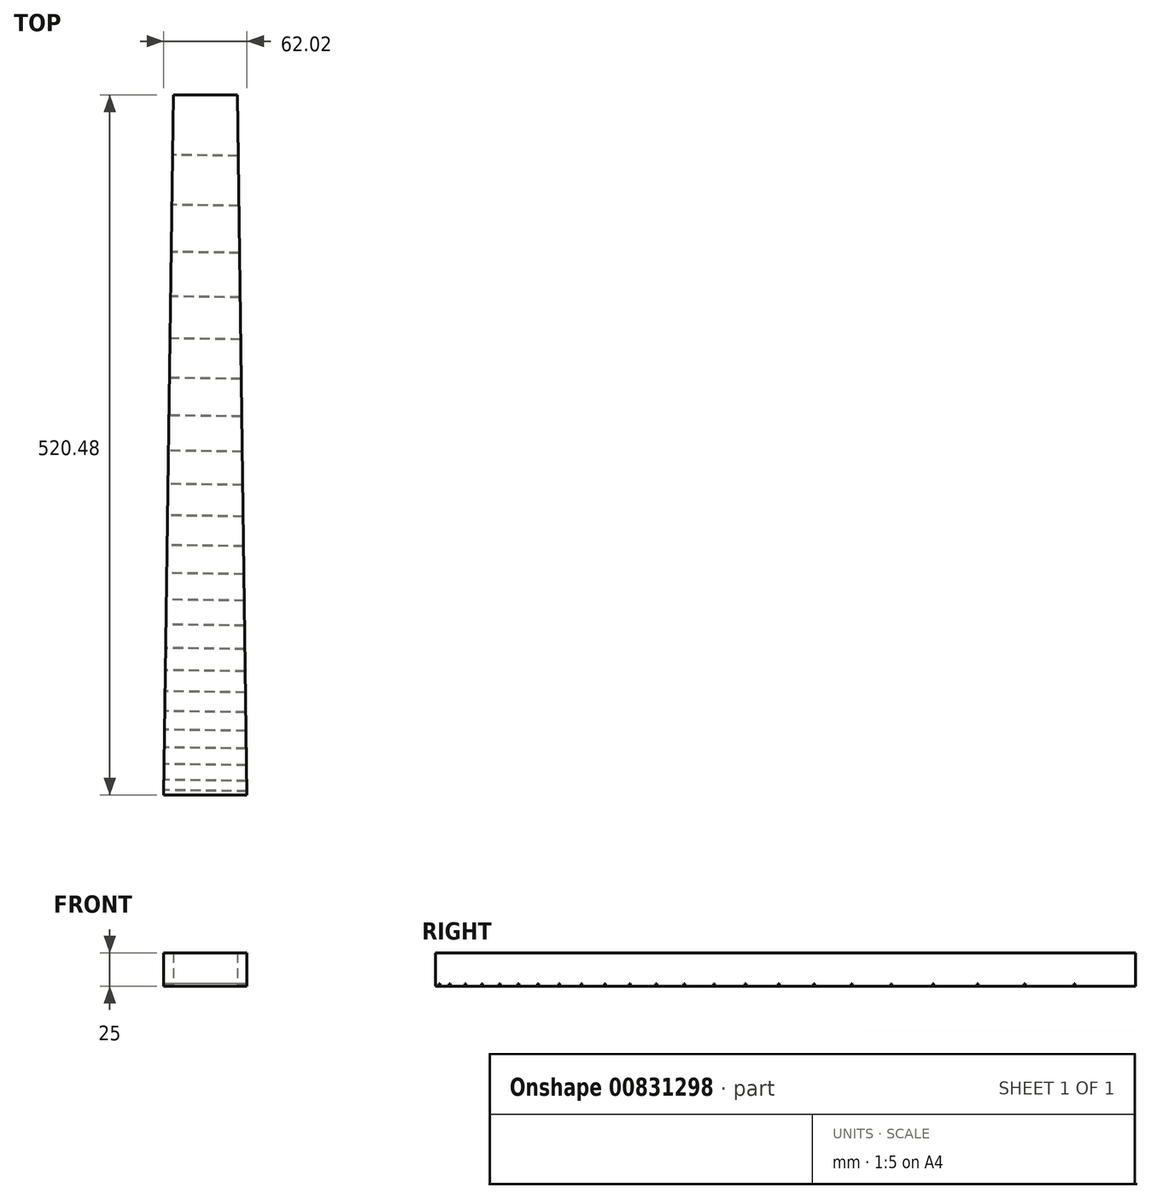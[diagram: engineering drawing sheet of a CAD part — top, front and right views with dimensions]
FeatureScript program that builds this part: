
annotation { "Feature Type Name" : "Feature", "Feature Type Description" : "" }
export const myFeature = defineFeature(function(context is Context, id is Id, definition is map)
    precondition{}
    {
        {
            var Q0;
            Q0=qCreatedBy(makeId("Top.planeOp"),FACE);
            var sketch = newSketch(context, id + "F0", { "sketchPlane" : qUnion([Q0])});
            skLineSegment(sketch, "E0", {"start": v(-23.73, 380.97) * mm, "end": v(-18.76, 380.97) * mm});
            skLineSegment(sketch, "E1", {"start": v(-23.73, 375.78) * mm, "end": v(-18.76, 375.78) * mm});
            skLineSegment(sketch, "E2", {"start": v(-23.73, 380.97) * mm, "end": v(-23.73, 375.78) * mm});
            skLineSegment(sketch, "E3", {"start": v(23.73, 380.97) * mm, "end": v(23.73, 375.78) * mm});
            skLineSegment(sketch, "E4", {"start": v(-18.76, 380.97) * mm, "end": v(-18.76, 375.78) * mm});
            skLineSegment(sketch, "E5", {"start": v(18.76, 380.97) * mm, "end": v(18.76, 375.78) * mm});
            skLineSegment(sketch, "E6", {"start": v(-11.26, 380.97) * mm, "end": v(-11.26, 375.78) * mm});
            skLineSegment(sketch, "E7", {"start": v(-3.75, 380.97) * mm, "end": v(-3.75, 375.78) * mm});
            skLineSegment(sketch, "E8", {"start": v(3.75, 380.97) * mm, "end": v(3.75, 375.78) * mm});
            skLineSegment(sketch, "E9", {"start": v(11.26, 380.97) * mm, "end": v(11.26, 375.78) * mm});
            skLineSegment(sketch, "E10", {"start": v(-30.84, -128.33) * mm, "end": v(30.86, -128.33) * mm});
            skLineSegment(sketch, "E11", {"start": v(-30.67, -116.63) * mm, "end": v(30.7, -116.63) * mm});
            skLineSegment(sketch, "E12", {"start": v(-30.5, -104.25) * mm, "end": v(30.52, -104.25) * mm});
            skLineSegment(sketch, "E13", {"start": v(-30.31, -91.12) * mm, "end": v(30.33, -91.12) * mm});
            skLineSegment(sketch, "E14", {"start": v(-30.12, -77.22) * mm, "end": v(30.14, -77.22) * mm});
            skLineSegment(sketch, "E15", {"start": v(-29.9, -62.48) * mm, "end": v(29.93, -62.48) * mm});
            skLineSegment(sketch, "E16", {"start": v(-29.69, -46.87) * mm, "end": v(29.7, -46.87) * mm});
            skLineSegment(sketch, "E17", {"start": v(-29.46, -30.34) * mm, "end": v(29.47, -30.34) * mm});
            skLineSegment(sketch, "E18", {"start": v(-29.2, -12.82) * mm, "end": v(29.23, -12.82) * mm});
            skLineSegment(sketch, "E19", {"start": v(-28.95, 5.74) * mm, "end": v(28.96, 5.74) * mm});
            skLineSegment(sketch, "E20", {"start": v(-28.67, 25.4) * mm, "end": v(28.68, 25.4) * mm});
            skLineSegment(sketch, "E21", {"start": v(-28.37, 46.24) * mm, "end": v(28.39, 46.24) * mm});
            skLineSegment(sketch, "E22", {"start": v(-28.06, 68.31) * mm, "end": v(28.08, 68.31) * mm});
            skLineSegment(sketch, "E23", {"start": v(-27.73, 91.7) * mm, "end": v(27.75, 91.7) * mm});
            skLineSegment(sketch, "E24", {"start": v(-27.38, 116.48) * mm, "end": v(27.4, 116.48) * mm});
            skLineSegment(sketch, "E25", {"start": v(-27.01, 142.73) * mm, "end": v(27.02, 142.73) * mm});
            skLineSegment(sketch, "E26", {"start": v(-26.62, 170.54) * mm, "end": v(26.63, 170.54) * mm});
            skLineSegment(sketch, "E27", {"start": v(-26.2, 200) * mm, "end": v(26.21, 200) * mm});
            skLineSegment(sketch, "E28", {"start": v(-25.77, 231.22) * mm, "end": v(25.77, 231.22) * mm});
            skLineSegment(sketch, "E29", {"start": v(-25.3, 264.29) * mm, "end": v(25.3, 264.29) * mm});
            skLineSegment(sketch, "E30", {"start": v(-24.8, 299.33) * mm, "end": v(24.8, 299.33) * mm});
            skLineSegment(sketch, "E31", {"start": v(-24.28, 336.45) * mm, "end": v(24.28, 336.45) * mm});
            skLineSegment(sketch, "E32", {"start": v(-18.76, 375.78) * mm, "end": v(-28.7, -328.27) * mm});
            skLineSegment(sketch, "E33", {"start": v(-11.26, 375.78) * mm, "end": v(-17.22, -327.17) * mm});
            skLineSegment(sketch, "E34", {"start": v(-3.75, 375.78) * mm, "end": v(-5.74, -326.07) * mm});
            skLineSegment(sketch, "E35", {"start": v(5.74, -328.27) * mm, "end": v(3.75, 375.78) * mm});
            skLineSegment(sketch, "E36", {"start": v(11.26, 375.78) * mm, "end": v(17.22, -327.17) * mm});
            skLineSegment(sketch, "E37", {"start": v(28.7, -326.07) * mm, "end": v(18.76, 375.78) * mm});
            skLineSegment(sketch, "E38", {"start": v(-23.73, 375.78) * mm, "end": v(-24.28, 336.45) * mm});
            skLineSegment(sketch, "E39", {"start": v(31.02, -139.51) * mm, "end": v(30.86, -128.33) * mm});
            skLineSegment(sketch, "E40", {"start": v(-9.05, -329.38) * mm, "end": v(-8.77, -329.38) * mm});
            skLineSegment(sketch, "E41", {"start": v(-2.43, -329.38) * mm, "end": v(-2.32, -329.37) * mm});
            skLineSegment(sketch, "E42", {"start": v(-2.32, -329.37) * mm, "end": v(-2.2, -329.36) * mm});
            skLineSegment(sketch, "E43", {"start": v(-2.2, -329.36) * mm, "end": v(-2.1, -329.35) * mm});
            skLineSegment(sketch, "E44", {"start": v(-2.1, -329.35) * mm, "end": v(-2, -329.32) * mm});
            skLineSegment(sketch, "E45", {"start": v(-2, -329.32) * mm, "end": v(-1.88, -329.29) * mm});
            skLineSegment(sketch, "E46", {"start": v(-1.88, -329.29) * mm, "end": v(-1.78, -329.25) * mm});
            skLineSegment(sketch, "E47", {"start": v(-1.78, -329.25) * mm, "end": v(-1.68, -329.2) * mm});
            skLineSegment(sketch, "E48", {"start": v(-1.68, -329.2) * mm, "end": v(-1.58, -329.15) * mm});
            skLineSegment(sketch, "E49", {"start": v(-1.58, -329.15) * mm, "end": v(-1.5, -329.09) * mm});
            skLineSegment(sketch, "E50", {"start": v(-1.5, -329.09) * mm, "end": v(-1.4, -329.02) * mm});
            skLineSegment(sketch, "E51", {"start": v(-1.4, -329.02) * mm, "end": v(-1.32, -328.95) * mm});
            skLineSegment(sketch, "E52", {"start": v(-1.32, -328.95) * mm, "end": v(-1.24, -328.87) * mm});
            skLineSegment(sketch, "E53", {"start": v(-1.24, -328.87) * mm, "end": v(-1.16, -328.8) * mm});
            skLineSegment(sketch, "E54", {"start": v(-1.16, -328.8) * mm, "end": v(-1.1, -328.7) * mm});
            skLineSegment(sketch, "E55", {"start": v(-1.1, -328.7) * mm, "end": v(-1.03, -328.61) * mm});
            skLineSegment(sketch, "E56", {"start": v(-1.03, -328.61) * mm, "end": v(-0.98, -328.52) * mm});
            skLineSegment(sketch, "E57", {"start": v(-0.98, -328.52) * mm, "end": v(-0.93, -328.42) * mm});
            skLineSegment(sketch, "E58", {"start": v(-0.93, -328.42) * mm, "end": v(-0.88, -328.32) * mm});
            skLineSegment(sketch, "E59", {"start": v(-0.88, -328.32) * mm, "end": v(-0.85, -328.21) * mm});
            skLineSegment(sketch, "E60", {"start": v(-0.85, -328.21) * mm, "end": v(-0.82, -328.1) * mm});
            skLineSegment(sketch, "E61", {"start": v(-0.82, -328.1) * mm, "end": v(-0.8, -328) * mm});
            skLineSegment(sketch, "E62", {"start": v(-0.8, -328) * mm, "end": v(-0.78, -327.89) * mm});
            skLineSegment(sketch, "E63", {"start": v(-0.78, -327.89) * mm, "end": v(-0.77, -327.78) * mm});
            skLineSegment(sketch, "E64", {"start": v(-0.77, -327.78) * mm, "end": v(-0.77, -327.67) * mm});
            skLineSegment(sketch, "E65", {"start": v(-0.77, -327.67) * mm, "end": v(-0.78, -327.56) * mm});
            skLineSegment(sketch, "E66", {"start": v(-0.78, -327.56) * mm, "end": v(-0.8, -327.45) * mm});
            skLineSegment(sketch, "E67", {"start": v(-0.8, -327.45) * mm, "end": v(-0.82, -327.34) * mm});
            skLineSegment(sketch, "E68", {"start": v(-0.82, -327.34) * mm, "end": v(-0.85, -327.23) * mm});
            skLineSegment(sketch, "E69", {"start": v(-0.85, -327.23) * mm, "end": v(-0.88, -327.13) * mm});
            skLineSegment(sketch, "E70", {"start": v(-0.88, -327.13) * mm, "end": v(-0.93, -327.03) * mm});
            skLineSegment(sketch, "E71", {"start": v(-0.93, -327.03) * mm, "end": v(-0.98, -326.93) * mm});
            skLineSegment(sketch, "E72", {"start": v(-0.98, -326.93) * mm, "end": v(-1.03, -326.83) * mm});
            skLineSegment(sketch, "E73", {"start": v(-1.03, -326.83) * mm, "end": v(-1.1, -326.74) * mm});
            skLineSegment(sketch, "E74", {"start": v(-1.1, -326.74) * mm, "end": v(-1.16, -326.65) * mm});
            skLineSegment(sketch, "E75", {"start": v(-1.16, -326.65) * mm, "end": v(-1.24, -326.57) * mm});
            skLineSegment(sketch, "E76", {"start": v(-1.24, -326.57) * mm, "end": v(-1.32, -326.5) * mm});
            skLineSegment(sketch, "E77", {"start": v(-1.32, -326.5) * mm, "end": v(-1.4, -326.42) * mm});
            skLineSegment(sketch, "E78", {"start": v(-1.4, -326.42) * mm, "end": v(-1.5, -326.36) * mm});
            skLineSegment(sketch, "E79", {"start": v(-1.5, -326.36) * mm, "end": v(-1.58, -326.3) * mm});
            skLineSegment(sketch, "E80", {"start": v(-1.58, -326.3) * mm, "end": v(-1.68, -326.25) * mm});
            skLineSegment(sketch, "E81", {"start": v(-1.68, -326.25) * mm, "end": v(-1.78, -326.2) * mm});
            skLineSegment(sketch, "E82", {"start": v(-1.78, -326.2) * mm, "end": v(-1.88, -326.16) * mm});
            skLineSegment(sketch, "E83", {"start": v(-1.88, -326.16) * mm, "end": v(-2, -326.13) * mm});
            skLineSegment(sketch, "E84", {"start": v(-2, -326.13) * mm, "end": v(-2.1, -326.1) * mm});
            skLineSegment(sketch, "E85", {"start": v(-2.1, -326.1) * mm, "end": v(-2.2, -326.08) * mm});
            skLineSegment(sketch, "E86", {"start": v(-2.2, -326.08) * mm, "end": v(-2.32, -326.07) * mm});
            skLineSegment(sketch, "E87", {"start": v(-2.32, -326.07) * mm, "end": v(-2.43, -326.07) * mm});
            skLineSegment(sketch, "E88", {"start": v(-2.43, -326.07) * mm, "end": v(-2.7, -326.07) * mm});
            skLineSegment(sketch, "E89", {"start": v(-9.05, -326.07) * mm, "end": v(-9.16, -326.07) * mm});
            skLineSegment(sketch, "E90", {"start": v(-9.16, -326.07) * mm, "end": v(-9.27, -326.08) * mm});
            skLineSegment(sketch, "E91", {"start": v(-9.27, -326.08) * mm, "end": v(-9.38, -326.1) * mm});
            skLineSegment(sketch, "E92", {"start": v(-9.38, -326.1) * mm, "end": v(-9.49, -326.13) * mm});
            skLineSegment(sketch, "E93", {"start": v(-9.49, -326.13) * mm, "end": v(-9.6, -326.16) * mm});
            skLineSegment(sketch, "E94", {"start": v(-9.6, -326.16) * mm, "end": v(-9.7, -326.2) * mm});
            skLineSegment(sketch, "E95", {"start": v(-9.7, -326.2) * mm, "end": v(-9.8, -326.25) * mm});
            skLineSegment(sketch, "E96", {"start": v(-9.8, -326.25) * mm, "end": v(-9.9, -326.3) * mm});
            skLineSegment(sketch, "E97", {"start": v(-9.9, -326.3) * mm, "end": v(-9.99, -326.36) * mm});
            skLineSegment(sketch, "E98", {"start": v(-9.99, -326.36) * mm, "end": v(-10.07, -326.42) * mm});
            skLineSegment(sketch, "E99", {"start": v(-10.07, -326.42) * mm, "end": v(-10.16, -326.5) * mm});
            skLineSegment(sketch, "E100", {"start": v(-10.16, -326.5) * mm, "end": v(-10.24, -326.57) * mm});
            skLineSegment(sketch, "E101", {"start": v(-10.24, -326.57) * mm, "end": v(-10.31, -326.65) * mm});
            skLineSegment(sketch, "E102", {"start": v(-10.31, -326.65) * mm, "end": v(-10.38, -326.74) * mm});
            skLineSegment(sketch, "E103", {"start": v(-10.38, -326.74) * mm, "end": v(-10.44, -326.83) * mm});
            skLineSegment(sketch, "E104", {"start": v(-10.44, -326.83) * mm, "end": v(-10.5, -326.93) * mm});
            skLineSegment(sketch, "E105", {"start": v(-10.5, -326.93) * mm, "end": v(-10.55, -327.03) * mm});
            skLineSegment(sketch, "E106", {"start": v(-10.55, -327.03) * mm, "end": v(-10.6, -327.13) * mm});
            skLineSegment(sketch, "E107", {"start": v(-10.6, -327.13) * mm, "end": v(-10.63, -327.23) * mm});
            skLineSegment(sketch, "E108", {"start": v(-10.63, -327.23) * mm, "end": v(-10.66, -327.34) * mm});
            skLineSegment(sketch, "E109", {"start": v(-10.66, -327.34) * mm, "end": v(-10.68, -327.45) * mm});
            skLineSegment(sketch, "E110", {"start": v(-10.68, -327.45) * mm, "end": v(-10.7, -327.56) * mm});
            skLineSegment(sketch, "E111", {"start": v(-10.7, -327.56) * mm, "end": v(-10.7, -327.67) * mm});
            skLineSegment(sketch, "E112", {"start": v(-10.7, -327.67) * mm, "end": v(-10.7, -327.78) * mm});
            skLineSegment(sketch, "E113", {"start": v(-10.7, -327.78) * mm, "end": v(-10.7, -327.89) * mm});
            skLineSegment(sketch, "E114", {"start": v(-10.7, -327.89) * mm, "end": v(-10.68, -328) * mm});
            skLineSegment(sketch, "E115", {"start": v(-10.68, -328) * mm, "end": v(-10.66, -328.1) * mm});
            skLineSegment(sketch, "E116", {"start": v(-10.66, -328.1) * mm, "end": v(-10.63, -328.21) * mm});
            skLineSegment(sketch, "E117", {"start": v(-10.63, -328.21) * mm, "end": v(-10.6, -328.32) * mm});
            skLineSegment(sketch, "E118", {"start": v(-10.6, -328.32) * mm, "end": v(-10.55, -328.42) * mm});
            skLineSegment(sketch, "E119", {"start": v(-10.55, -328.42) * mm, "end": v(-10.5, -328.52) * mm});
            skLineSegment(sketch, "E120", {"start": v(-10.5, -328.52) * mm, "end": v(-10.44, -328.61) * mm});
            skLineSegment(sketch, "E121", {"start": v(-10.44, -328.61) * mm, "end": v(-10.38, -328.7) * mm});
            skLineSegment(sketch, "E122", {"start": v(-10.38, -328.7) * mm, "end": v(-10.31, -328.8) * mm});
            skLineSegment(sketch, "E123", {"start": v(-10.31, -328.8) * mm, "end": v(-10.24, -328.87) * mm});
            skLineSegment(sketch, "E124", {"start": v(-10.24, -328.87) * mm, "end": v(-10.16, -328.95) * mm});
            skLineSegment(sketch, "E125", {"start": v(-10.16, -328.95) * mm, "end": v(-10.07, -329.02) * mm});
            skLineSegment(sketch, "E126", {"start": v(-10.07, -329.02) * mm, "end": v(-9.99, -329.09) * mm});
            skLineSegment(sketch, "E127", {"start": v(-9.99, -329.09) * mm, "end": v(-9.9, -329.15) * mm});
            skLineSegment(sketch, "E128", {"start": v(-9.9, -329.15) * mm, "end": v(-9.8, -329.2) * mm});
            skLineSegment(sketch, "E129", {"start": v(-9.8, -329.2) * mm, "end": v(-9.7, -329.25) * mm});
            skLineSegment(sketch, "E130", {"start": v(-9.7, -329.25) * mm, "end": v(-9.6, -329.29) * mm});
            skLineSegment(sketch, "E131", {"start": v(-9.6, -329.29) * mm, "end": v(-9.49, -329.32) * mm});
            skLineSegment(sketch, "E132", {"start": v(-9.49, -329.32) * mm, "end": v(-9.38, -329.35) * mm});
            skLineSegment(sketch, "E133", {"start": v(-9.38, -329.35) * mm, "end": v(-9.27, -329.36) * mm});
            skLineSegment(sketch, "E134", {"start": v(-9.27, -329.36) * mm, "end": v(-9.16, -329.37) * mm});
            skLineSegment(sketch, "E135", {"start": v(-9.16, -329.37) * mm, "end": v(-9.05, -329.38) * mm});
            skLineSegment(sketch, "E136", {"start": v(-8.77, -329.38) * mm, "end": v(-8.77, -333.8) * mm});
            skLineSegment(sketch, "E137", {"start": v(-8.77, -333.8) * mm, "end": v(-2.7, -333.8) * mm});
            skLineSegment(sketch, "E138", {"start": v(-2.7, -333.8) * mm, "end": v(-2.7, -329.38) * mm});
            skLineSegment(sketch, "E139", {"start": v(-2.7, -326.07) * mm, "end": v(-2.7, -322.76) * mm});
            skLineSegment(sketch, "E140", {"start": v(-2.7, -322.76) * mm, "end": v(-8.77, -322.76) * mm});
            skLineSegment(sketch, "E141", {"start": v(-8.77, -322.76) * mm, "end": v(-8.77, -326.07) * mm});
            skLineSegment(sketch, "E142", {"start": v(39.18, -336) * mm, "end": v(34.9, -336) * mm});
            skLineSegment(sketch, "E143", {"start": v(-39.18, -336) * mm, "end": v(-39.68, -335.98) * mm});
            skLineSegment(sketch, "E144", {"start": v(-39.68, -335.98) * mm, "end": v(-40.18, -335.93) * mm});
            skLineSegment(sketch, "E145", {"start": v(-40.18, -335.93) * mm, "end": v(-40.68, -335.85) * mm});
            skLineSegment(sketch, "E146", {"start": v(-40.68, -335.85) * mm, "end": v(-41.17, -335.74) * mm});
            skLineSegment(sketch, "E147", {"start": v(-41.17, -335.74) * mm, "end": v(-41.66, -335.59) * mm});
            skLineSegment(sketch, "E148", {"start": v(-41.66, -335.59) * mm, "end": v(-42.13, -335.41) * mm});
            skLineSegment(sketch, "E149", {"start": v(-42.13, -335.41) * mm, "end": v(-42.6, -335.2) * mm});
            skLineSegment(sketch, "E150", {"start": v(-42.6, -335.2) * mm, "end": v(-43.04, -334.96) * mm});
            skLineSegment(sketch, "E151", {"start": v(-43.04, -334.96) * mm, "end": v(-43.47, -334.7) * mm});
            skLineSegment(sketch, "E152", {"start": v(-43.47, -334.7) * mm, "end": v(-43.88, -334.4) * mm});
            skLineSegment(sketch, "E153", {"start": v(-43.88, -334.4) * mm, "end": v(-44.27, -334.08) * mm});
            skLineSegment(sketch, "E154", {"start": v(-44.27, -334.08) * mm, "end": v(-44.64, -333.74) * mm});
            skLineSegment(sketch, "E155", {"start": v(-44.64, -333.74) * mm, "end": v(-44.98, -333.37) * mm});
            skLineSegment(sketch, "E156", {"start": v(-44.98, -333.37) * mm, "end": v(-45.3, -332.98) * mm});
            skLineSegment(sketch, "E157", {"start": v(-45.3, -332.98) * mm, "end": v(-45.6, -332.57) * mm});
            skLineSegment(sketch, "E158", {"start": v(-45.6, -332.57) * mm, "end": v(-45.87, -332.14) * mm});
            skLineSegment(sketch, "E159", {"start": v(-45.87, -332.14) * mm, "end": v(-46.1, -331.7) * mm});
            skLineSegment(sketch, "E160", {"start": v(-46.1, -331.7) * mm, "end": v(-46.31, -331.23) * mm});
            skLineSegment(sketch, "E161", {"start": v(-46.31, -331.23) * mm, "end": v(-46.5, -330.76) * mm});
            skLineSegment(sketch, "E162", {"start": v(-46.5, -330.76) * mm, "end": v(-46.64, -330.27) * mm});
            skLineSegment(sketch, "E163", {"start": v(-46.64, -330.27) * mm, "end": v(-46.75, -329.78) * mm});
            skLineSegment(sketch, "E164", {"start": v(-46.75, -329.78) * mm, "end": v(-46.83, -329.28) * mm});
            skLineSegment(sketch, "E165", {"start": v(-46.83, -329.28) * mm, "end": v(-46.88, -328.78) * mm});
            skLineSegment(sketch, "E166", {"start": v(-46.88, -328.78) * mm, "end": v(-46.9, -328.27) * mm});
            skLineSegment(sketch, "E167", {"start": v(-46.9, -328.27) * mm, "end": v(-46.88, -327.77) * mm});
            skLineSegment(sketch, "E168", {"start": v(-46.88, -327.77) * mm, "end": v(-46.83, -327.27) * mm});
            skLineSegment(sketch, "E169", {"start": v(-46.83, -327.27) * mm, "end": v(-46.75, -326.77) * mm});
            skLineSegment(sketch, "E170", {"start": v(-46.75, -326.77) * mm, "end": v(-46.64, -326.28) * mm});
            skLineSegment(sketch, "E171", {"start": v(-46.64, -326.28) * mm, "end": v(-46.5, -325.8) * mm});
            skLineSegment(sketch, "E172", {"start": v(-46.5, -325.8) * mm, "end": v(-46.31, -325.32) * mm});
            skLineSegment(sketch, "E173", {"start": v(-46.31, -325.32) * mm, "end": v(-46.1, -324.86) * mm});
            skLineSegment(sketch, "E174", {"start": v(-46.1, -324.86) * mm, "end": v(-45.87, -324.41) * mm});
            skLineSegment(sketch, "E175", {"start": v(-45.87, -324.41) * mm, "end": v(-45.6, -323.98) * mm});
            skLineSegment(sketch, "E176", {"start": v(-45.6, -323.98) * mm, "end": v(-45.3, -323.57) * mm});
            skLineSegment(sketch, "E177", {"start": v(-45.3, -323.57) * mm, "end": v(-44.98, -323.18) * mm});
            skLineSegment(sketch, "E178", {"start": v(-44.98, -323.18) * mm, "end": v(-44.64, -322.81) * mm});
            skLineSegment(sketch, "E179", {"start": v(-44.64, -322.81) * mm, "end": v(-44.27, -322.47) * mm});
            skLineSegment(sketch, "E180", {"start": v(-44.27, -322.47) * mm, "end": v(-43.88, -322.15) * mm});
            skLineSegment(sketch, "E181", {"start": v(-43.88, -322.15) * mm, "end": v(-43.47, -321.85) * mm});
            skLineSegment(sketch, "E182", {"start": v(-43.47, -321.85) * mm, "end": v(-43.04, -321.58) * mm});
            skLineSegment(sketch, "E183", {"start": v(-43.04, -321.58) * mm, "end": v(-42.6, -321.35) * mm});
            skLineSegment(sketch, "E184", {"start": v(-42.6, -321.35) * mm, "end": v(-42.13, -321.14) * mm});
            skLineSegment(sketch, "E185", {"start": v(-42.13, -321.14) * mm, "end": v(-41.66, -320.96) * mm});
            skLineSegment(sketch, "E186", {"start": v(-41.66, -320.96) * mm, "end": v(-41.17, -320.81) * mm});
            skLineSegment(sketch, "E187", {"start": v(-41.17, -320.81) * mm, "end": v(-40.68, -320.7) * mm});
            skLineSegment(sketch, "E188", {"start": v(-40.68, -320.7) * mm, "end": v(-40.18, -320.62) * mm});
            skLineSegment(sketch, "E189", {"start": v(-40.18, -320.62) * mm, "end": v(-39.68, -320.57) * mm});
            skLineSegment(sketch, "E190", {"start": v(-39.68, -320.57) * mm, "end": v(-39.18, -320.55) * mm});
            skLineSegment(sketch, "E191", {"start": v(-39.18, -320.55) * mm, "end": v(-34.9, -320.55) * mm});
            skLineSegment(sketch, "E192", {"start": v(39.18, -320.55) * mm, "end": v(39.68, -320.57) * mm});
            skLineSegment(sketch, "E193", {"start": v(39.68, -320.57) * mm, "end": v(40.18, -320.62) * mm});
            skLineSegment(sketch, "E194", {"start": v(40.18, -320.62) * mm, "end": v(40.68, -320.7) * mm});
            skLineSegment(sketch, "E195", {"start": v(40.68, -320.7) * mm, "end": v(41.17, -320.81) * mm});
            skLineSegment(sketch, "E196", {"start": v(41.17, -320.81) * mm, "end": v(41.66, -320.96) * mm});
            skLineSegment(sketch, "E197", {"start": v(41.66, -320.96) * mm, "end": v(42.13, -321.14) * mm});
            skLineSegment(sketch, "E198", {"start": v(42.13, -321.14) * mm, "end": v(42.6, -321.35) * mm});
            skLineSegment(sketch, "E199", {"start": v(42.6, -321.35) * mm, "end": v(43.04, -321.58) * mm});
            skLineSegment(sketch, "E200", {"start": v(43.04, -321.58) * mm, "end": v(43.47, -321.85) * mm});
            skLineSegment(sketch, "E201", {"start": v(43.47, -321.85) * mm, "end": v(43.88, -322.15) * mm});
            skLineSegment(sketch, "E202", {"start": v(43.88, -322.15) * mm, "end": v(44.27, -322.47) * mm});
            skLineSegment(sketch, "E203", {"start": v(44.27, -322.47) * mm, "end": v(44.64, -322.81) * mm});
            skLineSegment(sketch, "E204", {"start": v(44.64, -322.81) * mm, "end": v(44.98, -323.18) * mm});
            skLineSegment(sketch, "E205", {"start": v(44.98, -323.18) * mm, "end": v(45.3, -323.57) * mm});
            skLineSegment(sketch, "E206", {"start": v(45.3, -323.57) * mm, "end": v(45.6, -323.98) * mm});
            skLineSegment(sketch, "E207", {"start": v(45.6, -323.98) * mm, "end": v(45.87, -324.41) * mm});
            skLineSegment(sketch, "E208", {"start": v(45.87, -324.41) * mm, "end": v(46.1, -324.86) * mm});
            skLineSegment(sketch, "E209", {"start": v(46.1, -324.86) * mm, "end": v(46.31, -325.32) * mm});
            skLineSegment(sketch, "E210", {"start": v(46.31, -325.32) * mm, "end": v(46.5, -325.8) * mm});
            skLineSegment(sketch, "E211", {"start": v(46.5, -325.8) * mm, "end": v(46.64, -326.28) * mm});
            skLineSegment(sketch, "E212", {"start": v(46.64, -326.28) * mm, "end": v(46.75, -326.77) * mm});
            skLineSegment(sketch, "E213", {"start": v(46.75, -326.77) * mm, "end": v(46.83, -327.27) * mm});
            skLineSegment(sketch, "E214", {"start": v(46.83, -327.27) * mm, "end": v(46.88, -327.77) * mm});
            skLineSegment(sketch, "E215", {"start": v(46.88, -327.77) * mm, "end": v(46.9, -328.27) * mm});
            skLineSegment(sketch, "E216", {"start": v(46.9, -328.27) * mm, "end": v(46.88, -328.78) * mm});
            skLineSegment(sketch, "E217", {"start": v(46.88, -328.78) * mm, "end": v(46.83, -329.28) * mm});
            skLineSegment(sketch, "E218", {"start": v(46.83, -329.28) * mm, "end": v(46.75, -329.78) * mm});
            skLineSegment(sketch, "E219", {"start": v(46.75, -329.78) * mm, "end": v(46.64, -330.27) * mm});
            skLineSegment(sketch, "E220", {"start": v(46.64, -330.27) * mm, "end": v(46.5, -330.76) * mm});
            skLineSegment(sketch, "E221", {"start": v(46.5, -330.76) * mm, "end": v(46.31, -331.23) * mm});
            skLineSegment(sketch, "E222", {"start": v(46.31, -331.23) * mm, "end": v(46.1, -331.7) * mm});
            skLineSegment(sketch, "E223", {"start": v(46.1, -331.7) * mm, "end": v(45.87, -332.14) * mm});
            skLineSegment(sketch, "E224", {"start": v(45.87, -332.14) * mm, "end": v(45.6, -332.57) * mm});
            skLineSegment(sketch, "E225", {"start": v(45.6, -332.57) * mm, "end": v(45.3, -332.98) * mm});
            skLineSegment(sketch, "E226", {"start": v(45.3, -332.98) * mm, "end": v(44.98, -333.37) * mm});
            skLineSegment(sketch, "E227", {"start": v(44.98, -333.37) * mm, "end": v(44.64, -333.74) * mm});
            skLineSegment(sketch, "E228", {"start": v(44.64, -333.74) * mm, "end": v(44.27, -334.08) * mm});
            skLineSegment(sketch, "E229", {"start": v(44.27, -334.08) * mm, "end": v(43.88, -334.4) * mm});
            skLineSegment(sketch, "E230", {"start": v(43.88, -334.4) * mm, "end": v(43.47, -334.7) * mm});
            skLineSegment(sketch, "E231", {"start": v(43.47, -334.7) * mm, "end": v(43.04, -334.96) * mm});
            skLineSegment(sketch, "E232", {"start": v(43.04, -334.96) * mm, "end": v(42.6, -335.2) * mm});
            skLineSegment(sketch, "E233", {"start": v(42.6, -335.2) * mm, "end": v(42.13, -335.41) * mm});
            skLineSegment(sketch, "E234", {"start": v(42.13, -335.41) * mm, "end": v(41.66, -335.59) * mm});
            skLineSegment(sketch, "E235", {"start": v(41.66, -335.59) * mm, "end": v(41.17, -335.74) * mm});
            skLineSegment(sketch, "E236", {"start": v(41.17, -335.74) * mm, "end": v(40.68, -335.85) * mm});
            skLineSegment(sketch, "E237", {"start": v(40.68, -335.85) * mm, "end": v(40.18, -335.93) * mm});
            skLineSegment(sketch, "E238", {"start": v(40.18, -335.93) * mm, "end": v(39.68, -335.98) * mm});
            skLineSegment(sketch, "E239", {"start": v(39.68, -335.98) * mm, "end": v(39.18, -336) * mm});
            skLineSegment(sketch, "E240", {"start": v(-34.9, -320.55) * mm, "end": v(-35.42, -320.29) * mm});
            skLineSegment(sketch, "E241", {"start": v(-35.42, -320.29) * mm, "end": v(-35.95, -320.06) * mm});
            skLineSegment(sketch, "E242", {"start": v(-35.95, -320.06) * mm, "end": v(-36.5, -319.86) * mm});
            skLineSegment(sketch, "E243", {"start": v(-36.5, -319.86) * mm, "end": v(-37.06, -319.7) * mm});
            skLineSegment(sketch, "E244", {"start": v(-37.06, -319.7) * mm, "end": v(-37.63, -319.58) * mm});
            skLineSegment(sketch, "E245", {"start": v(-37.63, -319.58) * mm, "end": v(-38.2, -319.5) * mm});
            skLineSegment(sketch, "E246", {"start": v(-38.2, -319.5) * mm, "end": v(-38.79, -319.45) * mm});
            skLineSegment(sketch, "E247", {"start": v(-38.79, -319.45) * mm, "end": v(-39.37, -319.45) * mm});
            skLineSegment(sketch, "E248", {"start": v(-39.37, -319.45) * mm, "end": v(-39.95, -319.48) * mm});
            skLineSegment(sketch, "E249", {"start": v(-39.95, -319.48) * mm, "end": v(-40.53, -319.55) * mm});
            skLineSegment(sketch, "E250", {"start": v(-40.53, -319.55) * mm, "end": v(-41.1, -319.66) * mm});
            skLineSegment(sketch, "E251", {"start": v(-41.1, -319.66) * mm, "end": v(-41.66, -319.8) * mm});
            skLineSegment(sketch, "E252", {"start": v(-41.66, -319.8) * mm, "end": v(-42.21, -319.99) * mm});
            skLineSegment(sketch, "E253", {"start": v(-42.21, -319.99) * mm, "end": v(-42.75, -320.2) * mm});
            skLineSegment(sketch, "E254", {"start": v(-42.75, -320.2) * mm, "end": v(-43.28, -320.46) * mm});
            skLineSegment(sketch, "E255", {"start": v(-43.28, -320.46) * mm, "end": v(-43.78, -320.74) * mm});
            skLineSegment(sketch, "E256", {"start": v(-43.78, -320.74) * mm, "end": v(-44.27, -321.06) * mm});
            skLineSegment(sketch, "E257", {"start": v(-44.27, -321.06) * mm, "end": v(-44.73, -321.42) * mm});
            skLineSegment(sketch, "E258", {"start": v(-44.73, -321.42) * mm, "end": v(-45.17, -321.8) * mm});
            skLineSegment(sketch, "E259", {"start": v(-45.17, -321.8) * mm, "end": v(-45.59, -322.2) * mm});
            skLineSegment(sketch, "E260", {"start": v(-45.59, -322.2) * mm, "end": v(-45.97, -322.64) * mm});
            skLineSegment(sketch, "E261", {"start": v(-45.97, -322.64) * mm, "end": v(-46.33, -323.1) * mm});
            skLineSegment(sketch, "E262", {"start": v(-46.33, -323.1) * mm, "end": v(-46.65, -323.58) * mm});
            skLineSegment(sketch, "E263", {"start": v(-46.65, -323.58) * mm, "end": v(-46.95, -324.09) * mm});
            skLineSegment(sketch, "E264", {"start": v(-46.95, -324.09) * mm, "end": v(-47.2, -324.6) * mm});
            skLineSegment(sketch, "E265", {"start": v(-47.2, -324.6) * mm, "end": v(-47.43, -325.14) * mm});
            skLineSegment(sketch, "E266", {"start": v(-47.43, -325.14) * mm, "end": v(-47.62, -325.7) * mm});
            skLineSegment(sketch, "E267", {"start": v(-47.62, -325.7) * mm, "end": v(-47.77, -326.26) * mm});
            skLineSegment(sketch, "E268", {"start": v(-47.77, -326.26) * mm, "end": v(-47.88, -326.83) * mm});
            skLineSegment(sketch, "E269", {"start": v(-47.88, -326.83) * mm, "end": v(-47.96, -327.4) * mm});
            skLineSegment(sketch, "E270", {"start": v(-47.96, -327.4) * mm, "end": v(-48, -327.98) * mm});
            skLineSegment(sketch, "E271", {"start": v(-48, -327.98) * mm, "end": v(-48, -328.57) * mm});
            skLineSegment(sketch, "E272", {"start": v(-48, -328.57) * mm, "end": v(-47.96, -329.15) * mm});
            skLineSegment(sketch, "E273", {"start": v(-47.96, -329.15) * mm, "end": v(-47.88, -329.72) * mm});
            skLineSegment(sketch, "E274", {"start": v(-47.88, -329.72) * mm, "end": v(-47.77, -330.3) * mm});
            skLineSegment(sketch, "E275", {"start": v(-47.77, -330.3) * mm, "end": v(-47.62, -330.85) * mm});
            skLineSegment(sketch, "E276", {"start": v(-47.62, -330.85) * mm, "end": v(-47.43, -331.4) * mm});
            skLineSegment(sketch, "E277", {"start": v(-47.43, -331.4) * mm, "end": v(-47.2, -331.94) * mm});
            skLineSegment(sketch, "E278", {"start": v(-47.2, -331.94) * mm, "end": v(-46.95, -332.46) * mm});
            skLineSegment(sketch, "E279", {"start": v(-46.95, -332.46) * mm, "end": v(-46.65, -332.97) * mm});
            skLineSegment(sketch, "E280", {"start": v(-46.65, -332.97) * mm, "end": v(-46.33, -333.45) * mm});
            skLineSegment(sketch, "E281", {"start": v(-46.33, -333.45) * mm, "end": v(-45.97, -333.9) * mm});
            skLineSegment(sketch, "E282", {"start": v(-45.97, -333.9) * mm, "end": v(-45.59, -334.34) * mm});
            skLineSegment(sketch, "E283", {"start": v(-45.59, -334.34) * mm, "end": v(-45.17, -334.75) * mm});
            skLineSegment(sketch, "E284", {"start": v(-45.17, -334.75) * mm, "end": v(-44.73, -335.13) * mm});
            skLineSegment(sketch, "E285", {"start": v(-44.73, -335.13) * mm, "end": v(-44.27, -335.48) * mm});
            skLineSegment(sketch, "E286", {"start": v(-44.27, -335.48) * mm, "end": v(-43.78, -335.8) * mm});
            skLineSegment(sketch, "E287", {"start": v(-43.78, -335.8) * mm, "end": v(-43.28, -336.1) * mm});
            skLineSegment(sketch, "E288", {"start": v(-43.28, -336.1) * mm, "end": v(-42.75, -336.35) * mm});
            skLineSegment(sketch, "E289", {"start": v(-42.75, -336.35) * mm, "end": v(-42.21, -336.56) * mm});
            skLineSegment(sketch, "E290", {"start": v(-42.21, -336.56) * mm, "end": v(-41.66, -336.75) * mm});
            skLineSegment(sketch, "E291", {"start": v(-41.66, -336.75) * mm, "end": v(-41.1, -336.9) * mm});
            skLineSegment(sketch, "E292", {"start": v(-41.1, -336.9) * mm, "end": v(-40.53, -337) * mm});
            skLineSegment(sketch, "E293", {"start": v(-40.53, -337) * mm, "end": v(-39.95, -337.07) * mm});
            skLineSegment(sketch, "E294", {"start": v(-39.95, -337.07) * mm, "end": v(-39.37, -337.1) * mm});
            skLineSegment(sketch, "E295", {"start": v(-39.37, -337.1) * mm, "end": v(-38.79, -337.1) * mm});
            skLineSegment(sketch, "E296", {"start": v(-38.79, -337.1) * mm, "end": v(-38.2, -337.05) * mm});
            skLineSegment(sketch, "E297", {"start": v(-38.2, -337.05) * mm, "end": v(-37.63, -336.97) * mm});
            skLineSegment(sketch, "E298", {"start": v(-37.63, -336.97) * mm, "end": v(-37.06, -336.85) * mm});
            skLineSegment(sketch, "E299", {"start": v(-37.06, -336.85) * mm, "end": v(-36.5, -336.69) * mm});
            skLineSegment(sketch, "E300", {"start": v(-36.5, -336.69) * mm, "end": v(-35.95, -336.5) * mm});
            skLineSegment(sketch, "E301", {"start": v(-35.95, -336.5) * mm, "end": v(-35.42, -336.26) * mm});
            skLineSegment(sketch, "E302", {"start": v(-35.42, -336.26) * mm, "end": v(-34.9, -336) * mm});
            skLineSegment(sketch, "E303", {"start": v(-31.73, -331.59) * mm, "end": v(-31.73, -333.8) * mm});
            skLineSegment(sketch, "E304", {"start": v(-31.73, -333.8) * mm, "end": v(-25.66, -333.8) * mm});
            skLineSegment(sketch, "E305", {"start": v(-25.66, -333.8) * mm, "end": v(-25.66, -331.59) * mm});
            skLineSegment(sketch, "E306", {"start": v(-14.18, -330.48) * mm, "end": v(-14.18, -333.8) * mm});
            skLineSegment(sketch, "E307", {"start": v(-14.18, -333.8) * mm, "end": v(-20.25, -333.8) * mm});
            skLineSegment(sketch, "E308", {"start": v(-20.25, -333.8) * mm, "end": v(-20.25, -330.48) * mm});
            skLineSegment(sketch, "E309", {"start": v(-31.45, -336) * mm, "end": v(-31.45, -337.65) * mm});
            skLineSegment(sketch, "E310", {"start": v(-31.45, -337.65) * mm, "end": v(-25.93, -337.65) * mm});
            skLineSegment(sketch, "E311", {"start": v(-25.93, -337.65) * mm, "end": v(-25.93, -336) * mm});
            skLineSegment(sketch, "E312", {"start": v(-19.97, -336) * mm, "end": v(-19.97, -337.65) * mm});
            skLineSegment(sketch, "E313", {"start": v(-19.97, -337.65) * mm, "end": v(-14.46, -337.65) * mm});
            skLineSegment(sketch, "E314", {"start": v(-14.46, -337.65) * mm, "end": v(-14.46, -336) * mm});
            skLineSegment(sketch, "E315", {"start": v(-17.22, -330.48) * mm, "end": v(-17.22, -327.17) * mm});
            skLineSegment(sketch, "E316", {"start": v(-36.97, -328.27) * mm, "end": v(-36.97, -328.13) * mm});
            skLineSegment(sketch, "E317", {"start": v(-36.97, -328.13) * mm, "end": v(-36.99, -327.99) * mm});
            skLineSegment(sketch, "E318", {"start": v(-36.99, -327.99) * mm, "end": v(-37.01, -327.84) * mm});
            skLineSegment(sketch, "E319", {"start": v(-37.01, -327.84) * mm, "end": v(-37.04, -327.7) * mm});
            skLineSegment(sketch, "E320", {"start": v(-37.04, -327.7) * mm, "end": v(-37.09, -327.57) * mm});
            skLineSegment(sketch, "E321", {"start": v(-37.09, -327.57) * mm, "end": v(-37.14, -327.43) * mm});
            skLineSegment(sketch, "E322", {"start": v(-37.14, -327.43) * mm, "end": v(-37.2, -327.3) * mm});
            skLineSegment(sketch, "E323", {"start": v(-37.2, -327.3) * mm, "end": v(-37.26, -327.17) * mm});
            skLineSegment(sketch, "E324", {"start": v(-37.26, -327.17) * mm, "end": v(-37.34, -327.05) * mm});
            skLineSegment(sketch, "E325", {"start": v(-37.34, -327.05) * mm, "end": v(-37.42, -326.93) * mm});
            skLineSegment(sketch, "E326", {"start": v(-37.42, -326.93) * mm, "end": v(-37.52, -326.82) * mm});
            skLineSegment(sketch, "E327", {"start": v(-37.52, -326.82) * mm, "end": v(-37.61, -326.71) * mm});
            skLineSegment(sketch, "E328", {"start": v(-37.61, -326.71) * mm, "end": v(-37.72, -326.62) * mm});
            skLineSegment(sketch, "E329", {"start": v(-37.72, -326.62) * mm, "end": v(-37.83, -326.52) * mm});
            skLineSegment(sketch, "E330", {"start": v(-37.83, -326.52) * mm, "end": v(-37.95, -326.44) * mm});
            skLineSegment(sketch, "E331", {"start": v(-37.95, -326.44) * mm, "end": v(-38.07, -326.36) * mm});
            skLineSegment(sketch, "E332", {"start": v(-38.07, -326.36) * mm, "end": v(-38.2, -326.3) * mm});
            skLineSegment(sketch, "E333", {"start": v(-38.2, -326.3) * mm, "end": v(-38.33, -326.24) * mm});
            skLineSegment(sketch, "E334", {"start": v(-38.33, -326.24) * mm, "end": v(-38.47, -326.18) * mm});
            skLineSegment(sketch, "E335", {"start": v(-38.47, -326.18) * mm, "end": v(-38.6, -326.14) * mm});
            skLineSegment(sketch, "E336", {"start": v(-38.6, -326.14) * mm, "end": v(-38.74, -326.11) * mm});
            skLineSegment(sketch, "E337", {"start": v(-38.74, -326.11) * mm, "end": v(-38.89, -326.09) * mm});
            skLineSegment(sketch, "E338", {"start": v(-38.89, -326.09) * mm, "end": v(-39.03, -326.07) * mm});
            skLineSegment(sketch, "E339", {"start": v(-39.03, -326.07) * mm, "end": v(-39.18, -326.07) * mm});
            skLineSegment(sketch, "E340", {"start": v(-39.18, -326.07) * mm, "end": v(-39.32, -326.07) * mm});
            skLineSegment(sketch, "E341", {"start": v(-39.32, -326.07) * mm, "end": v(-39.46, -326.09) * mm});
            skLineSegment(sketch, "E342", {"start": v(-39.46, -326.09) * mm, "end": v(-39.6, -326.11) * mm});
            skLineSegment(sketch, "E343", {"start": v(-39.6, -326.11) * mm, "end": v(-39.75, -326.14) * mm});
            skLineSegment(sketch, "E344", {"start": v(-39.75, -326.14) * mm, "end": v(-39.89, -326.18) * mm});
            skLineSegment(sketch, "E345", {"start": v(-39.89, -326.18) * mm, "end": v(-40.02, -326.24) * mm});
            skLineSegment(sketch, "E346", {"start": v(-40.02, -326.24) * mm, "end": v(-40.15, -326.3) * mm});
            skLineSegment(sketch, "E347", {"start": v(-40.15, -326.3) * mm, "end": v(-40.28, -326.36) * mm});
            skLineSegment(sketch, "E348", {"start": v(-40.28, -326.36) * mm, "end": v(-40.4, -326.44) * mm});
            skLineSegment(sketch, "E349", {"start": v(-40.4, -326.44) * mm, "end": v(-40.52, -326.52) * mm});
            skLineSegment(sketch, "E350", {"start": v(-40.52, -326.52) * mm, "end": v(-40.63, -326.62) * mm});
            skLineSegment(sketch, "E351", {"start": v(-40.63, -326.62) * mm, "end": v(-40.74, -326.71) * mm});
            skLineSegment(sketch, "E352", {"start": v(-40.74, -326.71) * mm, "end": v(-40.83, -326.82) * mm});
            skLineSegment(sketch, "E353", {"start": v(-40.83, -326.82) * mm, "end": v(-40.93, -326.93) * mm});
            skLineSegment(sketch, "E354", {"start": v(-40.93, -326.93) * mm, "end": v(-41.01, -327.05) * mm});
            skLineSegment(sketch, "E355", {"start": v(-41.01, -327.05) * mm, "end": v(-41.09, -327.17) * mm});
            skLineSegment(sketch, "E356", {"start": v(-41.09, -327.17) * mm, "end": v(-41.16, -327.3) * mm});
            skLineSegment(sketch, "E357", {"start": v(-41.16, -327.3) * mm, "end": v(-41.21, -327.43) * mm});
            skLineSegment(sketch, "E358", {"start": v(-41.21, -327.43) * mm, "end": v(-41.27, -327.57) * mm});
            skLineSegment(sketch, "E359", {"start": v(-41.27, -327.57) * mm, "end": v(-41.3, -327.7) * mm});
            skLineSegment(sketch, "E360", {"start": v(-41.3, -327.7) * mm, "end": v(-41.34, -327.84) * mm});
            skLineSegment(sketch, "E361", {"start": v(-41.34, -327.84) * mm, "end": v(-41.36, -327.99) * mm});
            skLineSegment(sketch, "E362", {"start": v(-41.36, -327.99) * mm, "end": v(-41.38, -328.13) * mm});
            skLineSegment(sketch, "E363", {"start": v(-41.38, -328.13) * mm, "end": v(-41.38, -328.27) * mm});
            skLineSegment(sketch, "E364", {"start": v(-41.38, -328.27) * mm, "end": v(-41.38, -328.42) * mm});
            skLineSegment(sketch, "E365", {"start": v(-41.38, -328.42) * mm, "end": v(-41.36, -328.56) * mm});
            skLineSegment(sketch, "E366", {"start": v(-41.36, -328.56) * mm, "end": v(-41.34, -328.7) * mm});
            skLineSegment(sketch, "E367", {"start": v(-41.34, -328.7) * mm, "end": v(-41.3, -328.85) * mm});
            skLineSegment(sketch, "E368", {"start": v(-41.3, -328.85) * mm, "end": v(-41.27, -328.98) * mm});
            skLineSegment(sketch, "E369", {"start": v(-41.27, -328.98) * mm, "end": v(-41.21, -329.12) * mm});
            skLineSegment(sketch, "E370", {"start": v(-41.21, -329.12) * mm, "end": v(-41.16, -329.25) * mm});
            skLineSegment(sketch, "E371", {"start": v(-41.16, -329.25) * mm, "end": v(-41.09, -329.38) * mm});
            skLineSegment(sketch, "E372", {"start": v(-41.09, -329.38) * mm, "end": v(-41.01, -329.5) * mm});
            skLineSegment(sketch, "E373", {"start": v(-41.01, -329.5) * mm, "end": v(-40.93, -329.62) * mm});
            skLineSegment(sketch, "E374", {"start": v(-40.93, -329.62) * mm, "end": v(-40.83, -329.73) * mm});
            skLineSegment(sketch, "E375", {"start": v(-40.83, -329.73) * mm, "end": v(-40.74, -329.84) * mm});
            skLineSegment(sketch, "E376", {"start": v(-40.74, -329.84) * mm, "end": v(-40.63, -329.93) * mm});
            skLineSegment(sketch, "E377", {"start": v(-40.63, -329.93) * mm, "end": v(-40.52, -330.03) * mm});
            skLineSegment(sketch, "E378", {"start": v(-40.52, -330.03) * mm, "end": v(-40.4, -330.1) * mm});
            skLineSegment(sketch, "E379", {"start": v(-40.4, -330.1) * mm, "end": v(-40.28, -330.19) * mm});
            skLineSegment(sketch, "E380", {"start": v(-40.28, -330.19) * mm, "end": v(-40.15, -330.25) * mm});
            skLineSegment(sketch, "E381", {"start": v(-40.15, -330.25) * mm, "end": v(-40.02, -330.31) * mm});
            skLineSegment(sketch, "E382", {"start": v(-40.02, -330.31) * mm, "end": v(-39.89, -330.36) * mm});
            skLineSegment(sketch, "E383", {"start": v(-39.89, -330.36) * mm, "end": v(-39.75, -330.4) * mm});
            skLineSegment(sketch, "E384", {"start": v(-39.75, -330.4) * mm, "end": v(-39.6, -330.44) * mm});
            skLineSegment(sketch, "E385", {"start": v(-39.6, -330.44) * mm, "end": v(-39.46, -330.46) * mm});
            skLineSegment(sketch, "E386", {"start": v(-39.46, -330.46) * mm, "end": v(-39.32, -330.48) * mm});
            skLineSegment(sketch, "E387", {"start": v(-39.32, -330.48) * mm, "end": v(-39.18, -330.48) * mm});
            skLineSegment(sketch, "E388", {"start": v(-39.18, -330.48) * mm, "end": v(-39.03, -330.48) * mm});
            skLineSegment(sketch, "E389", {"start": v(-39.03, -330.48) * mm, "end": v(-38.89, -330.46) * mm});
            skLineSegment(sketch, "E390", {"start": v(-38.89, -330.46) * mm, "end": v(-38.74, -330.44) * mm});
            skLineSegment(sketch, "E391", {"start": v(-38.74, -330.44) * mm, "end": v(-38.6, -330.4) * mm});
            skLineSegment(sketch, "E392", {"start": v(-38.6, -330.4) * mm, "end": v(-38.47, -330.36) * mm});
            skLineSegment(sketch, "E393", {"start": v(-38.47, -330.36) * mm, "end": v(-38.33, -330.31) * mm});
            skLineSegment(sketch, "E394", {"start": v(-38.33, -330.31) * mm, "end": v(-38.2, -330.25) * mm});
            skLineSegment(sketch, "E395", {"start": v(-38.2, -330.25) * mm, "end": v(-38.07, -330.19) * mm});
            skLineSegment(sketch, "E396", {"start": v(-38.07, -330.19) * mm, "end": v(-37.95, -330.1) * mm});
            skLineSegment(sketch, "E397", {"start": v(-37.95, -330.1) * mm, "end": v(-37.83, -330.03) * mm});
            skLineSegment(sketch, "E398", {"start": v(-37.83, -330.03) * mm, "end": v(-37.72, -329.93) * mm});
            skLineSegment(sketch, "E399", {"start": v(-37.72, -329.93) * mm, "end": v(-37.61, -329.84) * mm});
            skLineSegment(sketch, "E400", {"start": v(-37.61, -329.84) * mm, "end": v(-37.52, -329.73) * mm});
            skLineSegment(sketch, "E401", {"start": v(-37.52, -329.73) * mm, "end": v(-37.42, -329.62) * mm});
            skLineSegment(sketch, "E402", {"start": v(-37.42, -329.62) * mm, "end": v(-37.34, -329.5) * mm});
            skLineSegment(sketch, "E403", {"start": v(-37.34, -329.5) * mm, "end": v(-37.26, -329.38) * mm});
            skLineSegment(sketch, "E404", {"start": v(-37.26, -329.38) * mm, "end": v(-37.2, -329.25) * mm});
            skLineSegment(sketch, "E405", {"start": v(-37.2, -329.25) * mm, "end": v(-37.14, -329.12) * mm});
            skLineSegment(sketch, "E406", {"start": v(-37.14, -329.12) * mm, "end": v(-37.09, -328.98) * mm});
            skLineSegment(sketch, "E407", {"start": v(-37.09, -328.98) * mm, "end": v(-37.04, -328.85) * mm});
            skLineSegment(sketch, "E408", {"start": v(-37.04, -328.85) * mm, "end": v(-37.01, -328.7) * mm});
            skLineSegment(sketch, "E409", {"start": v(-37.01, -328.7) * mm, "end": v(-36.99, -328.56) * mm});
            skLineSegment(sketch, "E410", {"start": v(-36.99, -328.56) * mm, "end": v(-36.97, -328.42) * mm});
            skLineSegment(sketch, "E411", {"start": v(-36.97, -328.42) * mm, "end": v(-36.97, -328.27) * mm});
            skLineSegment(sketch, "E412", {"start": v(-28.7, -331.59) * mm, "end": v(-28.7, -328.27) * mm});
            skLineSegment(sketch, "E413", {"start": v(-32, -331.59) * mm, "end": v(-31.73, -331.59) * mm});
            skLineSegment(sketch, "E414", {"start": v(-25.38, -331.59) * mm, "end": v(-25.27, -331.58) * mm});
            skLineSegment(sketch, "E415", {"start": v(-25.27, -331.58) * mm, "end": v(-25.16, -331.57) * mm});
            skLineSegment(sketch, "E416", {"start": v(-25.16, -331.57) * mm, "end": v(-25.05, -331.55) * mm});
            skLineSegment(sketch, "E417", {"start": v(-25.05, -331.55) * mm, "end": v(-24.94, -331.53) * mm});
            skLineSegment(sketch, "E418", {"start": v(-24.94, -331.53) * mm, "end": v(-24.84, -331.5) * mm});
            skLineSegment(sketch, "E419", {"start": v(-24.84, -331.5) * mm, "end": v(-24.74, -331.45) * mm});
            skLineSegment(sketch, "E420", {"start": v(-24.74, -331.45) * mm, "end": v(-24.63, -331.4) * mm});
            skLineSegment(sketch, "E421", {"start": v(-24.63, -331.4) * mm, "end": v(-24.54, -331.35) * mm});
            skLineSegment(sketch, "E422", {"start": v(-24.54, -331.35) * mm, "end": v(-24.44, -331.3) * mm});
            skLineSegment(sketch, "E423", {"start": v(-24.44, -331.3) * mm, "end": v(-24.36, -331.23) * mm});
            skLineSegment(sketch, "E424", {"start": v(-24.36, -331.23) * mm, "end": v(-24.27, -331.16) * mm});
            skLineSegment(sketch, "E425", {"start": v(-24.27, -331.16) * mm, "end": v(-24.2, -331.08) * mm});
            skLineSegment(sketch, "E426", {"start": v(-24.2, -331.08) * mm, "end": v(-24.12, -331) * mm});
            skLineSegment(sketch, "E427", {"start": v(-24.12, -331) * mm, "end": v(-24.05, -330.91) * mm});
            skLineSegment(sketch, "E428", {"start": v(-24.05, -330.91) * mm, "end": v(-23.99, -330.82) * mm});
            skLineSegment(sketch, "E429", {"start": v(-23.99, -330.82) * mm, "end": v(-23.93, -330.73) * mm});
            skLineSegment(sketch, "E430", {"start": v(-23.93, -330.73) * mm, "end": v(-23.88, -330.63) * mm});
            skLineSegment(sketch, "E431", {"start": v(-23.88, -330.63) * mm, "end": v(-23.84, -330.52) * mm});
            skLineSegment(sketch, "E432", {"start": v(-23.84, -330.52) * mm, "end": v(-23.8, -330.42) * mm});
            skLineSegment(sketch, "E433", {"start": v(-23.8, -330.42) * mm, "end": v(-23.77, -330.31) * mm});
            skLineSegment(sketch, "E434", {"start": v(-23.77, -330.31) * mm, "end": v(-23.75, -330.2) * mm});
            skLineSegment(sketch, "E435", {"start": v(-23.75, -330.2) * mm, "end": v(-23.73, -330.1) * mm});
            skLineSegment(sketch, "E436", {"start": v(-23.73, -330.1) * mm, "end": v(-23.73, -329.99) * mm});
            skLineSegment(sketch, "E437", {"start": v(-23.73, -329.99) * mm, "end": v(-23.73, -329.87) * mm});
            skLineSegment(sketch, "E438", {"start": v(-23.73, -329.87) * mm, "end": v(-23.73, -329.76) * mm});
            skLineSegment(sketch, "E439", {"start": v(-23.73, -329.76) * mm, "end": v(-23.75, -329.65) * mm});
            skLineSegment(sketch, "E440", {"start": v(-23.75, -329.65) * mm, "end": v(-23.77, -329.55) * mm});
            skLineSegment(sketch, "E441", {"start": v(-23.77, -329.55) * mm, "end": v(-23.8, -329.44) * mm});
            skLineSegment(sketch, "E442", {"start": v(-23.8, -329.44) * mm, "end": v(-23.84, -329.34) * mm});
            skLineSegment(sketch, "E443", {"start": v(-23.84, -329.34) * mm, "end": v(-23.88, -329.23) * mm});
            skLineSegment(sketch, "E444", {"start": v(-23.88, -329.23) * mm, "end": v(-23.93, -329.13) * mm});
            skLineSegment(sketch, "E445", {"start": v(-23.93, -329.13) * mm, "end": v(-23.99, -329.04) * mm});
            skLineSegment(sketch, "E446", {"start": v(-23.99, -329.04) * mm, "end": v(-24.05, -328.95) * mm});
            skLineSegment(sketch, "E447", {"start": v(-24.05, -328.95) * mm, "end": v(-24.12, -328.86) * mm});
            skLineSegment(sketch, "E448", {"start": v(-24.12, -328.86) * mm, "end": v(-24.2, -328.78) * mm});
            skLineSegment(sketch, "E449", {"start": v(-24.2, -328.78) * mm, "end": v(-24.27, -328.7) * mm});
            skLineSegment(sketch, "E450", {"start": v(-24.27, -328.7) * mm, "end": v(-24.36, -328.63) * mm});
            skLineSegment(sketch, "E451", {"start": v(-24.36, -328.63) * mm, "end": v(-24.44, -328.57) * mm});
            skLineSegment(sketch, "E452", {"start": v(-24.44, -328.57) * mm, "end": v(-24.54, -328.5) * mm});
            skLineSegment(sketch, "E453", {"start": v(-24.54, -328.5) * mm, "end": v(-24.63, -328.45) * mm});
            skLineSegment(sketch, "E454", {"start": v(-24.63, -328.45) * mm, "end": v(-24.74, -328.4) * mm});
            skLineSegment(sketch, "E455", {"start": v(-24.74, -328.4) * mm, "end": v(-24.84, -328.37) * mm});
            skLineSegment(sketch, "E456", {"start": v(-24.84, -328.37) * mm, "end": v(-24.94, -328.33) * mm});
            skLineSegment(sketch, "E457", {"start": v(-24.94, -328.33) * mm, "end": v(-25.05, -328.3) * mm});
            skLineSegment(sketch, "E458", {"start": v(-25.05, -328.3) * mm, "end": v(-25.16, -328.29) * mm});
            skLineSegment(sketch, "E459", {"start": v(-25.16, -328.29) * mm, "end": v(-25.27, -328.28) * mm});
            skLineSegment(sketch, "E460", {"start": v(-25.27, -328.28) * mm, "end": v(-25.38, -328.27) * mm});
            skLineSegment(sketch, "E461", {"start": v(-25.38, -328.27) * mm, "end": v(-25.66, -328.27) * mm});
            skLineSegment(sketch, "E462", {"start": v(-32, -328.27) * mm, "end": v(-32.11, -328.28) * mm});
            skLineSegment(sketch, "E463", {"start": v(-32.11, -328.28) * mm, "end": v(-32.22, -328.29) * mm});
            skLineSegment(sketch, "E464", {"start": v(-32.22, -328.29) * mm, "end": v(-32.33, -328.3) * mm});
            skLineSegment(sketch, "E465", {"start": v(-32.33, -328.3) * mm, "end": v(-32.44, -328.33) * mm});
            skLineSegment(sketch, "E466", {"start": v(-32.44, -328.33) * mm, "end": v(-32.55, -328.37) * mm});
            skLineSegment(sketch, "E467", {"start": v(-32.55, -328.37) * mm, "end": v(-32.65, -328.4) * mm});
            skLineSegment(sketch, "E468", {"start": v(-32.65, -328.4) * mm, "end": v(-32.75, -328.45) * mm});
            skLineSegment(sketch, "E469", {"start": v(-32.75, -328.45) * mm, "end": v(-32.85, -328.5) * mm});
            skLineSegment(sketch, "E470", {"start": v(-32.85, -328.5) * mm, "end": v(-32.94, -328.57) * mm});
            skLineSegment(sketch, "E471", {"start": v(-32.94, -328.57) * mm, "end": v(-33.03, -328.63) * mm});
            skLineSegment(sketch, "E472", {"start": v(-33.03, -328.63) * mm, "end": v(-33.11, -328.7) * mm});
            skLineSegment(sketch, "E473", {"start": v(-33.11, -328.7) * mm, "end": v(-33.2, -328.78) * mm});
            skLineSegment(sketch, "E474", {"start": v(-33.2, -328.78) * mm, "end": v(-33.27, -328.86) * mm});
            skLineSegment(sketch, "E475", {"start": v(-33.27, -328.86) * mm, "end": v(-33.34, -328.95) * mm});
            skLineSegment(sketch, "E476", {"start": v(-33.34, -328.95) * mm, "end": v(-33.4, -329.04) * mm});
            skLineSegment(sketch, "E477", {"start": v(-33.4, -329.04) * mm, "end": v(-33.45, -329.13) * mm});
            skLineSegment(sketch, "E478", {"start": v(-33.45, -329.13) * mm, "end": v(-33.5, -329.23) * mm});
            skLineSegment(sketch, "E479", {"start": v(-33.5, -329.23) * mm, "end": v(-33.55, -329.34) * mm});
            skLineSegment(sketch, "E480", {"start": v(-33.55, -329.34) * mm, "end": v(-33.58, -329.44) * mm});
            skLineSegment(sketch, "E481", {"start": v(-33.58, -329.44) * mm, "end": v(-33.61, -329.55) * mm});
            skLineSegment(sketch, "E482", {"start": v(-33.61, -329.55) * mm, "end": v(-33.63, -329.65) * mm});
            skLineSegment(sketch, "E483", {"start": v(-33.63, -329.65) * mm, "end": v(-33.65, -329.76) * mm});
            skLineSegment(sketch, "E484", {"start": v(-33.65, -329.76) * mm, "end": v(-33.66, -329.87) * mm});
            skLineSegment(sketch, "E485", {"start": v(-33.66, -329.87) * mm, "end": v(-33.66, -329.99) * mm});
            skLineSegment(sketch, "E486", {"start": v(-33.66, -329.99) * mm, "end": v(-33.65, -330.1) * mm});
            skLineSegment(sketch, "E487", {"start": v(-33.65, -330.1) * mm, "end": v(-33.63, -330.2) * mm});
            skLineSegment(sketch, "E488", {"start": v(-33.63, -330.2) * mm, "end": v(-33.61, -330.31) * mm});
            skLineSegment(sketch, "E489", {"start": v(-33.61, -330.31) * mm, "end": v(-33.58, -330.42) * mm});
            skLineSegment(sketch, "E490", {"start": v(-33.58, -330.42) * mm, "end": v(-33.55, -330.52) * mm});
            skLineSegment(sketch, "E491", {"start": v(-33.55, -330.52) * mm, "end": v(-33.5, -330.63) * mm});
            skLineSegment(sketch, "E492", {"start": v(-33.5, -330.63) * mm, "end": v(-33.45, -330.73) * mm});
            skLineSegment(sketch, "E493", {"start": v(-33.45, -330.73) * mm, "end": v(-33.4, -330.82) * mm});
            skLineSegment(sketch, "E494", {"start": v(-33.4, -330.82) * mm, "end": v(-33.34, -330.91) * mm});
            skLineSegment(sketch, "E495", {"start": v(-33.34, -330.91) * mm, "end": v(-33.27, -331) * mm});
            skLineSegment(sketch, "E496", {"start": v(-33.27, -331) * mm, "end": v(-33.2, -331.08) * mm});
            skLineSegment(sketch, "E497", {"start": v(-33.2, -331.08) * mm, "end": v(-33.11, -331.16) * mm});
            skLineSegment(sketch, "E498", {"start": v(-33.11, -331.16) * mm, "end": v(-33.03, -331.23) * mm});
            skLineSegment(sketch, "E499", {"start": v(-33.03, -331.23) * mm, "end": v(-32.94, -331.3) * mm});
            skLineSegment(sketch, "E500", {"start": v(-32.94, -331.3) * mm, "end": v(-32.85, -331.35) * mm});
            skLineSegment(sketch, "E501", {"start": v(-32.85, -331.35) * mm, "end": v(-32.75, -331.4) * mm});
            skLineSegment(sketch, "E502", {"start": v(-32.75, -331.4) * mm, "end": v(-32.65, -331.45) * mm});
            skLineSegment(sketch, "E503", {"start": v(-32.65, -331.45) * mm, "end": v(-32.55, -331.5) * mm});
            skLineSegment(sketch, "E504", {"start": v(-32.55, -331.5) * mm, "end": v(-32.44, -331.53) * mm});
            skLineSegment(sketch, "E505", {"start": v(-32.44, -331.53) * mm, "end": v(-32.33, -331.55) * mm});
            skLineSegment(sketch, "E506", {"start": v(-32.33, -331.55) * mm, "end": v(-32.22, -331.57) * mm});
            skLineSegment(sketch, "E507", {"start": v(-32.22, -331.57) * mm, "end": v(-32.11, -331.58) * mm});
            skLineSegment(sketch, "E508", {"start": v(-32.11, -331.58) * mm, "end": v(-32, -331.59) * mm});
            skLineSegment(sketch, "E509", {"start": v(-25.66, -328.27) * mm, "end": v(-25.66, -322.76) * mm});
            skLineSegment(sketch, "E510", {"start": v(-25.66, -322.76) * mm, "end": v(-31.73, -322.76) * mm});
            skLineSegment(sketch, "E511", {"start": v(-31.73, -322.76) * mm, "end": v(-31.73, -328.27) * mm});
            skLineSegment(sketch, "E512", {"start": v(-20.25, -327.17) * mm, "end": v(-20.25, -322.76) * mm});
            skLineSegment(sketch, "E513", {"start": v(-20.25, -322.76) * mm, "end": v(-14.18, -322.76) * mm});
            skLineSegment(sketch, "E514", {"start": v(-14.18, -322.76) * mm, "end": v(-14.18, -327.17) * mm});
            skLineSegment(sketch, "E515", {"start": v(-20.53, -330.48) * mm, "end": v(-20.25, -330.48) * mm});
            skLineSegment(sketch, "E516", {"start": v(-13.9, -330.48) * mm, "end": v(-13.8, -330.48) * mm});
            skLineSegment(sketch, "E517", {"start": v(-13.8, -330.48) * mm, "end": v(-13.68, -330.47) * mm});
            skLineSegment(sketch, "E518", {"start": v(-13.68, -330.47) * mm, "end": v(-13.57, -330.45) * mm});
            skLineSegment(sketch, "E519", {"start": v(-13.57, -330.45) * mm, "end": v(-13.47, -330.42) * mm});
            skLineSegment(sketch, "E520", {"start": v(-13.47, -330.42) * mm, "end": v(-13.36, -330.4) * mm});
            skLineSegment(sketch, "E521", {"start": v(-13.36, -330.4) * mm, "end": v(-13.26, -330.35) * mm});
            skLineSegment(sketch, "E522", {"start": v(-13.26, -330.35) * mm, "end": v(-13.16, -330.3) * mm});
            skLineSegment(sketch, "E523", {"start": v(-13.16, -330.3) * mm, "end": v(-13.06, -330.25) * mm});
            skLineSegment(sketch, "E524", {"start": v(-13.06, -330.25) * mm, "end": v(-12.97, -330.2) * mm});
            skLineSegment(sketch, "E525", {"start": v(-12.97, -330.2) * mm, "end": v(-12.88, -330.13) * mm});
            skLineSegment(sketch, "E526", {"start": v(-12.88, -330.13) * mm, "end": v(-12.8, -330.05) * mm});
            skLineSegment(sketch, "E527", {"start": v(-12.8, -330.05) * mm, "end": v(-12.71, -329.98) * mm});
            skLineSegment(sketch, "E528", {"start": v(-12.71, -329.98) * mm, "end": v(-12.64, -329.9) * mm});
            skLineSegment(sketch, "E529", {"start": v(-12.64, -329.9) * mm, "end": v(-12.57, -329.8) * mm});
            skLineSegment(sketch, "E530", {"start": v(-12.57, -329.8) * mm, "end": v(-12.5, -329.72) * mm});
            skLineSegment(sketch, "E531", {"start": v(-12.5, -329.72) * mm, "end": v(-12.45, -329.62) * mm});
            skLineSegment(sketch, "E532", {"start": v(-12.45, -329.62) * mm, "end": v(-12.4, -329.52) * mm});
            skLineSegment(sketch, "E533", {"start": v(-12.4, -329.52) * mm, "end": v(-12.36, -329.42) * mm});
            skLineSegment(sketch, "E534", {"start": v(-12.36, -329.42) * mm, "end": v(-12.32, -329.32) * mm});
            skLineSegment(sketch, "E535", {"start": v(-12.32, -329.32) * mm, "end": v(-12.3, -329.21) * mm});
            skLineSegment(sketch, "E536", {"start": v(-12.3, -329.21) * mm, "end": v(-12.27, -329.1) * mm});
            skLineSegment(sketch, "E537", {"start": v(-12.27, -329.1) * mm, "end": v(-12.26, -329) * mm});
            skLineSegment(sketch, "E538", {"start": v(-12.26, -329) * mm, "end": v(-12.25, -328.88) * mm});
            skLineSegment(sketch, "E539", {"start": v(-12.25, -328.88) * mm, "end": v(-12.25, -328.77) * mm});
            skLineSegment(sketch, "E540", {"start": v(-12.25, -328.77) * mm, "end": v(-12.26, -328.66) * mm});
            skLineSegment(sketch, "E541", {"start": v(-12.26, -328.66) * mm, "end": v(-12.27, -328.55) * mm});
            skLineSegment(sketch, "E542", {"start": v(-12.27, -328.55) * mm, "end": v(-12.3, -328.44) * mm});
            skLineSegment(sketch, "E543", {"start": v(-12.3, -328.44) * mm, "end": v(-12.32, -328.34) * mm});
            skLineSegment(sketch, "E544", {"start": v(-12.32, -328.34) * mm, "end": v(-12.36, -328.23) * mm});
            skLineSegment(sketch, "E545", {"start": v(-12.36, -328.23) * mm, "end": v(-12.4, -328.13) * mm});
            skLineSegment(sketch, "E546", {"start": v(-12.4, -328.13) * mm, "end": v(-12.45, -328.03) * mm});
            skLineSegment(sketch, "E547", {"start": v(-12.45, -328.03) * mm, "end": v(-12.5, -327.94) * mm});
            skLineSegment(sketch, "E548", {"start": v(-12.5, -327.94) * mm, "end": v(-12.57, -327.84) * mm});
            skLineSegment(sketch, "E549", {"start": v(-12.57, -327.84) * mm, "end": v(-12.64, -327.76) * mm});
            skLineSegment(sketch, "E550", {"start": v(-12.64, -327.76) * mm, "end": v(-12.71, -327.68) * mm});
            skLineSegment(sketch, "E551", {"start": v(-12.71, -327.68) * mm, "end": v(-12.8, -327.6) * mm});
            skLineSegment(sketch, "E552", {"start": v(-12.8, -327.6) * mm, "end": v(-12.88, -327.53) * mm});
            skLineSegment(sketch, "E553", {"start": v(-12.88, -327.53) * mm, "end": v(-12.97, -327.46) * mm});
            skLineSegment(sketch, "E554", {"start": v(-12.97, -327.46) * mm, "end": v(-13.06, -327.4) * mm});
            skLineSegment(sketch, "E555", {"start": v(-13.06, -327.4) * mm, "end": v(-13.16, -327.35) * mm});
            skLineSegment(sketch, "E556", {"start": v(-13.16, -327.35) * mm, "end": v(-13.26, -327.3) * mm});
            skLineSegment(sketch, "E557", {"start": v(-13.26, -327.3) * mm, "end": v(-13.36, -327.26) * mm});
            skLineSegment(sketch, "E558", {"start": v(-13.36, -327.26) * mm, "end": v(-13.47, -327.23) * mm});
            skLineSegment(sketch, "E559", {"start": v(-13.47, -327.23) * mm, "end": v(-13.57, -327.2) * mm});
            skLineSegment(sketch, "E560", {"start": v(-13.57, -327.2) * mm, "end": v(-13.68, -327.19) * mm});
            skLineSegment(sketch, "E561", {"start": v(-13.68, -327.19) * mm, "end": v(-13.8, -327.17) * mm});
            skLineSegment(sketch, "E562", {"start": v(-13.8, -327.17) * mm, "end": v(-13.9, -327.17) * mm});
            skLineSegment(sketch, "E563", {"start": v(-13.9, -327.17) * mm, "end": v(-14.18, -327.17) * mm});
            skLineSegment(sketch, "E564", {"start": v(-20.53, -327.17) * mm, "end": v(-20.64, -327.17) * mm});
            skLineSegment(sketch, "E565", {"start": v(-20.64, -327.17) * mm, "end": v(-20.75, -327.19) * mm});
            skLineSegment(sketch, "E566", {"start": v(-20.75, -327.19) * mm, "end": v(-20.86, -327.2) * mm});
            skLineSegment(sketch, "E567", {"start": v(-20.86, -327.2) * mm, "end": v(-20.96, -327.23) * mm});
            skLineSegment(sketch, "E568", {"start": v(-20.96, -327.23) * mm, "end": v(-21.07, -327.26) * mm});
            skLineSegment(sketch, "E569", {"start": v(-21.07, -327.26) * mm, "end": v(-21.17, -327.3) * mm});
            skLineSegment(sketch, "E570", {"start": v(-21.17, -327.3) * mm, "end": v(-21.27, -327.35) * mm});
            skLineSegment(sketch, "E571", {"start": v(-21.27, -327.35) * mm, "end": v(-21.37, -327.4) * mm});
            skLineSegment(sketch, "E572", {"start": v(-21.37, -327.4) * mm, "end": v(-21.46, -327.46) * mm});
            skLineSegment(sketch, "E573", {"start": v(-21.46, -327.46) * mm, "end": v(-21.55, -327.53) * mm});
            skLineSegment(sketch, "E574", {"start": v(-21.55, -327.53) * mm, "end": v(-21.64, -327.6) * mm});
            skLineSegment(sketch, "E575", {"start": v(-21.64, -327.6) * mm, "end": v(-21.72, -327.68) * mm});
            skLineSegment(sketch, "E576", {"start": v(-21.72, -327.68) * mm, "end": v(-21.79, -327.76) * mm});
            skLineSegment(sketch, "E577", {"start": v(-21.79, -327.76) * mm, "end": v(-21.86, -327.84) * mm});
            skLineSegment(sketch, "E578", {"start": v(-21.86, -327.84) * mm, "end": v(-21.92, -327.94) * mm});
            skLineSegment(sketch, "E579", {"start": v(-21.92, -327.94) * mm, "end": v(-21.98, -328.03) * mm});
            skLineSegment(sketch, "E580", {"start": v(-21.98, -328.03) * mm, "end": v(-22.03, -328.13) * mm});
            skLineSegment(sketch, "E581", {"start": v(-22.03, -328.13) * mm, "end": v(-22.07, -328.23) * mm});
            skLineSegment(sketch, "E582", {"start": v(-22.07, -328.23) * mm, "end": v(-22.1, -328.34) * mm});
            skLineSegment(sketch, "E583", {"start": v(-22.1, -328.34) * mm, "end": v(-22.14, -328.44) * mm});
            skLineSegment(sketch, "E584", {"start": v(-22.14, -328.44) * mm, "end": v(-22.16, -328.55) * mm});
            skLineSegment(sketch, "E585", {"start": v(-22.16, -328.55) * mm, "end": v(-22.17, -328.66) * mm});
            skLineSegment(sketch, "E586", {"start": v(-22.17, -328.66) * mm, "end": v(-22.18, -328.77) * mm});
            skLineSegment(sketch, "E587", {"start": v(-22.18, -328.77) * mm, "end": v(-22.18, -328.88) * mm});
            skLineSegment(sketch, "E588", {"start": v(-22.18, -328.88) * mm, "end": v(-22.17, -329) * mm});
            skLineSegment(sketch, "E589", {"start": v(-22.17, -329) * mm, "end": v(-22.16, -329.1) * mm});
            skLineSegment(sketch, "E590", {"start": v(-22.16, -329.1) * mm, "end": v(-22.14, -329.21) * mm});
            skLineSegment(sketch, "E591", {"start": v(-22.14, -329.21) * mm, "end": v(-22.1, -329.32) * mm});
            skLineSegment(sketch, "E592", {"start": v(-22.1, -329.32) * mm, "end": v(-22.07, -329.42) * mm});
            skLineSegment(sketch, "E593", {"start": v(-22.07, -329.42) * mm, "end": v(-22.03, -329.52) * mm});
            skLineSegment(sketch, "E594", {"start": v(-22.03, -329.52) * mm, "end": v(-21.98, -329.62) * mm});
            skLineSegment(sketch, "E595", {"start": v(-21.98, -329.62) * mm, "end": v(-21.92, -329.72) * mm});
            skLineSegment(sketch, "E596", {"start": v(-21.92, -329.72) * mm, "end": v(-21.86, -329.8) * mm});
            skLineSegment(sketch, "E597", {"start": v(-21.86, -329.8) * mm, "end": v(-21.79, -329.9) * mm});
            skLineSegment(sketch, "E598", {"start": v(-21.79, -329.9) * mm, "end": v(-21.72, -329.98) * mm});
            skLineSegment(sketch, "E599", {"start": v(-21.72, -329.98) * mm, "end": v(-21.64, -330.05) * mm});
            skLineSegment(sketch, "E600", {"start": v(-21.64, -330.05) * mm, "end": v(-21.55, -330.13) * mm});
            skLineSegment(sketch, "E601", {"start": v(-21.55, -330.13) * mm, "end": v(-21.46, -330.2) * mm});
            skLineSegment(sketch, "E602", {"start": v(-21.46, -330.2) * mm, "end": v(-21.37, -330.25) * mm});
            skLineSegment(sketch, "E603", {"start": v(-21.37, -330.25) * mm, "end": v(-21.27, -330.3) * mm});
            skLineSegment(sketch, "E604", {"start": v(-21.27, -330.3) * mm, "end": v(-21.17, -330.35) * mm});
            skLineSegment(sketch, "E605", {"start": v(-21.17, -330.35) * mm, "end": v(-21.07, -330.4) * mm});
            skLineSegment(sketch, "E606", {"start": v(-21.07, -330.4) * mm, "end": v(-20.96, -330.42) * mm});
            skLineSegment(sketch, "E607", {"start": v(-20.96, -330.42) * mm, "end": v(-20.86, -330.45) * mm});
            skLineSegment(sketch, "E608", {"start": v(-20.86, -330.45) * mm, "end": v(-20.75, -330.47) * mm});
            skLineSegment(sketch, "E609", {"start": v(-20.75, -330.47) * mm, "end": v(-20.64, -330.48) * mm});
            skLineSegment(sketch, "E610", {"start": v(-20.64, -330.48) * mm, "end": v(-20.53, -330.48) * mm});
            skLineSegment(sketch, "E611", {"start": v(34.9, -336) * mm, "end": v(35.42, -336.26) * mm});
            skLineSegment(sketch, "E612", {"start": v(35.42, -336.26) * mm, "end": v(35.95, -336.5) * mm});
            skLineSegment(sketch, "E613", {"start": v(35.95, -336.5) * mm, "end": v(36.5, -336.69) * mm});
            skLineSegment(sketch, "E614", {"start": v(36.5, -336.69) * mm, "end": v(37.06, -336.85) * mm});
            skLineSegment(sketch, "E615", {"start": v(37.06, -336.85) * mm, "end": v(37.63, -336.97) * mm});
            skLineSegment(sketch, "E616", {"start": v(37.63, -336.97) * mm, "end": v(38.2, -337.05) * mm});
            skLineSegment(sketch, "E617", {"start": v(38.2, -337.05) * mm, "end": v(38.79, -337.1) * mm});
            skLineSegment(sketch, "E618", {"start": v(38.79, -337.1) * mm, "end": v(39.37, -337.1) * mm});
            skLineSegment(sketch, "E619", {"start": v(39.37, -337.1) * mm, "end": v(39.95, -337.07) * mm});
            skLineSegment(sketch, "E620", {"start": v(39.95, -337.07) * mm, "end": v(40.53, -337) * mm});
            skLineSegment(sketch, "E621", {"start": v(40.53, -337) * mm, "end": v(41.1, -336.9) * mm});
            skLineSegment(sketch, "E622", {"start": v(41.1, -336.9) * mm, "end": v(41.66, -336.75) * mm});
            skLineSegment(sketch, "E623", {"start": v(41.66, -336.75) * mm, "end": v(42.21, -336.56) * mm});
            skLineSegment(sketch, "E624", {"start": v(42.21, -336.56) * mm, "end": v(42.75, -336.35) * mm});
            skLineSegment(sketch, "E625", {"start": v(42.75, -336.35) * mm, "end": v(43.28, -336.1) * mm});
            skLineSegment(sketch, "E626", {"start": v(43.28, -336.1) * mm, "end": v(43.78, -335.8) * mm});
            skLineSegment(sketch, "E627", {"start": v(43.78, -335.8) * mm, "end": v(44.27, -335.48) * mm});
            skLineSegment(sketch, "E628", {"start": v(44.27, -335.48) * mm, "end": v(44.73, -335.13) * mm});
            skLineSegment(sketch, "E629", {"start": v(44.73, -335.13) * mm, "end": v(45.17, -334.75) * mm});
            skLineSegment(sketch, "E630", {"start": v(45.17, -334.75) * mm, "end": v(45.59, -334.34) * mm});
            skLineSegment(sketch, "E631", {"start": v(45.59, -334.34) * mm, "end": v(45.97, -333.9) * mm});
            skLineSegment(sketch, "E632", {"start": v(45.97, -333.9) * mm, "end": v(46.33, -333.45) * mm});
            skLineSegment(sketch, "E633", {"start": v(46.33, -333.45) * mm, "end": v(46.65, -332.97) * mm});
            skLineSegment(sketch, "E634", {"start": v(46.65, -332.97) * mm, "end": v(46.95, -332.46) * mm});
            skLineSegment(sketch, "E635", {"start": v(46.95, -332.46) * mm, "end": v(47.2, -331.94) * mm});
            skLineSegment(sketch, "E636", {"start": v(47.2, -331.94) * mm, "end": v(47.43, -331.4) * mm});
            skLineSegment(sketch, "E637", {"start": v(47.43, -331.4) * mm, "end": v(47.62, -330.85) * mm});
            skLineSegment(sketch, "E638", {"start": v(47.62, -330.85) * mm, "end": v(47.77, -330.3) * mm});
            skLineSegment(sketch, "E639", {"start": v(47.77, -330.3) * mm, "end": v(47.88, -329.72) * mm});
            skLineSegment(sketch, "E640", {"start": v(47.88, -329.72) * mm, "end": v(47.96, -329.15) * mm});
            skLineSegment(sketch, "E641", {"start": v(47.96, -329.15) * mm, "end": v(48, -328.57) * mm});
            skLineSegment(sketch, "E642", {"start": v(48, -328.57) * mm, "end": v(48, -327.98) * mm});
            skLineSegment(sketch, "E643", {"start": v(48, -327.98) * mm, "end": v(47.96, -327.4) * mm});
            skLineSegment(sketch, "E644", {"start": v(47.96, -327.4) * mm, "end": v(47.88, -326.83) * mm});
            skLineSegment(sketch, "E645", {"start": v(47.88, -326.83) * mm, "end": v(47.77, -326.26) * mm});
            skLineSegment(sketch, "E646", {"start": v(47.77, -326.26) * mm, "end": v(47.62, -325.7) * mm});
            skLineSegment(sketch, "E647", {"start": v(47.62, -325.7) * mm, "end": v(47.43, -325.14) * mm});
            skLineSegment(sketch, "E648", {"start": v(47.43, -325.14) * mm, "end": v(47.2, -324.6) * mm});
            skLineSegment(sketch, "E649", {"start": v(47.2, -324.6) * mm, "end": v(46.95, -324.09) * mm});
            skLineSegment(sketch, "E650", {"start": v(46.95, -324.09) * mm, "end": v(46.65, -323.58) * mm});
            skLineSegment(sketch, "E651", {"start": v(46.65, -323.58) * mm, "end": v(46.33, -323.1) * mm});
            skLineSegment(sketch, "E652", {"start": v(46.33, -323.1) * mm, "end": v(45.97, -322.64) * mm});
            skLineSegment(sketch, "E653", {"start": v(45.97, -322.64) * mm, "end": v(45.59, -322.2) * mm});
            skLineSegment(sketch, "E654", {"start": v(45.59, -322.2) * mm, "end": v(45.17, -321.8) * mm});
            skLineSegment(sketch, "E655", {"start": v(45.17, -321.8) * mm, "end": v(44.73, -321.42) * mm});
            skLineSegment(sketch, "E656", {"start": v(44.73, -321.42) * mm, "end": v(44.27, -321.06) * mm});
            skLineSegment(sketch, "E657", {"start": v(44.27, -321.06) * mm, "end": v(43.78, -320.74) * mm});
            skLineSegment(sketch, "E658", {"start": v(43.78, -320.74) * mm, "end": v(43.28, -320.46) * mm});
            skLineSegment(sketch, "E659", {"start": v(43.28, -320.46) * mm, "end": v(42.75, -320.2) * mm});
            skLineSegment(sketch, "E660", {"start": v(42.75, -320.2) * mm, "end": v(42.21, -319.99) * mm});
            skLineSegment(sketch, "E661", {"start": v(42.21, -319.99) * mm, "end": v(41.66, -319.8) * mm});
            skLineSegment(sketch, "E662", {"start": v(41.66, -319.8) * mm, "end": v(41.1, -319.66) * mm});
            skLineSegment(sketch, "E663", {"start": v(41.1, -319.66) * mm, "end": v(40.53, -319.55) * mm});
            skLineSegment(sketch, "E664", {"start": v(40.53, -319.55) * mm, "end": v(39.95, -319.48) * mm});
            skLineSegment(sketch, "E665", {"start": v(39.95, -319.48) * mm, "end": v(39.37, -319.45) * mm});
            skLineSegment(sketch, "E666", {"start": v(39.37, -319.45) * mm, "end": v(38.79, -319.45) * mm});
            skLineSegment(sketch, "E667", {"start": v(38.79, -319.45) * mm, "end": v(38.2, -319.5) * mm});
            skLineSegment(sketch, "E668", {"start": v(38.2, -319.5) * mm, "end": v(37.63, -319.58) * mm});
            skLineSegment(sketch, "E669", {"start": v(37.63, -319.58) * mm, "end": v(37.06, -319.7) * mm});
            skLineSegment(sketch, "E670", {"start": v(37.06, -319.7) * mm, "end": v(36.5, -319.86) * mm});
            skLineSegment(sketch, "E671", {"start": v(36.5, -319.86) * mm, "end": v(35.95, -320.06) * mm});
            skLineSegment(sketch, "E672", {"start": v(35.95, -320.06) * mm, "end": v(35.42, -320.29) * mm});
            skLineSegment(sketch, "E673", {"start": v(35.42, -320.29) * mm, "end": v(34.9, -320.55) * mm});
            skLineSegment(sketch, "E674", {"start": v(25.66, -329.38) * mm, "end": v(25.66, -333.8) * mm});
            skLineSegment(sketch, "E675", {"start": v(25.66, -333.8) * mm, "end": v(31.73, -333.8) * mm});
            skLineSegment(sketch, "E676", {"start": v(31.73, -333.8) * mm, "end": v(31.73, -329.38) * mm});
            skLineSegment(sketch, "E677", {"start": v(2.7, -331.59) * mm, "end": v(2.7, -333.8) * mm});
            skLineSegment(sketch, "E678", {"start": v(2.7, -333.8) * mm, "end": v(8.77, -333.8) * mm});
            skLineSegment(sketch, "E679", {"start": v(8.77, -333.8) * mm, "end": v(8.77, -331.59) * mm});
            skLineSegment(sketch, "E680", {"start": v(20.25, -330.48) * mm, "end": v(20.25, -333.8) * mm});
            skLineSegment(sketch, "E681", {"start": v(20.25, -333.8) * mm, "end": v(14.18, -333.8) * mm});
            skLineSegment(sketch, "E682", {"start": v(14.18, -333.8) * mm, "end": v(14.18, -330.48) * mm});
            skLineSegment(sketch, "E683", {"start": v(25.93, -336) * mm, "end": v(25.93, -337.65) * mm});
            skLineSegment(sketch, "E684", {"start": v(25.93, -337.65) * mm, "end": v(31.45, -337.65) * mm});
            skLineSegment(sketch, "E685", {"start": v(31.45, -337.65) * mm, "end": v(31.45, -336) * mm});
            skLineSegment(sketch, "E686", {"start": v(-8.5, -336) * mm, "end": v(-8.5, -337.65) * mm});
            skLineSegment(sketch, "E687", {"start": v(-8.5, -337.65) * mm, "end": v(-2.98, -337.65) * mm});
            skLineSegment(sketch, "E688", {"start": v(-2.98, -337.65) * mm, "end": v(-2.98, -336) * mm});
            skLineSegment(sketch, "E689", {"start": v(2.98, -336) * mm, "end": v(2.98, -337.65) * mm});
            skLineSegment(sketch, "E690", {"start": v(2.98, -337.65) * mm, "end": v(8.5, -337.65) * mm});
            skLineSegment(sketch, "E691", {"start": v(8.5, -337.65) * mm, "end": v(8.5, -336) * mm});
            skLineSegment(sketch, "E692", {"start": v(14.46, -336) * mm, "end": v(14.46, -337.65) * mm});
            skLineSegment(sketch, "E693", {"start": v(14.46, -337.65) * mm, "end": v(19.97, -337.65) * mm});
            skLineSegment(sketch, "E694", {"start": v(19.97, -337.65) * mm, "end": v(19.97, -336) * mm});
            skLineSegment(sketch, "E695", {"start": v(25.38, -329.38) * mm, "end": v(25.66, -329.38) * mm});
            skLineSegment(sketch, "E696", {"start": v(32, -329.38) * mm, "end": v(32.11, -329.37) * mm});
            skLineSegment(sketch, "E697", {"start": v(32.11, -329.37) * mm, "end": v(32.22, -329.36) * mm});
            skLineSegment(sketch, "E698", {"start": v(32.22, -329.36) * mm, "end": v(32.33, -329.35) * mm});
            skLineSegment(sketch, "E699", {"start": v(32.33, -329.35) * mm, "end": v(32.44, -329.32) * mm});
            skLineSegment(sketch, "E700", {"start": v(32.44, -329.32) * mm, "end": v(32.55, -329.29) * mm});
            skLineSegment(sketch, "E701", {"start": v(32.55, -329.29) * mm, "end": v(32.65, -329.25) * mm});
            skLineSegment(sketch, "E702", {"start": v(32.65, -329.25) * mm, "end": v(32.75, -329.2) * mm});
            skLineSegment(sketch, "E703", {"start": v(32.75, -329.2) * mm, "end": v(32.85, -329.15) * mm});
            skLineSegment(sketch, "E704", {"start": v(32.85, -329.15) * mm, "end": v(32.94, -329.09) * mm});
            skLineSegment(sketch, "E705", {"start": v(32.94, -329.09) * mm, "end": v(33.03, -329.02) * mm});
            skLineSegment(sketch, "E706", {"start": v(33.03, -329.02) * mm, "end": v(33.11, -328.95) * mm});
            skLineSegment(sketch, "E707", {"start": v(33.11, -328.95) * mm, "end": v(33.2, -328.87) * mm});
            skLineSegment(sketch, "E708", {"start": v(33.2, -328.87) * mm, "end": v(33.27, -328.8) * mm});
            skLineSegment(sketch, "E709", {"start": v(33.27, -328.8) * mm, "end": v(33.34, -328.7) * mm});
            skLineSegment(sketch, "E710", {"start": v(33.34, -328.7) * mm, "end": v(33.4, -328.61) * mm});
            skLineSegment(sketch, "E711", {"start": v(33.4, -328.61) * mm, "end": v(33.45, -328.52) * mm});
            skLineSegment(sketch, "E712", {"start": v(33.45, -328.52) * mm, "end": v(33.5, -328.42) * mm});
            skLineSegment(sketch, "E713", {"start": v(33.5, -328.42) * mm, "end": v(33.55, -328.32) * mm});
            skLineSegment(sketch, "E714", {"start": v(33.55, -328.32) * mm, "end": v(33.58, -328.21) * mm});
            skLineSegment(sketch, "E715", {"start": v(33.58, -328.21) * mm, "end": v(33.61, -328.1) * mm});
            skLineSegment(sketch, "E716", {"start": v(33.61, -328.1) * mm, "end": v(33.63, -328) * mm});
            skLineSegment(sketch, "E717", {"start": v(33.63, -328) * mm, "end": v(33.65, -327.89) * mm});
            skLineSegment(sketch, "E718", {"start": v(33.65, -327.89) * mm, "end": v(33.66, -327.78) * mm});
            skLineSegment(sketch, "E719", {"start": v(33.66, -327.78) * mm, "end": v(33.66, -327.67) * mm});
            skLineSegment(sketch, "E720", {"start": v(33.66, -327.67) * mm, "end": v(33.65, -327.56) * mm});
            skLineSegment(sketch, "E721", {"start": v(33.65, -327.56) * mm, "end": v(33.63, -327.45) * mm});
            skLineSegment(sketch, "E722", {"start": v(33.63, -327.45) * mm, "end": v(33.61, -327.34) * mm});
            skLineSegment(sketch, "E723", {"start": v(33.61, -327.34) * mm, "end": v(33.58, -327.23) * mm});
            skLineSegment(sketch, "E724", {"start": v(33.58, -327.23) * mm, "end": v(33.55, -327.13) * mm});
            skLineSegment(sketch, "E725", {"start": v(33.55, -327.13) * mm, "end": v(33.5, -327.03) * mm});
            skLineSegment(sketch, "E726", {"start": v(33.5, -327.03) * mm, "end": v(33.45, -326.93) * mm});
            skLineSegment(sketch, "E727", {"start": v(33.45, -326.93) * mm, "end": v(33.4, -326.83) * mm});
            skLineSegment(sketch, "E728", {"start": v(33.4, -326.83) * mm, "end": v(33.34, -326.74) * mm});
            skLineSegment(sketch, "E729", {"start": v(33.34, -326.74) * mm, "end": v(33.27, -326.65) * mm});
            skLineSegment(sketch, "E730", {"start": v(33.27, -326.65) * mm, "end": v(33.2, -326.57) * mm});
            skLineSegment(sketch, "E731", {"start": v(33.2, -326.57) * mm, "end": v(33.11, -326.5) * mm});
            skLineSegment(sketch, "E732", {"start": v(33.11, -326.5) * mm, "end": v(33.03, -326.42) * mm});
            skLineSegment(sketch, "E733", {"start": v(33.03, -326.42) * mm, "end": v(32.94, -326.36) * mm});
            skLineSegment(sketch, "E734", {"start": v(32.94, -326.36) * mm, "end": v(32.85, -326.3) * mm});
            skLineSegment(sketch, "E735", {"start": v(32.85, -326.3) * mm, "end": v(32.75, -326.25) * mm});
            skLineSegment(sketch, "E736", {"start": v(32.75, -326.25) * mm, "end": v(32.65, -326.2) * mm});
            skLineSegment(sketch, "E737", {"start": v(32.65, -326.2) * mm, "end": v(32.55, -326.16) * mm});
            skLineSegment(sketch, "E738", {"start": v(32.55, -326.16) * mm, "end": v(32.44, -326.13) * mm});
            skLineSegment(sketch, "E739", {"start": v(32.44, -326.13) * mm, "end": v(32.33, -326.1) * mm});
            skLineSegment(sketch, "E740", {"start": v(32.33, -326.1) * mm, "end": v(32.22, -326.08) * mm});
            skLineSegment(sketch, "E741", {"start": v(32.22, -326.08) * mm, "end": v(32.11, -326.07) * mm});
            skLineSegment(sketch, "E742", {"start": v(32.11, -326.07) * mm, "end": v(32, -326.07) * mm});
            skLineSegment(sketch, "E743", {"start": v(32, -326.07) * mm, "end": v(31.73, -326.07) * mm});
            skLineSegment(sketch, "E744", {"start": v(25.38, -326.07) * mm, "end": v(25.27, -326.07) * mm});
            skLineSegment(sketch, "E745", {"start": v(25.27, -326.07) * mm, "end": v(25.16, -326.08) * mm});
            skLineSegment(sketch, "E746", {"start": v(25.16, -326.08) * mm, "end": v(25.05, -326.1) * mm});
            skLineSegment(sketch, "E747", {"start": v(25.05, -326.1) * mm, "end": v(24.94, -326.13) * mm});
            skLineSegment(sketch, "E748", {"start": v(24.94, -326.13) * mm, "end": v(24.84, -326.16) * mm});
            skLineSegment(sketch, "E749", {"start": v(24.84, -326.16) * mm, "end": v(24.74, -326.2) * mm});
            skLineSegment(sketch, "E750", {"start": v(24.74, -326.2) * mm, "end": v(24.63, -326.25) * mm});
            skLineSegment(sketch, "E751", {"start": v(24.63, -326.25) * mm, "end": v(24.54, -326.3) * mm});
            skLineSegment(sketch, "E752", {"start": v(24.54, -326.3) * mm, "end": v(24.44, -326.36) * mm});
            skLineSegment(sketch, "E753", {"start": v(24.44, -326.36) * mm, "end": v(24.36, -326.42) * mm});
            skLineSegment(sketch, "E754", {"start": v(24.36, -326.42) * mm, "end": v(24.27, -326.5) * mm});
            skLineSegment(sketch, "E755", {"start": v(24.27, -326.5) * mm, "end": v(24.2, -326.57) * mm});
            skLineSegment(sketch, "E756", {"start": v(24.2, -326.57) * mm, "end": v(24.12, -326.65) * mm});
            skLineSegment(sketch, "E757", {"start": v(24.12, -326.65) * mm, "end": v(24.05, -326.74) * mm});
            skLineSegment(sketch, "E758", {"start": v(24.05, -326.74) * mm, "end": v(23.99, -326.83) * mm});
            skLineSegment(sketch, "E759", {"start": v(23.99, -326.83) * mm, "end": v(23.93, -326.93) * mm});
            skLineSegment(sketch, "E760", {"start": v(23.93, -326.93) * mm, "end": v(23.88, -327.03) * mm});
            skLineSegment(sketch, "E761", {"start": v(23.88, -327.03) * mm, "end": v(23.84, -327.13) * mm});
            skLineSegment(sketch, "E762", {"start": v(23.84, -327.13) * mm, "end": v(23.8, -327.23) * mm});
            skLineSegment(sketch, "E763", {"start": v(23.8, -327.23) * mm, "end": v(23.77, -327.34) * mm});
            skLineSegment(sketch, "E764", {"start": v(23.77, -327.34) * mm, "end": v(23.75, -327.45) * mm});
            skLineSegment(sketch, "E765", {"start": v(23.75, -327.45) * mm, "end": v(23.73, -327.56) * mm});
            skLineSegment(sketch, "E766", {"start": v(23.73, -327.56) * mm, "end": v(23.73, -327.67) * mm});
            skLineSegment(sketch, "E767", {"start": v(23.73, -327.67) * mm, "end": v(23.73, -327.78) * mm});
            skLineSegment(sketch, "E768", {"start": v(23.73, -327.78) * mm, "end": v(23.73, -327.89) * mm});
            skLineSegment(sketch, "E769", {"start": v(23.73, -327.89) * mm, "end": v(23.75, -328) * mm});
            skLineSegment(sketch, "E770", {"start": v(23.75, -328) * mm, "end": v(23.77, -328.1) * mm});
            skLineSegment(sketch, "E771", {"start": v(23.77, -328.1) * mm, "end": v(23.8, -328.21) * mm});
            skLineSegment(sketch, "E772", {"start": v(23.8, -328.21) * mm, "end": v(23.84, -328.32) * mm});
            skLineSegment(sketch, "E773", {"start": v(23.84, -328.32) * mm, "end": v(23.88, -328.42) * mm});
            skLineSegment(sketch, "E774", {"start": v(23.88, -328.42) * mm, "end": v(23.93, -328.52) * mm});
            skLineSegment(sketch, "E775", {"start": v(23.93, -328.52) * mm, "end": v(23.99, -328.61) * mm});
            skLineSegment(sketch, "E776", {"start": v(23.99, -328.61) * mm, "end": v(24.05, -328.7) * mm});
            skLineSegment(sketch, "E777", {"start": v(24.05, -328.7) * mm, "end": v(24.12, -328.8) * mm});
            skLineSegment(sketch, "E778", {"start": v(24.12, -328.8) * mm, "end": v(24.2, -328.87) * mm});
            skLineSegment(sketch, "E779", {"start": v(24.2, -328.87) * mm, "end": v(24.27, -328.95) * mm});
            skLineSegment(sketch, "E780", {"start": v(24.27, -328.95) * mm, "end": v(24.36, -329.02) * mm});
            skLineSegment(sketch, "E781", {"start": v(24.36, -329.02) * mm, "end": v(24.44, -329.09) * mm});
            skLineSegment(sketch, "E782", {"start": v(24.44, -329.09) * mm, "end": v(24.54, -329.15) * mm});
            skLineSegment(sketch, "E783", {"start": v(24.54, -329.15) * mm, "end": v(24.63, -329.2) * mm});
            skLineSegment(sketch, "E784", {"start": v(24.63, -329.2) * mm, "end": v(24.74, -329.25) * mm});
            skLineSegment(sketch, "E785", {"start": v(24.74, -329.25) * mm, "end": v(24.84, -329.29) * mm});
            skLineSegment(sketch, "E786", {"start": v(24.84, -329.29) * mm, "end": v(24.94, -329.32) * mm});
            skLineSegment(sketch, "E787", {"start": v(24.94, -329.32) * mm, "end": v(25.05, -329.35) * mm});
            skLineSegment(sketch, "E788", {"start": v(25.05, -329.35) * mm, "end": v(25.16, -329.36) * mm});
            skLineSegment(sketch, "E789", {"start": v(25.16, -329.36) * mm, "end": v(25.27, -329.37) * mm});
            skLineSegment(sketch, "E790", {"start": v(25.27, -329.37) * mm, "end": v(25.38, -329.38) * mm});
            skLineSegment(sketch, "E791", {"start": v(31.73, -326.07) * mm, "end": v(31.73, -322.76) * mm});
            skLineSegment(sketch, "E792", {"start": v(31.73, -322.76) * mm, "end": v(25.66, -322.76) * mm});
            skLineSegment(sketch, "E793", {"start": v(25.66, -322.76) * mm, "end": v(25.66, -326.07) * mm});
            skLineSegment(sketch, "E794", {"start": v(-5.74, -329.38) * mm, "end": v(-5.74, -326.07) * mm});
            skLineSegment(sketch, "E795", {"start": v(17.22, -330.48) * mm, "end": v(17.22, -327.17) * mm});
            skLineSegment(sketch, "E796", {"start": v(2.43, -331.59) * mm, "end": v(2.7, -331.59) * mm});
            skLineSegment(sketch, "E797", {"start": v(9.05, -331.59) * mm, "end": v(9.16, -331.58) * mm});
            skLineSegment(sketch, "E798", {"start": v(9.16, -331.58) * mm, "end": v(9.27, -331.57) * mm});
            skLineSegment(sketch, "E799", {"start": v(9.27, -331.57) * mm, "end": v(9.38, -331.55) * mm});
            skLineSegment(sketch, "E800", {"start": v(9.38, -331.55) * mm, "end": v(9.49, -331.53) * mm});
            skLineSegment(sketch, "E801", {"start": v(9.49, -331.53) * mm, "end": v(9.6, -331.5) * mm});
            skLineSegment(sketch, "E802", {"start": v(9.6, -331.5) * mm, "end": v(9.7, -331.45) * mm});
            skLineSegment(sketch, "E803", {"start": v(9.7, -331.45) * mm, "end": v(9.8, -331.4) * mm});
            skLineSegment(sketch, "E804", {"start": v(9.8, -331.4) * mm, "end": v(9.9, -331.35) * mm});
            skLineSegment(sketch, "E805", {"start": v(9.9, -331.35) * mm, "end": v(9.99, -331.3) * mm});
            skLineSegment(sketch, "E806", {"start": v(9.99, -331.3) * mm, "end": v(10.07, -331.23) * mm});
            skLineSegment(sketch, "E807", {"start": v(10.07, -331.23) * mm, "end": v(10.16, -331.16) * mm});
            skLineSegment(sketch, "E808", {"start": v(10.16, -331.16) * mm, "end": v(10.24, -331.08) * mm});
            skLineSegment(sketch, "E809", {"start": v(10.24, -331.08) * mm, "end": v(10.31, -331) * mm});
            skLineSegment(sketch, "E810", {"start": v(10.31, -331) * mm, "end": v(10.38, -330.91) * mm});
            skLineSegment(sketch, "E811", {"start": v(10.38, -330.91) * mm, "end": v(10.44, -330.82) * mm});
            skLineSegment(sketch, "E812", {"start": v(10.44, -330.82) * mm, "end": v(10.5, -330.73) * mm});
            skLineSegment(sketch, "E813", {"start": v(10.5, -330.73) * mm, "end": v(10.55, -330.63) * mm});
            skLineSegment(sketch, "E814", {"start": v(10.55, -330.63) * mm, "end": v(10.6, -330.52) * mm});
            skLineSegment(sketch, "E815", {"start": v(10.6, -330.52) * mm, "end": v(10.63, -330.42) * mm});
            skLineSegment(sketch, "E816", {"start": v(10.63, -330.42) * mm, "end": v(10.66, -330.31) * mm});
            skLineSegment(sketch, "E817", {"start": v(10.66, -330.31) * mm, "end": v(10.68, -330.2) * mm});
            skLineSegment(sketch, "E818", {"start": v(10.68, -330.2) * mm, "end": v(10.7, -330.1) * mm});
            skLineSegment(sketch, "E819", {"start": v(10.7, -330.1) * mm, "end": v(10.7, -329.99) * mm});
            skLineSegment(sketch, "E820", {"start": v(10.7, -329.99) * mm, "end": v(10.7, -329.87) * mm});
            skLineSegment(sketch, "E821", {"start": v(10.7, -329.87) * mm, "end": v(10.7, -329.76) * mm});
            skLineSegment(sketch, "E822", {"start": v(10.7, -329.76) * mm, "end": v(10.68, -329.65) * mm});
            skLineSegment(sketch, "E823", {"start": v(10.68, -329.65) * mm, "end": v(10.66, -329.55) * mm});
            skLineSegment(sketch, "E824", {"start": v(10.66, -329.55) * mm, "end": v(10.63, -329.44) * mm});
            skLineSegment(sketch, "E825", {"start": v(10.63, -329.44) * mm, "end": v(10.6, -329.34) * mm});
            skLineSegment(sketch, "E826", {"start": v(10.6, -329.34) * mm, "end": v(10.55, -329.23) * mm});
            skLineSegment(sketch, "E827", {"start": v(10.55, -329.23) * mm, "end": v(10.5, -329.13) * mm});
            skLineSegment(sketch, "E828", {"start": v(10.5, -329.13) * mm, "end": v(10.44, -329.04) * mm});
            skLineSegment(sketch, "E829", {"start": v(10.44, -329.04) * mm, "end": v(10.38, -328.95) * mm});
            skLineSegment(sketch, "E830", {"start": v(10.38, -328.95) * mm, "end": v(10.31, -328.86) * mm});
            skLineSegment(sketch, "E831", {"start": v(10.31, -328.86) * mm, "end": v(10.24, -328.78) * mm});
            skLineSegment(sketch, "E832", {"start": v(10.24, -328.78) * mm, "end": v(10.16, -328.7) * mm});
            skLineSegment(sketch, "E833", {"start": v(10.16, -328.7) * mm, "end": v(10.07, -328.63) * mm});
            skLineSegment(sketch, "E834", {"start": v(10.07, -328.63) * mm, "end": v(9.99, -328.57) * mm});
            skLineSegment(sketch, "E835", {"start": v(9.99, -328.57) * mm, "end": v(9.9, -328.5) * mm});
            skLineSegment(sketch, "E836", {"start": v(9.9, -328.5) * mm, "end": v(9.8, -328.45) * mm});
            skLineSegment(sketch, "E837", {"start": v(9.8, -328.45) * mm, "end": v(9.7, -328.4) * mm});
            skLineSegment(sketch, "E838", {"start": v(9.7, -328.4) * mm, "end": v(9.6, -328.37) * mm});
            skLineSegment(sketch, "E839", {"start": v(9.6, -328.37) * mm, "end": v(9.49, -328.33) * mm});
            skLineSegment(sketch, "E840", {"start": v(9.49, -328.33) * mm, "end": v(9.38, -328.3) * mm});
            skLineSegment(sketch, "E841", {"start": v(9.38, -328.3) * mm, "end": v(9.27, -328.29) * mm});
            skLineSegment(sketch, "E842", {"start": v(9.27, -328.29) * mm, "end": v(9.16, -328.28) * mm});
            skLineSegment(sketch, "E843", {"start": v(9.16, -328.28) * mm, "end": v(9.05, -328.27) * mm});
            skLineSegment(sketch, "E844", {"start": v(9.05, -328.27) * mm, "end": v(8.77, -328.27) * mm});
            skLineSegment(sketch, "E845", {"start": v(2.43, -328.27) * mm, "end": v(2.32, -328.28) * mm});
            skLineSegment(sketch, "E846", {"start": v(2.32, -328.28) * mm, "end": v(2.2, -328.29) * mm});
            skLineSegment(sketch, "E847", {"start": v(2.2, -328.29) * mm, "end": v(2.1, -328.3) * mm});
            skLineSegment(sketch, "E848", {"start": v(2.1, -328.3) * mm, "end": v(2, -328.33) * mm});
            skLineSegment(sketch, "E849", {"start": v(2, -328.33) * mm, "end": v(1.88, -328.37) * mm});
            skLineSegment(sketch, "E850", {"start": v(1.88, -328.37) * mm, "end": v(1.78, -328.4) * mm});
            skLineSegment(sketch, "E851", {"start": v(1.78, -328.4) * mm, "end": v(1.68, -328.45) * mm});
            skLineSegment(sketch, "E852", {"start": v(1.68, -328.45) * mm, "end": v(1.58, -328.5) * mm});
            skLineSegment(sketch, "E853", {"start": v(1.58, -328.5) * mm, "end": v(1.5, -328.57) * mm});
            skLineSegment(sketch, "E854", {"start": v(1.5, -328.57) * mm, "end": v(1.4, -328.63) * mm});
            skLineSegment(sketch, "E855", {"start": v(1.4, -328.63) * mm, "end": v(1.32, -328.7) * mm});
            skLineSegment(sketch, "E856", {"start": v(1.32, -328.7) * mm, "end": v(1.24, -328.78) * mm});
            skLineSegment(sketch, "E857", {"start": v(1.24, -328.78) * mm, "end": v(1.16, -328.86) * mm});
            skLineSegment(sketch, "E858", {"start": v(1.16, -328.86) * mm, "end": v(1.1, -328.95) * mm});
            skLineSegment(sketch, "E859", {"start": v(1.1, -328.95) * mm, "end": v(1.03, -329.04) * mm});
            skLineSegment(sketch, "E860", {"start": v(1.03, -329.04) * mm, "end": v(0.98, -329.13) * mm});
            skLineSegment(sketch, "E861", {"start": v(0.98, -329.13) * mm, "end": v(0.93, -329.23) * mm});
            skLineSegment(sketch, "E862", {"start": v(0.93, -329.23) * mm, "end": v(0.88, -329.34) * mm});
            skLineSegment(sketch, "E863", {"start": v(0.88, -329.34) * mm, "end": v(0.85, -329.44) * mm});
            skLineSegment(sketch, "E864", {"start": v(0.85, -329.44) * mm, "end": v(0.82, -329.55) * mm});
            skLineSegment(sketch, "E865", {"start": v(0.82, -329.55) * mm, "end": v(0.8, -329.65) * mm});
            skLineSegment(sketch, "E866", {"start": v(0.8, -329.65) * mm, "end": v(0.78, -329.76) * mm});
            skLineSegment(sketch, "E867", {"start": v(0.78, -329.76) * mm, "end": v(0.77, -329.87) * mm});
            skLineSegment(sketch, "E868", {"start": v(0.77, -329.87) * mm, "end": v(0.77, -329.99) * mm});
            skLineSegment(sketch, "E869", {"start": v(0.77, -329.99) * mm, "end": v(0.78, -330.1) * mm});
            skLineSegment(sketch, "E870", {"start": v(0.78, -330.1) * mm, "end": v(0.8, -330.2) * mm});
            skLineSegment(sketch, "E871", {"start": v(0.8, -330.2) * mm, "end": v(0.82, -330.31) * mm});
            skLineSegment(sketch, "E872", {"start": v(0.82, -330.31) * mm, "end": v(0.85, -330.42) * mm});
            skLineSegment(sketch, "E873", {"start": v(0.85, -330.42) * mm, "end": v(0.88, -330.52) * mm});
            skLineSegment(sketch, "E874", {"start": v(0.88, -330.52) * mm, "end": v(0.93, -330.63) * mm});
            skLineSegment(sketch, "E875", {"start": v(0.93, -330.63) * mm, "end": v(0.98, -330.73) * mm});
            skLineSegment(sketch, "E876", {"start": v(0.98, -330.73) * mm, "end": v(1.03, -330.82) * mm});
            skLineSegment(sketch, "E877", {"start": v(1.03, -330.82) * mm, "end": v(1.1, -330.91) * mm});
            skLineSegment(sketch, "E878", {"start": v(1.1, -330.91) * mm, "end": v(1.16, -331) * mm});
            skLineSegment(sketch, "E879", {"start": v(1.16, -331) * mm, "end": v(1.24, -331.08) * mm});
            skLineSegment(sketch, "E880", {"start": v(1.24, -331.08) * mm, "end": v(1.32, -331.16) * mm});
            skLineSegment(sketch, "E881", {"start": v(1.32, -331.16) * mm, "end": v(1.4, -331.23) * mm});
            skLineSegment(sketch, "E882", {"start": v(1.4, -331.23) * mm, "end": v(1.5, -331.3) * mm});
            skLineSegment(sketch, "E883", {"start": v(1.5, -331.3) * mm, "end": v(1.58, -331.35) * mm});
            skLineSegment(sketch, "E884", {"start": v(1.58, -331.35) * mm, "end": v(1.68, -331.4) * mm});
            skLineSegment(sketch, "E885", {"start": v(1.68, -331.4) * mm, "end": v(1.78, -331.45) * mm});
            skLineSegment(sketch, "E886", {"start": v(1.78, -331.45) * mm, "end": v(1.88, -331.5) * mm});
            skLineSegment(sketch, "E887", {"start": v(1.88, -331.5) * mm, "end": v(2, -331.53) * mm});
            skLineSegment(sketch, "E888", {"start": v(2, -331.53) * mm, "end": v(2.1, -331.55) * mm});
            skLineSegment(sketch, "E889", {"start": v(2.1, -331.55) * mm, "end": v(2.2, -331.57) * mm});
            skLineSegment(sketch, "E890", {"start": v(2.2, -331.57) * mm, "end": v(2.32, -331.58) * mm});
            skLineSegment(sketch, "E891", {"start": v(2.32, -331.58) * mm, "end": v(2.43, -331.59) * mm});
            skLineSegment(sketch, "E892", {"start": v(5.74, -331.59) * mm, "end": v(5.74, -328.27) * mm});
            skLineSegment(sketch, "E893", {"start": v(8.77, -328.27) * mm, "end": v(8.77, -322.76) * mm});
            skLineSegment(sketch, "E894", {"start": v(8.77, -322.76) * mm, "end": v(2.7, -322.76) * mm});
            skLineSegment(sketch, "E895", {"start": v(2.7, -322.76) * mm, "end": v(2.7, -328.27) * mm});
            skLineSegment(sketch, "E896", {"start": v(13.9, -330.48) * mm, "end": v(14.18, -330.48) * mm});
            skLineSegment(sketch, "E897", {"start": v(20.53, -330.48) * mm, "end": v(20.64, -330.48) * mm});
            skLineSegment(sketch, "E898", {"start": v(20.64, -330.48) * mm, "end": v(20.75, -330.47) * mm});
            skLineSegment(sketch, "E899", {"start": v(20.75, -330.47) * mm, "end": v(20.86, -330.45) * mm});
            skLineSegment(sketch, "E900", {"start": v(20.86, -330.45) * mm, "end": v(20.96, -330.42) * mm});
            skLineSegment(sketch, "E901", {"start": v(20.96, -330.42) * mm, "end": v(21.07, -330.4) * mm});
            skLineSegment(sketch, "E902", {"start": v(21.07, -330.4) * mm, "end": v(21.17, -330.35) * mm});
            skLineSegment(sketch, "E903", {"start": v(21.17, -330.35) * mm, "end": v(21.27, -330.3) * mm});
            skLineSegment(sketch, "E904", {"start": v(21.27, -330.3) * mm, "end": v(21.37, -330.25) * mm});
            skLineSegment(sketch, "E905", {"start": v(21.37, -330.25) * mm, "end": v(21.46, -330.2) * mm});
            skLineSegment(sketch, "E906", {"start": v(21.46, -330.2) * mm, "end": v(21.55, -330.13) * mm});
            skLineSegment(sketch, "E907", {"start": v(21.55, -330.13) * mm, "end": v(21.64, -330.05) * mm});
            skLineSegment(sketch, "E908", {"start": v(21.64, -330.05) * mm, "end": v(21.72, -329.98) * mm});
            skLineSegment(sketch, "E909", {"start": v(21.72, -329.98) * mm, "end": v(21.79, -329.9) * mm});
            skLineSegment(sketch, "E910", {"start": v(21.79, -329.9) * mm, "end": v(21.86, -329.8) * mm});
            skLineSegment(sketch, "E911", {"start": v(21.86, -329.8) * mm, "end": v(21.92, -329.72) * mm});
            skLineSegment(sketch, "E912", {"start": v(21.92, -329.72) * mm, "end": v(21.98, -329.62) * mm});
            skLineSegment(sketch, "E913", {"start": v(21.98, -329.62) * mm, "end": v(22.03, -329.52) * mm});
            skLineSegment(sketch, "E914", {"start": v(22.03, -329.52) * mm, "end": v(22.07, -329.42) * mm});
            skLineSegment(sketch, "E915", {"start": v(22.07, -329.42) * mm, "end": v(22.1, -329.32) * mm});
            skLineSegment(sketch, "E916", {"start": v(22.1, -329.32) * mm, "end": v(22.14, -329.21) * mm});
            skLineSegment(sketch, "E917", {"start": v(22.14, -329.21) * mm, "end": v(22.16, -329.1) * mm});
            skLineSegment(sketch, "E918", {"start": v(22.16, -329.1) * mm, "end": v(22.17, -329) * mm});
            skLineSegment(sketch, "E919", {"start": v(22.17, -329) * mm, "end": v(22.18, -328.88) * mm});
            skLineSegment(sketch, "E920", {"start": v(22.18, -328.88) * mm, "end": v(22.18, -328.77) * mm});
            skLineSegment(sketch, "E921", {"start": v(22.18, -328.77) * mm, "end": v(22.17, -328.66) * mm});
            skLineSegment(sketch, "E922", {"start": v(22.17, -328.66) * mm, "end": v(22.16, -328.55) * mm});
            skLineSegment(sketch, "E923", {"start": v(22.16, -328.55) * mm, "end": v(22.14, -328.44) * mm});
            skLineSegment(sketch, "E924", {"start": v(22.14, -328.44) * mm, "end": v(22.1, -328.34) * mm});
            skLineSegment(sketch, "E925", {"start": v(22.1, -328.34) * mm, "end": v(22.07, -328.23) * mm});
            skLineSegment(sketch, "E926", {"start": v(22.07, -328.23) * mm, "end": v(22.03, -328.13) * mm});
            skLineSegment(sketch, "E927", {"start": v(22.03, -328.13) * mm, "end": v(21.98, -328.03) * mm});
            skLineSegment(sketch, "E928", {"start": v(21.98, -328.03) * mm, "end": v(21.92, -327.94) * mm});
            skLineSegment(sketch, "E929", {"start": v(21.92, -327.94) * mm, "end": v(21.86, -327.84) * mm});
            skLineSegment(sketch, "E930", {"start": v(21.86, -327.84) * mm, "end": v(21.79, -327.76) * mm});
            skLineSegment(sketch, "E931", {"start": v(21.79, -327.76) * mm, "end": v(21.72, -327.68) * mm});
            skLineSegment(sketch, "E932", {"start": v(21.72, -327.68) * mm, "end": v(21.64, -327.6) * mm});
            skLineSegment(sketch, "E933", {"start": v(21.64, -327.6) * mm, "end": v(21.55, -327.53) * mm});
            skLineSegment(sketch, "E934", {"start": v(21.55, -327.53) * mm, "end": v(21.46, -327.46) * mm});
            skLineSegment(sketch, "E935", {"start": v(21.46, -327.46) * mm, "end": v(21.37, -327.4) * mm});
            skLineSegment(sketch, "E936", {"start": v(21.37, -327.4) * mm, "end": v(21.27, -327.35) * mm});
            skLineSegment(sketch, "E937", {"start": v(21.27, -327.35) * mm, "end": v(21.17, -327.3) * mm});
            skLineSegment(sketch, "E938", {"start": v(21.17, -327.3) * mm, "end": v(21.07, -327.26) * mm});
            skLineSegment(sketch, "E939", {"start": v(21.07, -327.26) * mm, "end": v(20.96, -327.23) * mm});
            skLineSegment(sketch, "E940", {"start": v(20.96, -327.23) * mm, "end": v(20.86, -327.2) * mm});
            skLineSegment(sketch, "E941", {"start": v(20.86, -327.2) * mm, "end": v(20.75, -327.19) * mm});
            skLineSegment(sketch, "E942", {"start": v(20.75, -327.19) * mm, "end": v(20.64, -327.17) * mm});
            skLineSegment(sketch, "E943", {"start": v(20.64, -327.17) * mm, "end": v(20.53, -327.17) * mm});
            skLineSegment(sketch, "E944", {"start": v(20.53, -327.17) * mm, "end": v(20.25, -327.17) * mm});
            skLineSegment(sketch, "E945", {"start": v(13.9, -327.17) * mm, "end": v(13.8, -327.17) * mm});
            skLineSegment(sketch, "E946", {"start": v(13.8, -327.17) * mm, "end": v(13.68, -327.19) * mm});
            skLineSegment(sketch, "E947", {"start": v(13.68, -327.19) * mm, "end": v(13.57, -327.2) * mm});
            skLineSegment(sketch, "E948", {"start": v(13.57, -327.2) * mm, "end": v(13.47, -327.23) * mm});
            skLineSegment(sketch, "E949", {"start": v(13.47, -327.23) * mm, "end": v(13.36, -327.26) * mm});
            skLineSegment(sketch, "E950", {"start": v(13.36, -327.26) * mm, "end": v(13.26, -327.3) * mm});
            skLineSegment(sketch, "E951", {"start": v(13.26, -327.3) * mm, "end": v(13.16, -327.35) * mm});
            skLineSegment(sketch, "E952", {"start": v(13.16, -327.35) * mm, "end": v(13.06, -327.4) * mm});
            skLineSegment(sketch, "E953", {"start": v(13.06, -327.4) * mm, "end": v(12.97, -327.46) * mm});
            skLineSegment(sketch, "E954", {"start": v(12.97, -327.46) * mm, "end": v(12.88, -327.53) * mm});
            skLineSegment(sketch, "E955", {"start": v(12.88, -327.53) * mm, "end": v(12.8, -327.6) * mm});
            skLineSegment(sketch, "E956", {"start": v(12.8, -327.6) * mm, "end": v(12.71, -327.68) * mm});
            skLineSegment(sketch, "E957", {"start": v(12.71, -327.68) * mm, "end": v(12.64, -327.76) * mm});
            skLineSegment(sketch, "E958", {"start": v(12.64, -327.76) * mm, "end": v(12.57, -327.84) * mm});
            skLineSegment(sketch, "E959", {"start": v(12.57, -327.84) * mm, "end": v(12.5, -327.94) * mm});
            skLineSegment(sketch, "E960", {"start": v(12.5, -327.94) * mm, "end": v(12.45, -328.03) * mm});
            skLineSegment(sketch, "E961", {"start": v(12.45, -328.03) * mm, "end": v(12.4, -328.13) * mm});
            skLineSegment(sketch, "E962", {"start": v(12.4, -328.13) * mm, "end": v(12.36, -328.23) * mm});
            skLineSegment(sketch, "E963", {"start": v(12.36, -328.23) * mm, "end": v(12.32, -328.34) * mm});
            skLineSegment(sketch, "E964", {"start": v(12.32, -328.34) * mm, "end": v(12.3, -328.44) * mm});
            skLineSegment(sketch, "E965", {"start": v(12.3, -328.44) * mm, "end": v(12.27, -328.55) * mm});
            skLineSegment(sketch, "E966", {"start": v(12.27, -328.55) * mm, "end": v(12.26, -328.66) * mm});
            skLineSegment(sketch, "E967", {"start": v(12.26, -328.66) * mm, "end": v(12.25, -328.77) * mm});
            skLineSegment(sketch, "E968", {"start": v(12.25, -328.77) * mm, "end": v(12.25, -328.88) * mm});
            skLineSegment(sketch, "E969", {"start": v(12.25, -328.88) * mm, "end": v(12.26, -329) * mm});
            skLineSegment(sketch, "E970", {"start": v(12.26, -329) * mm, "end": v(12.27, -329.1) * mm});
            skLineSegment(sketch, "E971", {"start": v(12.27, -329.1) * mm, "end": v(12.3, -329.21) * mm});
            skLineSegment(sketch, "E972", {"start": v(12.3, -329.21) * mm, "end": v(12.32, -329.32) * mm});
            skLineSegment(sketch, "E973", {"start": v(12.32, -329.32) * mm, "end": v(12.36, -329.42) * mm});
            skLineSegment(sketch, "E974", {"start": v(12.36, -329.42) * mm, "end": v(12.4, -329.52) * mm});
            skLineSegment(sketch, "E975", {"start": v(12.4, -329.52) * mm, "end": v(12.45, -329.62) * mm});
            skLineSegment(sketch, "E976", {"start": v(12.45, -329.62) * mm, "end": v(12.5, -329.72) * mm});
            skLineSegment(sketch, "E977", {"start": v(12.5, -329.72) * mm, "end": v(12.57, -329.8) * mm});
            skLineSegment(sketch, "E978", {"start": v(12.57, -329.8) * mm, "end": v(12.64, -329.9) * mm});
            skLineSegment(sketch, "E979", {"start": v(12.64, -329.9) * mm, "end": v(12.71, -329.98) * mm});
            skLineSegment(sketch, "E980", {"start": v(12.71, -329.98) * mm, "end": v(12.8, -330.05) * mm});
            skLineSegment(sketch, "E981", {"start": v(12.8, -330.05) * mm, "end": v(12.88, -330.13) * mm});
            skLineSegment(sketch, "E982", {"start": v(12.88, -330.13) * mm, "end": v(12.97, -330.2) * mm});
            skLineSegment(sketch, "E983", {"start": v(12.97, -330.2) * mm, "end": v(13.06, -330.25) * mm});
            skLineSegment(sketch, "E984", {"start": v(13.06, -330.25) * mm, "end": v(13.16, -330.3) * mm});
            skLineSegment(sketch, "E985", {"start": v(13.16, -330.3) * mm, "end": v(13.26, -330.35) * mm});
            skLineSegment(sketch, "E986", {"start": v(13.26, -330.35) * mm, "end": v(13.36, -330.4) * mm});
            skLineSegment(sketch, "E987", {"start": v(13.36, -330.4) * mm, "end": v(13.47, -330.42) * mm});
            skLineSegment(sketch, "E988", {"start": v(13.47, -330.42) * mm, "end": v(13.57, -330.45) * mm});
            skLineSegment(sketch, "E989", {"start": v(13.57, -330.45) * mm, "end": v(13.68, -330.47) * mm});
            skLineSegment(sketch, "E990", {"start": v(13.68, -330.47) * mm, "end": v(13.8, -330.48) * mm});
            skLineSegment(sketch, "E991", {"start": v(13.8, -330.48) * mm, "end": v(13.9, -330.48) * mm});
            skLineSegment(sketch, "E992", {"start": v(14.18, -327.17) * mm, "end": v(14.18, -322.76) * mm});
            skLineSegment(sketch, "E993", {"start": v(14.18, -322.76) * mm, "end": v(20.25, -322.76) * mm});
            skLineSegment(sketch, "E994", {"start": v(20.25, -322.76) * mm, "end": v(20.25, -327.17) * mm});
            skLineSegment(sketch, "E995", {"start": v(28.7, -329.38) * mm, "end": v(28.7, -326.07) * mm});
            skLineSegment(sketch, "E996", {"start": v(41.38, -328.27) * mm, "end": v(41.38, -328.13) * mm});
            skLineSegment(sketch, "E997", {"start": v(41.38, -328.13) * mm, "end": v(41.36, -327.99) * mm});
            skLineSegment(sketch, "E998", {"start": v(41.36, -327.99) * mm, "end": v(41.34, -327.84) * mm});
            skLineSegment(sketch, "E999", {"start": v(41.34, -327.84) * mm, "end": v(41.3, -327.7) * mm});
            skLineSegment(sketch, "E1000", {"start": v(41.3, -327.7) * mm, "end": v(41.27, -327.57) * mm});
            skLineSegment(sketch, "E1001", {"start": v(41.27, -327.57) * mm, "end": v(41.21, -327.43) * mm});
            skLineSegment(sketch, "E1002", {"start": v(41.21, -327.43) * mm, "end": v(41.16, -327.3) * mm});
            skLineSegment(sketch, "E1003", {"start": v(41.16, -327.3) * mm, "end": v(41.09, -327.17) * mm});
            skLineSegment(sketch, "E1004", {"start": v(41.09, -327.17) * mm, "end": v(41.01, -327.05) * mm});
            skLineSegment(sketch, "E1005", {"start": v(41.01, -327.05) * mm, "end": v(40.93, -326.93) * mm});
            skLineSegment(sketch, "E1006", {"start": v(40.93, -326.93) * mm, "end": v(40.83, -326.82) * mm});
            skLineSegment(sketch, "E1007", {"start": v(40.83, -326.82) * mm, "end": v(40.74, -326.71) * mm});
            skLineSegment(sketch, "E1008", {"start": v(40.74, -326.71) * mm, "end": v(40.63, -326.62) * mm});
            skLineSegment(sketch, "E1009", {"start": v(40.63, -326.62) * mm, "end": v(40.52, -326.52) * mm});
            skLineSegment(sketch, "E1010", {"start": v(40.52, -326.52) * mm, "end": v(40.4, -326.44) * mm});
            skLineSegment(sketch, "E1011", {"start": v(40.4, -326.44) * mm, "end": v(40.28, -326.36) * mm});
            skLineSegment(sketch, "E1012", {"start": v(40.28, -326.36) * mm, "end": v(40.15, -326.3) * mm});
            skLineSegment(sketch, "E1013", {"start": v(40.15, -326.3) * mm, "end": v(40.02, -326.24) * mm});
            skLineSegment(sketch, "E1014", {"start": v(40.02, -326.24) * mm, "end": v(39.89, -326.18) * mm});
            skLineSegment(sketch, "E1015", {"start": v(39.89, -326.18) * mm, "end": v(39.75, -326.14) * mm});
            skLineSegment(sketch, "E1016", {"start": v(39.75, -326.14) * mm, "end": v(39.6, -326.11) * mm});
            skLineSegment(sketch, "E1017", {"start": v(39.6, -326.11) * mm, "end": v(39.46, -326.09) * mm});
            skLineSegment(sketch, "E1018", {"start": v(39.46, -326.09) * mm, "end": v(39.32, -326.07) * mm});
            skLineSegment(sketch, "E1019", {"start": v(39.32, -326.07) * mm, "end": v(39.18, -326.07) * mm});
            skLineSegment(sketch, "E1020", {"start": v(39.18, -326.07) * mm, "end": v(39.03, -326.07) * mm});
            skLineSegment(sketch, "E1021", {"start": v(39.03, -326.07) * mm, "end": v(38.89, -326.09) * mm});
            skLineSegment(sketch, "E1022", {"start": v(38.89, -326.09) * mm, "end": v(38.74, -326.11) * mm});
            skLineSegment(sketch, "E1023", {"start": v(38.74, -326.11) * mm, "end": v(38.6, -326.14) * mm});
            skLineSegment(sketch, "E1024", {"start": v(38.6, -326.14) * mm, "end": v(38.47, -326.18) * mm});
            skLineSegment(sketch, "E1025", {"start": v(38.47, -326.18) * mm, "end": v(38.33, -326.24) * mm});
            skLineSegment(sketch, "E1026", {"start": v(38.33, -326.24) * mm, "end": v(38.2, -326.3) * mm});
            skLineSegment(sketch, "E1027", {"start": v(38.2, -326.3) * mm, "end": v(38.07, -326.36) * mm});
            skLineSegment(sketch, "E1028", {"start": v(38.07, -326.36) * mm, "end": v(37.95, -326.44) * mm});
            skLineSegment(sketch, "E1029", {"start": v(37.95, -326.44) * mm, "end": v(37.83, -326.52) * mm});
            skLineSegment(sketch, "E1030", {"start": v(37.83, -326.52) * mm, "end": v(37.72, -326.62) * mm});
            skLineSegment(sketch, "E1031", {"start": v(37.72, -326.62) * mm, "end": v(37.61, -326.71) * mm});
            skLineSegment(sketch, "E1032", {"start": v(37.61, -326.71) * mm, "end": v(37.52, -326.82) * mm});
            skLineSegment(sketch, "E1033", {"start": v(37.52, -326.82) * mm, "end": v(37.42, -326.93) * mm});
            skLineSegment(sketch, "E1034", {"start": v(37.42, -326.93) * mm, "end": v(37.34, -327.05) * mm});
            skLineSegment(sketch, "E1035", {"start": v(37.34, -327.05) * mm, "end": v(37.26, -327.17) * mm});
            skLineSegment(sketch, "E1036", {"start": v(37.26, -327.17) * mm, "end": v(37.2, -327.3) * mm});
            skLineSegment(sketch, "E1037", {"start": v(37.2, -327.3) * mm, "end": v(37.14, -327.43) * mm});
            skLineSegment(sketch, "E1038", {"start": v(37.14, -327.43) * mm, "end": v(37.09, -327.57) * mm});
            skLineSegment(sketch, "E1039", {"start": v(37.09, -327.57) * mm, "end": v(37.04, -327.7) * mm});
            skLineSegment(sketch, "E1040", {"start": v(37.04, -327.7) * mm, "end": v(37.01, -327.84) * mm});
            skLineSegment(sketch, "E1041", {"start": v(37.01, -327.84) * mm, "end": v(36.99, -327.99) * mm});
            skLineSegment(sketch, "E1042", {"start": v(36.99, -327.99) * mm, "end": v(36.97, -328.13) * mm});
            skLineSegment(sketch, "E1043", {"start": v(36.97, -328.13) * mm, "end": v(36.97, -328.27) * mm});
            skLineSegment(sketch, "E1044", {"start": v(36.97, -328.27) * mm, "end": v(36.97, -328.42) * mm});
            skLineSegment(sketch, "E1045", {"start": v(36.97, -328.42) * mm, "end": v(36.99, -328.56) * mm});
            skLineSegment(sketch, "E1046", {"start": v(36.99, -328.56) * mm, "end": v(37.01, -328.7) * mm});
            skLineSegment(sketch, "E1047", {"start": v(37.01, -328.7) * mm, "end": v(37.04, -328.85) * mm});
            skLineSegment(sketch, "E1048", {"start": v(37.04, -328.85) * mm, "end": v(37.09, -328.98) * mm});
            skLineSegment(sketch, "E1049", {"start": v(37.09, -328.98) * mm, "end": v(37.14, -329.12) * mm});
            skLineSegment(sketch, "E1050", {"start": v(37.14, -329.12) * mm, "end": v(37.2, -329.25) * mm});
            skLineSegment(sketch, "E1051", {"start": v(37.2, -329.25) * mm, "end": v(37.26, -329.38) * mm});
            skLineSegment(sketch, "E1052", {"start": v(37.26, -329.38) * mm, "end": v(37.34, -329.5) * mm});
            skLineSegment(sketch, "E1053", {"start": v(37.34, -329.5) * mm, "end": v(37.42, -329.62) * mm});
            skLineSegment(sketch, "E1054", {"start": v(37.42, -329.62) * mm, "end": v(37.52, -329.73) * mm});
            skLineSegment(sketch, "E1055", {"start": v(37.52, -329.73) * mm, "end": v(37.61, -329.84) * mm});
            skLineSegment(sketch, "E1056", {"start": v(37.61, -329.84) * mm, "end": v(37.72, -329.93) * mm});
            skLineSegment(sketch, "E1057", {"start": v(37.72, -329.93) * mm, "end": v(37.83, -330.03) * mm});
            skLineSegment(sketch, "E1058", {"start": v(37.83, -330.03) * mm, "end": v(37.95, -330.1) * mm});
            skLineSegment(sketch, "E1059", {"start": v(37.95, -330.1) * mm, "end": v(38.07, -330.19) * mm});
            skLineSegment(sketch, "E1060", {"start": v(38.07, -330.19) * mm, "end": v(38.2, -330.25) * mm});
            skLineSegment(sketch, "E1061", {"start": v(38.2, -330.25) * mm, "end": v(38.33, -330.31) * mm});
            skLineSegment(sketch, "E1062", {"start": v(38.33, -330.31) * mm, "end": v(38.47, -330.36) * mm});
            skLineSegment(sketch, "E1063", {"start": v(38.47, -330.36) * mm, "end": v(38.6, -330.4) * mm});
            skLineSegment(sketch, "E1064", {"start": v(38.6, -330.4) * mm, "end": v(38.74, -330.44) * mm});
            skLineSegment(sketch, "E1065", {"start": v(38.74, -330.44) * mm, "end": v(38.89, -330.46) * mm});
            skLineSegment(sketch, "E1066", {"start": v(38.89, -330.46) * mm, "end": v(39.03, -330.48) * mm});
            skLineSegment(sketch, "E1067", {"start": v(39.03, -330.48) * mm, "end": v(39.18, -330.48) * mm});
            skLineSegment(sketch, "E1068", {"start": v(39.18, -330.48) * mm, "end": v(39.32, -330.48) * mm});
            skLineSegment(sketch, "E1069", {"start": v(39.32, -330.48) * mm, "end": v(39.46, -330.46) * mm});
            skLineSegment(sketch, "E1070", {"start": v(39.46, -330.46) * mm, "end": v(39.6, -330.44) * mm});
            skLineSegment(sketch, "E1071", {"start": v(39.6, -330.44) * mm, "end": v(39.75, -330.4) * mm});
            skLineSegment(sketch, "E1072", {"start": v(39.75, -330.4) * mm, "end": v(39.89, -330.36) * mm});
            skLineSegment(sketch, "E1073", {"start": v(39.89, -330.36) * mm, "end": v(40.02, -330.31) * mm});
            skLineSegment(sketch, "E1074", {"start": v(40.02, -330.31) * mm, "end": v(40.15, -330.25) * mm});
            skLineSegment(sketch, "E1075", {"start": v(40.15, -330.25) * mm, "end": v(40.28, -330.19) * mm});
            skLineSegment(sketch, "E1076", {"start": v(40.28, -330.19) * mm, "end": v(40.4, -330.1) * mm});
            skLineSegment(sketch, "E1077", {"start": v(40.4, -330.1) * mm, "end": v(40.52, -330.03) * mm});
            skLineSegment(sketch, "E1078", {"start": v(40.52, -330.03) * mm, "end": v(40.63, -329.93) * mm});
            skLineSegment(sketch, "E1079", {"start": v(40.63, -329.93) * mm, "end": v(40.74, -329.84) * mm});
            skLineSegment(sketch, "E1080", {"start": v(40.74, -329.84) * mm, "end": v(40.83, -329.73) * mm});
            skLineSegment(sketch, "E1081", {"start": v(40.83, -329.73) * mm, "end": v(40.93, -329.62) * mm});
            skLineSegment(sketch, "E1082", {"start": v(40.93, -329.62) * mm, "end": v(41.01, -329.5) * mm});
            skLineSegment(sketch, "E1083", {"start": v(41.01, -329.5) * mm, "end": v(41.09, -329.38) * mm});
            skLineSegment(sketch, "E1084", {"start": v(41.09, -329.38) * mm, "end": v(41.16, -329.25) * mm});
            skLineSegment(sketch, "E1085", {"start": v(41.16, -329.25) * mm, "end": v(41.21, -329.12) * mm});
            skLineSegment(sketch, "E1086", {"start": v(41.21, -329.12) * mm, "end": v(41.27, -328.98) * mm});
            skLineSegment(sketch, "E1087", {"start": v(41.27, -328.98) * mm, "end": v(41.3, -328.85) * mm});
            skLineSegment(sketch, "E1088", {"start": v(41.3, -328.85) * mm, "end": v(41.34, -328.7) * mm});
            skLineSegment(sketch, "E1089", {"start": v(41.34, -328.7) * mm, "end": v(41.36, -328.56) * mm});
            skLineSegment(sketch, "E1090", {"start": v(41.36, -328.56) * mm, "end": v(41.38, -328.42) * mm});
            skLineSegment(sketch, "E1091", {"start": v(41.38, -328.42) * mm, "end": v(41.38, -328.27) * mm});
            skLineSegment(sketch, "E1092", {"start": v(-8.77, -329.38) * mm, "end": v(-5.74, -329.38) * mm});
            skLineSegment(sketch, "E1093", {"start": v(-8.77, -326.07) * mm, "end": v(-9.05, -326.07) * mm});
            skLineSegment(sketch, "E1094", {"start": v(-5.74, -326.07) * mm, "end": v(-8.77, -326.07) * mm});
            skLineSegment(sketch, "E1095", {"start": v(-2.7, -326.07) * mm, "end": v(-5.74, -326.07) * mm});
            skLineSegment(sketch, "E1096", {"start": v(-34.9, -336) * mm, "end": v(-39.18, -336) * mm});
            skLineSegment(sketch, "E1097", {"start": v(-31.45, -336) * mm, "end": v(-34.9, -336) * mm});
            skLineSegment(sketch, "E1098", {"start": v(-25.93, -336) * mm, "end": v(-31.45, -336) * mm});
            skLineSegment(sketch, "E1099", {"start": v(-19.97, -336) * mm, "end": v(-25.93, -336) * mm});
            skLineSegment(sketch, "E1100", {"start": v(-14.46, -336) * mm, "end": v(-19.97, -336) * mm});
            skLineSegment(sketch, "E1101", {"start": v(34.9, -336) * mm, "end": v(31.45, -336) * mm});
            skLineSegment(sketch, "E1102", {"start": v(-34.9, -320.55) * mm, "end": v(34.9, -320.55) * mm});
            skLineSegment(sketch, "E1103", {"start": v(-31.73, -331.59) * mm, "end": v(-28.7, -331.59) * mm});
            skLineSegment(sketch, "E1104", {"start": v(-28.7, -328.27) * mm, "end": v(-31.73, -328.27) * mm});
            skLineSegment(sketch, "E1105", {"start": v(-25.66, -328.27) * mm, "end": v(-28.7, -328.27) * mm});
            skLineSegment(sketch, "E1106", {"start": v(-14.18, -330.48) * mm, "end": v(-13.9, -330.48) * mm});
            skLineSegment(sketch, "E1107", {"start": v(-20.25, -330.48) * mm, "end": v(-17.22, -330.48) * mm});
            skLineSegment(sketch, "E1108", {"start": v(-17.22, -327.17) * mm, "end": v(-20.25, -327.17) * mm});
            skLineSegment(sketch, "E1109", {"start": v(-14.18, -327.17) * mm, "end": v(-17.22, -327.17) * mm});
            skLineSegment(sketch, "E1110", {"start": v(25.66, -329.38) * mm, "end": v(28.7, -329.38) * mm});
            skLineSegment(sketch, "E1111", {"start": v(31.73, -326.07) * mm, "end": v(28.7, -326.07) * mm});
            skLineSegment(sketch, "E1112", {"start": v(2.7, -331.59) * mm, "end": v(5.74, -331.59) * mm});
            skLineSegment(sketch, "E1113", {"start": v(5.74, -328.27) * mm, "end": v(2.7, -328.27) * mm});
            skLineSegment(sketch, "E1114", {"start": v(8.77, -328.27) * mm, "end": v(5.74, -328.27) * mm});
            skLineSegment(sketch, "E1115", {"start": v(20.25, -330.48) * mm, "end": v(20.53, -330.48) * mm});
            skLineSegment(sketch, "E1116", {"start": v(14.18, -330.48) * mm, "end": v(17.22, -330.48) * mm});
            skLineSegment(sketch, "E1117", {"start": v(17.22, -327.17) * mm, "end": v(14.18, -327.17) * mm});
            skLineSegment(sketch, "E1118", {"start": v(20.25, -327.17) * mm, "end": v(17.22, -327.17) * mm});
            skLineSegment(sketch, "E1119", {"start": v(-2.7, -329.38) * mm, "end": v(-2.43, -329.38) * mm});
            skLineSegment(sketch, "E1120", {"start": v(-5.74, -329.38) * mm, "end": v(-2.7, -329.38) * mm});
            skLineSegment(sketch, "E1121", {"start": v(25.93, -336) * mm, "end": v(19.97, -336) * mm});
            skLineSegment(sketch, "E1122", {"start": v(31.45, -336) * mm, "end": v(25.93, -336) * mm});
            skLineSegment(sketch, "E1123", {"start": v(34.9, -320.55) * mm, "end": v(39.18, -320.55) * mm});
            skLineSegment(sketch, "E1124", {"start": v(-25.66, -331.59) * mm, "end": v(-25.38, -331.59) * mm});
            skLineSegment(sketch, "E1125", {"start": v(-28.7, -331.59) * mm, "end": v(-25.66, -331.59) * mm});
            skLineSegment(sketch, "E1126", {"start": v(-31.73, -328.27) * mm, "end": v(-32, -328.27) * mm});
            skLineSegment(sketch, "E1127", {"start": v(-17.22, -330.48) * mm, "end": v(-14.18, -330.48) * mm});
            skLineSegment(sketch, "E1128", {"start": v(-20.25, -327.17) * mm, "end": v(-20.53, -327.17) * mm});
            skLineSegment(sketch, "E1129", {"start": v(31.73, -329.38) * mm, "end": v(32, -329.38) * mm});
            skLineSegment(sketch, "E1130", {"start": v(28.7, -329.38) * mm, "end": v(31.73, -329.38) * mm});
            skLineSegment(sketch, "E1131", {"start": v(25.66, -326.07) * mm, "end": v(25.38, -326.07) * mm});
            skLineSegment(sketch, "E1132", {"start": v(28.7, -326.07) * mm, "end": v(25.66, -326.07) * mm});
            skLineSegment(sketch, "E1133", {"start": v(8.77, -331.59) * mm, "end": v(9.05, -331.59) * mm});
            skLineSegment(sketch, "E1134", {"start": v(5.74, -331.59) * mm, "end": v(8.77, -331.59) * mm});
            skLineSegment(sketch, "E1135", {"start": v(2.7, -328.27) * mm, "end": v(2.43, -328.27) * mm});
            skLineSegment(sketch, "E1136", {"start": v(17.22, -330.48) * mm, "end": v(20.25, -330.48) * mm});
            skLineSegment(sketch, "E1137", {"start": v(14.18, -327.17) * mm, "end": v(13.9, -327.17) * mm});
            skLineSegment(sketch, "E1138", {"start": v(-8.5, -336) * mm, "end": v(-14.46, -336) * mm});
            skLineSegment(sketch, "E1139", {"start": v(2.98, -336) * mm, "end": v(-2.98, -336) * mm});
            skLineSegment(sketch, "E1140", {"start": v(14.46, -336) * mm, "end": v(8.5, -336) * mm});
            skLineSegment(sketch, "E1141", {"start": v(19.97, -336) * mm, "end": v(14.46, -336) * mm});
            skLineSegment(sketch, "E1142", {"start": v(-2.98, -336) * mm, "end": v(-8.5, -336) * mm});
            skLineSegment(sketch, "E1143", {"start": v(8.5, -336) * mm, "end": v(2.98, -336) * mm});
            skLineSegment(sketch, "E1144", {"start": v(-14.18, -377.93) * mm, "end": v(-14.19, -377.74) * mm});
            skLineSegment(sketch, "E1145", {"start": v(-14.19, -377.74) * mm, "end": v(-14.2, -377.54) * mm});
            skLineSegment(sketch, "E1146", {"start": v(-14.2, -377.54) * mm, "end": v(-14.24, -377.34) * mm});
            skLineSegment(sketch, "E1147", {"start": v(-14.24, -377.34) * mm, "end": v(-14.28, -377.15) * mm});
            skLineSegment(sketch, "E1148", {"start": v(-14.28, -377.15) * mm, "end": v(-14.34, -376.96) * mm});
            skLineSegment(sketch, "E1149", {"start": v(-14.34, -376.96) * mm, "end": v(-14.41, -376.77) * mm});
            skLineSegment(sketch, "E1150", {"start": v(-14.41, -376.77) * mm, "end": v(-14.5, -376.6) * mm});
            skLineSegment(sketch, "E1151", {"start": v(-14.5, -376.6) * mm, "end": v(-14.59, -376.42) * mm});
            skLineSegment(sketch, "E1152", {"start": v(-14.59, -376.42) * mm, "end": v(-14.7, -376.25) * mm});
            skLineSegment(sketch, "E1153", {"start": v(-14.7, -376.25) * mm, "end": v(-14.8, -376.09) * mm});
            skLineSegment(sketch, "E1154", {"start": v(-14.8, -376.09) * mm, "end": v(-14.93, -375.93) * mm});
            skLineSegment(sketch, "E1155", {"start": v(-14.93, -375.93) * mm, "end": v(-15.07, -375.79) * mm});
            skLineSegment(sketch, "E1156", {"start": v(-15.07, -375.79) * mm, "end": v(-15.21, -375.65) * mm});
            skLineSegment(sketch, "E1157", {"start": v(-15.21, -375.65) * mm, "end": v(-15.37, -375.53) * mm});
            skLineSegment(sketch, "E1158", {"start": v(-15.37, -375.53) * mm, "end": v(-15.53, -375.41) * mm});
            skLineSegment(sketch, "E1159", {"start": v(-15.53, -375.41) * mm, "end": v(-15.7, -375.3) * mm});
            skLineSegment(sketch, "E1160", {"start": v(-15.7, -375.3) * mm, "end": v(-15.87, -375.21) * mm});
            skLineSegment(sketch, "E1161", {"start": v(-15.87, -375.21) * mm, "end": v(-16.05, -375.13) * mm});
            skLineSegment(sketch, "E1162", {"start": v(-16.05, -375.13) * mm, "end": v(-16.24, -375.06) * mm});
            skLineSegment(sketch, "E1163", {"start": v(-16.24, -375.06) * mm, "end": v(-16.43, -375) * mm});
            skLineSegment(sketch, "E1164", {"start": v(-16.43, -375) * mm, "end": v(-16.62, -374.96) * mm});
            skLineSegment(sketch, "E1165", {"start": v(-16.62, -374.96) * mm, "end": v(-16.82, -374.93) * mm});
            skLineSegment(sketch, "E1166", {"start": v(-16.82, -374.93) * mm, "end": v(-17.02, -374.9) * mm});
            skLineSegment(sketch, "E1167", {"start": v(-17.02, -374.9) * mm, "end": v(-17.22, -374.9) * mm});
            skLineSegment(sketch, "E1168", {"start": v(-17.22, -374.9) * mm, "end": v(-17.41, -374.9) * mm});
            skLineSegment(sketch, "E1169", {"start": v(-17.41, -374.9) * mm, "end": v(-17.61, -374.93) * mm});
            skLineSegment(sketch, "E1170", {"start": v(-17.61, -374.93) * mm, "end": v(-17.8, -374.96) * mm});
            skLineSegment(sketch, "E1171", {"start": v(-17.8, -374.96) * mm, "end": v(-18, -375) * mm});
            skLineSegment(sketch, "E1172", {"start": v(-18, -375) * mm, "end": v(-18.2, -375.06) * mm});
            skLineSegment(sketch, "E1173", {"start": v(-18.2, -375.06) * mm, "end": v(-18.38, -375.13) * mm});
            skLineSegment(sketch, "E1174", {"start": v(-18.38, -375.13) * mm, "end": v(-18.56, -375.21) * mm});
            skLineSegment(sketch, "E1175", {"start": v(-18.56, -375.21) * mm, "end": v(-18.73, -375.3) * mm});
            skLineSegment(sketch, "E1176", {"start": v(-18.73, -375.3) * mm, "end": v(-18.9, -375.41) * mm});
            skLineSegment(sketch, "E1177", {"start": v(-18.9, -375.41) * mm, "end": v(-19.06, -375.53) * mm});
            skLineSegment(sketch, "E1178", {"start": v(-19.06, -375.53) * mm, "end": v(-19.22, -375.65) * mm});
            skLineSegment(sketch, "E1179", {"start": v(-19.22, -375.65) * mm, "end": v(-19.36, -375.79) * mm});
            skLineSegment(sketch, "E1180", {"start": v(-19.36, -375.79) * mm, "end": v(-19.5, -375.93) * mm});
            skLineSegment(sketch, "E1181", {"start": v(-19.5, -375.93) * mm, "end": v(-19.62, -376.09) * mm});
            skLineSegment(sketch, "E1182", {"start": v(-19.62, -376.09) * mm, "end": v(-19.74, -376.25) * mm});
            skLineSegment(sketch, "E1183", {"start": v(-19.74, -376.25) * mm, "end": v(-19.84, -376.42) * mm});
            skLineSegment(sketch, "E1184", {"start": v(-19.84, -376.42) * mm, "end": v(-19.94, -376.6) * mm});
            skLineSegment(sketch, "E1185", {"start": v(-19.94, -376.6) * mm, "end": v(-20.02, -376.77) * mm});
            skLineSegment(sketch, "E1186", {"start": v(-20.02, -376.77) * mm, "end": v(-20.09, -376.96) * mm});
            skLineSegment(sketch, "E1187", {"start": v(-20.09, -376.96) * mm, "end": v(-20.15, -377.15) * mm});
            skLineSegment(sketch, "E1188", {"start": v(-20.15, -377.15) * mm, "end": v(-20.2, -377.34) * mm});
            skLineSegment(sketch, "E1189", {"start": v(-20.2, -377.34) * mm, "end": v(-20.22, -377.54) * mm});
            skLineSegment(sketch, "E1190", {"start": v(-20.22, -377.54) * mm, "end": v(-20.24, -377.74) * mm});
            skLineSegment(sketch, "E1191", {"start": v(-20.24, -377.74) * mm, "end": v(-20.25, -377.93) * mm});
            skLineSegment(sketch, "E1192", {"start": v(-20.25, -377.93) * mm, "end": v(-20.24, -378.13) * mm});
            skLineSegment(sketch, "E1193", {"start": v(-20.24, -378.13) * mm, "end": v(-20.22, -378.33) * mm});
            skLineSegment(sketch, "E1194", {"start": v(-20.22, -378.33) * mm, "end": v(-20.2, -378.53) * mm});
            skLineSegment(sketch, "E1195", {"start": v(-20.2, -378.53) * mm, "end": v(-20.15, -378.72) * mm});
            skLineSegment(sketch, "E1196", {"start": v(-20.15, -378.72) * mm, "end": v(-20.09, -378.9) * mm});
            skLineSegment(sketch, "E1197", {"start": v(-20.09, -378.9) * mm, "end": v(-20.02, -379.1) * mm});
            skLineSegment(sketch, "E1198", {"start": v(-20.02, -379.1) * mm, "end": v(-19.94, -379.28) * mm});
            skLineSegment(sketch, "E1199", {"start": v(-19.94, -379.28) * mm, "end": v(-19.84, -379.45) * mm});
            skLineSegment(sketch, "E1200", {"start": v(-19.84, -379.45) * mm, "end": v(-19.74, -379.62) * mm});
            skLineSegment(sketch, "E1201", {"start": v(-19.74, -379.62) * mm, "end": v(-19.62, -379.78) * mm});
            skLineSegment(sketch, "E1202", {"start": v(-19.62, -379.78) * mm, "end": v(-19.5, -379.93) * mm});
            skLineSegment(sketch, "E1203", {"start": v(-19.5, -379.93) * mm, "end": v(-19.36, -380.08) * mm});
            skLineSegment(sketch, "E1204", {"start": v(-19.36, -380.08) * mm, "end": v(-19.22, -380.22) * mm});
            skLineSegment(sketch, "E1205", {"start": v(-19.22, -380.22) * mm, "end": v(-19.06, -380.34) * mm});
            skLineSegment(sketch, "E1206", {"start": v(-19.06, -380.34) * mm, "end": v(-18.9, -380.46) * mm});
            skLineSegment(sketch, "E1207", {"start": v(-18.9, -380.46) * mm, "end": v(-18.73, -380.56) * mm});
            skLineSegment(sketch, "E1208", {"start": v(-18.73, -380.56) * mm, "end": v(-18.56, -380.66) * mm});
            skLineSegment(sketch, "E1209", {"start": v(-18.56, -380.66) * mm, "end": v(-18.38, -380.74) * mm});
            skLineSegment(sketch, "E1210", {"start": v(-18.38, -380.74) * mm, "end": v(-18.2, -380.8) * mm});
            skLineSegment(sketch, "E1211", {"start": v(-18.2, -380.8) * mm, "end": v(-18, -380.87) * mm});
            skLineSegment(sketch, "E1212", {"start": v(-18, -380.87) * mm, "end": v(-17.8, -380.91) * mm});
            skLineSegment(sketch, "E1213", {"start": v(-17.8, -380.91) * mm, "end": v(-17.61, -380.94) * mm});
            skLineSegment(sketch, "E1214", {"start": v(-17.61, -380.94) * mm, "end": v(-17.41, -380.96) * mm});
            skLineSegment(sketch, "E1215", {"start": v(-17.41, -380.96) * mm, "end": v(-17.22, -380.97) * mm});
            skLineSegment(sketch, "E1216", {"start": v(-17.22, -380.97) * mm, "end": v(-17.02, -380.96) * mm});
            skLineSegment(sketch, "E1217", {"start": v(-17.02, -380.96) * mm, "end": v(-16.82, -380.94) * mm});
            skLineSegment(sketch, "E1218", {"start": v(-16.82, -380.94) * mm, "end": v(-16.62, -380.91) * mm});
            skLineSegment(sketch, "E1219", {"start": v(-16.62, -380.91) * mm, "end": v(-16.43, -380.87) * mm});
            skLineSegment(sketch, "E1220", {"start": v(-16.43, -380.87) * mm, "end": v(-16.24, -380.8) * mm});
            skLineSegment(sketch, "E1221", {"start": v(-16.24, -380.8) * mm, "end": v(-16.05, -380.74) * mm});
            skLineSegment(sketch, "E1222", {"start": v(-16.05, -380.74) * mm, "end": v(-15.87, -380.66) * mm});
            skLineSegment(sketch, "E1223", {"start": v(-15.87, -380.66) * mm, "end": v(-15.7, -380.56) * mm});
            skLineSegment(sketch, "E1224", {"start": v(-15.7, -380.56) * mm, "end": v(-15.53, -380.46) * mm});
            skLineSegment(sketch, "E1225", {"start": v(-15.53, -380.46) * mm, "end": v(-15.37, -380.34) * mm});
            skLineSegment(sketch, "E1226", {"start": v(-15.37, -380.34) * mm, "end": v(-15.21, -380.22) * mm});
            skLineSegment(sketch, "E1227", {"start": v(-15.21, -380.22) * mm, "end": v(-15.07, -380.08) * mm});
            skLineSegment(sketch, "E1228", {"start": v(-15.07, -380.08) * mm, "end": v(-14.93, -379.93) * mm});
            skLineSegment(sketch, "E1229", {"start": v(-14.93, -379.93) * mm, "end": v(-14.8, -379.78) * mm});
            skLineSegment(sketch, "E1230", {"start": v(-14.8, -379.78) * mm, "end": v(-14.7, -379.62) * mm});
            skLineSegment(sketch, "E1231", {"start": v(-14.7, -379.62) * mm, "end": v(-14.59, -379.45) * mm});
            skLineSegment(sketch, "E1232", {"start": v(-14.59, -379.45) * mm, "end": v(-14.5, -379.28) * mm});
            skLineSegment(sketch, "E1233", {"start": v(-14.5, -379.28) * mm, "end": v(-14.41, -379.1) * mm});
            skLineSegment(sketch, "E1234", {"start": v(-14.41, -379.1) * mm, "end": v(-14.34, -378.9) * mm});
            skLineSegment(sketch, "E1235", {"start": v(-14.34, -378.9) * mm, "end": v(-14.28, -378.72) * mm});
            skLineSegment(sketch, "E1236", {"start": v(-14.28, -378.72) * mm, "end": v(-14.24, -378.53) * mm});
            skLineSegment(sketch, "E1237", {"start": v(-14.24, -378.53) * mm, "end": v(-14.2, -378.33) * mm});
            skLineSegment(sketch, "E1238", {"start": v(-14.2, -378.33) * mm, "end": v(-14.19, -378.13) * mm});
            skLineSegment(sketch, "E1239", {"start": v(-14.19, -378.13) * mm, "end": v(-14.18, -377.93) * mm});
            skLineSegment(sketch, "E1240", {"start": v(-15.56, -377.93) * mm, "end": v(-15.56, -377.83) * mm});
            skLineSegment(sketch, "E1241", {"start": v(-15.56, -377.83) * mm, "end": v(-15.57, -377.72) * mm});
            skLineSegment(sketch, "E1242", {"start": v(-15.57, -377.72) * mm, "end": v(-15.6, -377.61) * mm});
            skLineSegment(sketch, "E1243", {"start": v(-15.6, -377.61) * mm, "end": v(-15.62, -377.5) * mm});
            skLineSegment(sketch, "E1244", {"start": v(-15.62, -377.5) * mm, "end": v(-15.65, -377.4) * mm});
            skLineSegment(sketch, "E1245", {"start": v(-15.65, -377.4) * mm, "end": v(-15.69, -377.3) * mm});
            skLineSegment(sketch, "E1246", {"start": v(-15.69, -377.3) * mm, "end": v(-15.73, -377.2) * mm});
            skLineSegment(sketch, "E1247", {"start": v(-15.73, -377.2) * mm, "end": v(-15.78, -377.1) * mm});
            skLineSegment(sketch, "E1248", {"start": v(-15.78, -377.1) * mm, "end": v(-15.84, -377.01) * mm});
            skLineSegment(sketch, "E1249", {"start": v(-15.84, -377.01) * mm, "end": v(-15.9, -376.93) * mm});
            skLineSegment(sketch, "E1250", {"start": v(-15.9, -376.93) * mm, "end": v(-15.97, -376.84) * mm});
            skLineSegment(sketch, "E1251", {"start": v(-15.97, -376.84) * mm, "end": v(-16.04, -376.76) * mm});
            skLineSegment(sketch, "E1252", {"start": v(-16.04, -376.76) * mm, "end": v(-16.12, -376.69) * mm});
            skLineSegment(sketch, "E1253", {"start": v(-16.12, -376.69) * mm, "end": v(-16.2, -376.62) * mm});
            skLineSegment(sketch, "E1254", {"start": v(-16.2, -376.62) * mm, "end": v(-16.3, -376.56) * mm});
            skLineSegment(sketch, "E1255", {"start": v(-16.3, -376.56) * mm, "end": v(-16.39, -376.5) * mm});
            skLineSegment(sketch, "E1256", {"start": v(-16.39, -376.5) * mm, "end": v(-16.48, -376.45) * mm});
            skLineSegment(sketch, "E1257", {"start": v(-16.48, -376.45) * mm, "end": v(-16.58, -376.4) * mm});
            skLineSegment(sketch, "E1258", {"start": v(-16.58, -376.4) * mm, "end": v(-16.68, -376.37) * mm});
            skLineSegment(sketch, "E1259", {"start": v(-16.68, -376.37) * mm, "end": v(-16.79, -376.33) * mm});
            skLineSegment(sketch, "E1260", {"start": v(-16.79, -376.33) * mm, "end": v(-16.9, -376.31) * mm});
            skLineSegment(sketch, "E1261", {"start": v(-16.9, -376.31) * mm, "end": v(-17, -376.3) * mm});
            skLineSegment(sketch, "E1262", {"start": v(-17, -376.3) * mm, "end": v(-17.1, -376.28) * mm});
            skLineSegment(sketch, "E1263", {"start": v(-17.1, -376.28) * mm, "end": v(-17.22, -376.28) * mm});
            skLineSegment(sketch, "E1264", {"start": v(-17.22, -376.28) * mm, "end": v(-17.32, -376.28) * mm});
            skLineSegment(sketch, "E1265", {"start": v(-17.32, -376.28) * mm, "end": v(-17.43, -376.3) * mm});
            skLineSegment(sketch, "E1266", {"start": v(-17.43, -376.3) * mm, "end": v(-17.54, -376.31) * mm});
            skLineSegment(sketch, "E1267", {"start": v(-17.54, -376.31) * mm, "end": v(-17.64, -376.33) * mm});
            skLineSegment(sketch, "E1268", {"start": v(-17.64, -376.33) * mm, "end": v(-17.75, -376.37) * mm});
            skLineSegment(sketch, "E1269", {"start": v(-17.75, -376.37) * mm, "end": v(-17.85, -376.4) * mm});
            skLineSegment(sketch, "E1270", {"start": v(-17.85, -376.4) * mm, "end": v(-17.95, -376.45) * mm});
            skLineSegment(sketch, "E1271", {"start": v(-17.95, -376.45) * mm, "end": v(-18.04, -376.5) * mm});
            skLineSegment(sketch, "E1272", {"start": v(-18.04, -376.5) * mm, "end": v(-18.13, -376.56) * mm});
            skLineSegment(sketch, "E1273", {"start": v(-18.13, -376.56) * mm, "end": v(-18.22, -376.62) * mm});
            skLineSegment(sketch, "E1274", {"start": v(-18.22, -376.62) * mm, "end": v(-18.3, -376.69) * mm});
            skLineSegment(sketch, "E1275", {"start": v(-18.3, -376.69) * mm, "end": v(-18.39, -376.76) * mm});
            skLineSegment(sketch, "E1276", {"start": v(-18.39, -376.76) * mm, "end": v(-18.46, -376.84) * mm});
            skLineSegment(sketch, "E1277", {"start": v(-18.46, -376.84) * mm, "end": v(-18.53, -376.93) * mm});
            skLineSegment(sketch, "E1278", {"start": v(-18.53, -376.93) * mm, "end": v(-18.6, -377.01) * mm});
            skLineSegment(sketch, "E1279", {"start": v(-18.6, -377.01) * mm, "end": v(-18.65, -377.1) * mm});
            skLineSegment(sketch, "E1280", {"start": v(-18.65, -377.1) * mm, "end": v(-18.7, -377.2) * mm});
            skLineSegment(sketch, "E1281", {"start": v(-18.7, -377.2) * mm, "end": v(-18.74, -377.3) * mm});
            skLineSegment(sketch, "E1282", {"start": v(-18.74, -377.3) * mm, "end": v(-18.78, -377.4) * mm});
            skLineSegment(sketch, "E1283", {"start": v(-18.78, -377.4) * mm, "end": v(-18.81, -377.5) * mm});
            skLineSegment(sketch, "E1284", {"start": v(-18.81, -377.5) * mm, "end": v(-18.84, -377.61) * mm});
            skLineSegment(sketch, "E1285", {"start": v(-18.84, -377.61) * mm, "end": v(-18.86, -377.72) * mm});
            skLineSegment(sketch, "E1286", {"start": v(-18.86, -377.72) * mm, "end": v(-18.87, -377.83) * mm});
            skLineSegment(sketch, "E1287", {"start": v(-18.87, -377.83) * mm, "end": v(-18.87, -377.93) * mm});
            skLineSegment(sketch, "E1288", {"start": v(-18.87, -377.93) * mm, "end": v(-18.87, -378.04) * mm});
            skLineSegment(sketch, "E1289", {"start": v(-18.87, -378.04) * mm, "end": v(-18.86, -378.15) * mm});
            skLineSegment(sketch, "E1290", {"start": v(-18.86, -378.15) * mm, "end": v(-18.84, -378.26) * mm});
            skLineSegment(sketch, "E1291", {"start": v(-18.84, -378.26) * mm, "end": v(-18.81, -378.36) * mm});
            skLineSegment(sketch, "E1292", {"start": v(-18.81, -378.36) * mm, "end": v(-18.78, -378.47) * mm});
            skLineSegment(sketch, "E1293", {"start": v(-18.78, -378.47) * mm, "end": v(-18.74, -378.57) * mm});
            skLineSegment(sketch, "E1294", {"start": v(-18.74, -378.57) * mm, "end": v(-18.7, -378.67) * mm});
            skLineSegment(sketch, "E1295", {"start": v(-18.7, -378.67) * mm, "end": v(-18.65, -378.76) * mm});
            skLineSegment(sketch, "E1296", {"start": v(-18.65, -378.76) * mm, "end": v(-18.6, -378.85) * mm});
            skLineSegment(sketch, "E1297", {"start": v(-18.6, -378.85) * mm, "end": v(-18.53, -378.94) * mm});
            skLineSegment(sketch, "E1298", {"start": v(-18.53, -378.94) * mm, "end": v(-18.46, -379.03) * mm});
            skLineSegment(sketch, "E1299", {"start": v(-18.46, -379.03) * mm, "end": v(-18.39, -379.1) * mm});
            skLineSegment(sketch, "E1300", {"start": v(-18.39, -379.1) * mm, "end": v(-18.3, -379.18) * mm});
            skLineSegment(sketch, "E1301", {"start": v(-18.3, -379.18) * mm, "end": v(-18.22, -379.25) * mm});
            skLineSegment(sketch, "E1302", {"start": v(-18.22, -379.25) * mm, "end": v(-18.13, -379.31) * mm});
            skLineSegment(sketch, "E1303", {"start": v(-18.13, -379.31) * mm, "end": v(-18.04, -379.37) * mm});
            skLineSegment(sketch, "E1304", {"start": v(-18.04, -379.37) * mm, "end": v(-17.95, -379.42) * mm});
            skLineSegment(sketch, "E1305", {"start": v(-17.95, -379.42) * mm, "end": v(-17.85, -379.46) * mm});
            skLineSegment(sketch, "E1306", {"start": v(-17.85, -379.46) * mm, "end": v(-17.75, -379.5) * mm});
            skLineSegment(sketch, "E1307", {"start": v(-17.75, -379.5) * mm, "end": v(-17.64, -379.53) * mm});
            skLineSegment(sketch, "E1308", {"start": v(-17.64, -379.53) * mm, "end": v(-17.54, -379.56) * mm});
            skLineSegment(sketch, "E1309", {"start": v(-17.54, -379.56) * mm, "end": v(-17.43, -379.58) * mm});
            skLineSegment(sketch, "E1310", {"start": v(-17.43, -379.58) * mm, "end": v(-17.32, -379.59) * mm});
            skLineSegment(sketch, "E1311", {"start": v(-17.32, -379.59) * mm, "end": v(-17.22, -379.59) * mm});
            skLineSegment(sketch, "E1312", {"start": v(-17.22, -379.59) * mm, "end": v(-17.1, -379.59) * mm});
            skLineSegment(sketch, "E1313", {"start": v(-17.1, -379.59) * mm, "end": v(-17, -379.58) * mm});
            skLineSegment(sketch, "E1314", {"start": v(-17, -379.58) * mm, "end": v(-16.9, -379.56) * mm});
            skLineSegment(sketch, "E1315", {"start": v(-16.9, -379.56) * mm, "end": v(-16.79, -379.53) * mm});
            skLineSegment(sketch, "E1316", {"start": v(-16.79, -379.53) * mm, "end": v(-16.68, -379.5) * mm});
            skLineSegment(sketch, "E1317", {"start": v(-16.68, -379.5) * mm, "end": v(-16.58, -379.46) * mm});
            skLineSegment(sketch, "E1318", {"start": v(-16.58, -379.46) * mm, "end": v(-16.48, -379.42) * mm});
            skLineSegment(sketch, "E1319", {"start": v(-16.48, -379.42) * mm, "end": v(-16.39, -379.37) * mm});
            skLineSegment(sketch, "E1320", {"start": v(-16.39, -379.37) * mm, "end": v(-16.3, -379.31) * mm});
            skLineSegment(sketch, "E1321", {"start": v(-16.3, -379.31) * mm, "end": v(-16.2, -379.25) * mm});
            skLineSegment(sketch, "E1322", {"start": v(-16.2, -379.25) * mm, "end": v(-16.12, -379.18) * mm});
            skLineSegment(sketch, "E1323", {"start": v(-16.12, -379.18) * mm, "end": v(-16.04, -379.1) * mm});
            skLineSegment(sketch, "E1324", {"start": v(-16.04, -379.1) * mm, "end": v(-15.97, -379.03) * mm});
            skLineSegment(sketch, "E1325", {"start": v(-15.97, -379.03) * mm, "end": v(-15.9, -378.94) * mm});
            skLineSegment(sketch, "E1326", {"start": v(-15.9, -378.94) * mm, "end": v(-15.84, -378.85) * mm});
            skLineSegment(sketch, "E1327", {"start": v(-15.84, -378.85) * mm, "end": v(-15.78, -378.76) * mm});
            skLineSegment(sketch, "E1328", {"start": v(-15.78, -378.76) * mm, "end": v(-15.73, -378.67) * mm});
            skLineSegment(sketch, "E1329", {"start": v(-15.73, -378.67) * mm, "end": v(-15.69, -378.57) * mm});
            skLineSegment(sketch, "E1330", {"start": v(-15.69, -378.57) * mm, "end": v(-15.65, -378.47) * mm});
            skLineSegment(sketch, "E1331", {"start": v(-15.65, -378.47) * mm, "end": v(-15.62, -378.36) * mm});
            skLineSegment(sketch, "E1332", {"start": v(-15.62, -378.36) * mm, "end": v(-15.6, -378.26) * mm});
            skLineSegment(sketch, "E1333", {"start": v(-15.6, -378.26) * mm, "end": v(-15.57, -378.15) * mm});
            skLineSegment(sketch, "E1334", {"start": v(-15.57, -378.15) * mm, "end": v(-15.56, -378.04) * mm});
            skLineSegment(sketch, "E1335", {"start": v(-15.56, -378.04) * mm, "end": v(-15.56, -377.93) * mm});
            skLineSegment(sketch, "E1336", {"start": v(-25.66, -377.93) * mm, "end": v(-25.66, -377.74) * mm});
            skLineSegment(sketch, "E1337", {"start": v(-25.66, -377.74) * mm, "end": v(-25.68, -377.54) * mm});
            skLineSegment(sketch, "E1338", {"start": v(-25.68, -377.54) * mm, "end": v(-25.72, -377.34) * mm});
            skLineSegment(sketch, "E1339", {"start": v(-25.72, -377.34) * mm, "end": v(-25.76, -377.15) * mm});
            skLineSegment(sketch, "E1340", {"start": v(-25.76, -377.15) * mm, "end": v(-25.82, -376.96) * mm});
            skLineSegment(sketch, "E1341", {"start": v(-25.82, -376.96) * mm, "end": v(-25.89, -376.77) * mm});
            skLineSegment(sketch, "E1342", {"start": v(-25.89, -376.77) * mm, "end": v(-25.97, -376.6) * mm});
            skLineSegment(sketch, "E1343", {"start": v(-25.97, -376.6) * mm, "end": v(-26.06, -376.42) * mm});
            skLineSegment(sketch, "E1344", {"start": v(-26.06, -376.42) * mm, "end": v(-26.17, -376.25) * mm});
            skLineSegment(sketch, "E1345", {"start": v(-26.17, -376.25) * mm, "end": v(-26.28, -376.09) * mm});
            skLineSegment(sketch, "E1346", {"start": v(-26.28, -376.09) * mm, "end": v(-26.41, -375.93) * mm});
            skLineSegment(sketch, "E1347", {"start": v(-26.41, -375.93) * mm, "end": v(-26.55, -375.79) * mm});
            skLineSegment(sketch, "E1348", {"start": v(-26.55, -375.79) * mm, "end": v(-26.7, -375.65) * mm});
            skLineSegment(sketch, "E1349", {"start": v(-26.7, -375.65) * mm, "end": v(-26.84, -375.53) * mm});
            skLineSegment(sketch, "E1350", {"start": v(-26.84, -375.53) * mm, "end": v(-27, -375.41) * mm});
            skLineSegment(sketch, "E1351", {"start": v(-27, -375.41) * mm, "end": v(-27.17, -375.3) * mm});
            skLineSegment(sketch, "E1352", {"start": v(-27.17, -375.3) * mm, "end": v(-27.35, -375.21) * mm});
            skLineSegment(sketch, "E1353", {"start": v(-27.35, -375.21) * mm, "end": v(-27.53, -375.13) * mm});
            skLineSegment(sketch, "E1354", {"start": v(-27.53, -375.13) * mm, "end": v(-27.72, -375.06) * mm});
            skLineSegment(sketch, "E1355", {"start": v(-27.72, -375.06) * mm, "end": v(-27.9, -375) * mm});
            skLineSegment(sketch, "E1356", {"start": v(-27.9, -375) * mm, "end": v(-28.1, -374.96) * mm});
            skLineSegment(sketch, "E1357", {"start": v(-28.1, -374.96) * mm, "end": v(-28.3, -374.93) * mm});
            skLineSegment(sketch, "E1358", {"start": v(-28.3, -374.93) * mm, "end": v(-28.5, -374.9) * mm});
            skLineSegment(sketch, "E1359", {"start": v(-28.5, -374.9) * mm, "end": v(-28.7, -374.9) * mm});
            skLineSegment(sketch, "E1360", {"start": v(-28.7, -374.9) * mm, "end": v(-28.9, -374.9) * mm});
            skLineSegment(sketch, "E1361", {"start": v(-28.9, -374.9) * mm, "end": v(-29.09, -374.93) * mm});
            skLineSegment(sketch, "E1362", {"start": v(-29.09, -374.93) * mm, "end": v(-29.28, -374.96) * mm});
            skLineSegment(sketch, "E1363", {"start": v(-29.28, -374.96) * mm, "end": v(-29.48, -375) * mm});
            skLineSegment(sketch, "E1364", {"start": v(-29.48, -375) * mm, "end": v(-29.67, -375.06) * mm});
            skLineSegment(sketch, "E1365", {"start": v(-29.67, -375.06) * mm, "end": v(-29.85, -375.13) * mm});
            skLineSegment(sketch, "E1366", {"start": v(-29.85, -375.13) * mm, "end": v(-30.03, -375.21) * mm});
            skLineSegment(sketch, "E1367", {"start": v(-30.03, -375.21) * mm, "end": v(-30.2, -375.3) * mm});
            skLineSegment(sketch, "E1368", {"start": v(-30.2, -375.3) * mm, "end": v(-30.38, -375.41) * mm});
            skLineSegment(sketch, "E1369", {"start": v(-30.38, -375.41) * mm, "end": v(-30.54, -375.53) * mm});
            skLineSegment(sketch, "E1370", {"start": v(-30.54, -375.53) * mm, "end": v(-30.7, -375.65) * mm});
            skLineSegment(sketch, "E1371", {"start": v(-30.7, -375.65) * mm, "end": v(-30.84, -375.79) * mm});
            skLineSegment(sketch, "E1372", {"start": v(-30.84, -375.79) * mm, "end": v(-30.97, -375.93) * mm});
            skLineSegment(sketch, "E1373", {"start": v(-30.97, -375.93) * mm, "end": v(-31.1, -376.09) * mm});
            skLineSegment(sketch, "E1374", {"start": v(-31.1, -376.09) * mm, "end": v(-31.22, -376.25) * mm});
            skLineSegment(sketch, "E1375", {"start": v(-31.22, -376.25) * mm, "end": v(-31.32, -376.42) * mm});
            skLineSegment(sketch, "E1376", {"start": v(-31.32, -376.42) * mm, "end": v(-31.41, -376.6) * mm});
            skLineSegment(sketch, "E1377", {"start": v(-31.41, -376.6) * mm, "end": v(-31.5, -376.77) * mm});
            skLineSegment(sketch, "E1378", {"start": v(-31.5, -376.77) * mm, "end": v(-31.57, -376.96) * mm});
            skLineSegment(sketch, "E1379", {"start": v(-31.57, -376.96) * mm, "end": v(-31.62, -377.15) * mm});
            skLineSegment(sketch, "E1380", {"start": v(-31.62, -377.15) * mm, "end": v(-31.67, -377.34) * mm});
            skLineSegment(sketch, "E1381", {"start": v(-31.67, -377.34) * mm, "end": v(-31.7, -377.54) * mm});
            skLineSegment(sketch, "E1382", {"start": v(-31.7, -377.54) * mm, "end": v(-31.72, -377.74) * mm});
            skLineSegment(sketch, "E1383", {"start": v(-31.72, -377.74) * mm, "end": v(-31.73, -377.93) * mm});
            skLineSegment(sketch, "E1384", {"start": v(-31.73, -377.93) * mm, "end": v(-31.72, -378.13) * mm});
            skLineSegment(sketch, "E1385", {"start": v(-31.72, -378.13) * mm, "end": v(-31.7, -378.33) * mm});
            skLineSegment(sketch, "E1386", {"start": v(-31.7, -378.33) * mm, "end": v(-31.67, -378.53) * mm});
            skLineSegment(sketch, "E1387", {"start": v(-31.67, -378.53) * mm, "end": v(-31.62, -378.72) * mm});
            skLineSegment(sketch, "E1388", {"start": v(-31.62, -378.72) * mm, "end": v(-31.57, -378.9) * mm});
            skLineSegment(sketch, "E1389", {"start": v(-31.57, -378.9) * mm, "end": v(-31.5, -379.1) * mm});
            skLineSegment(sketch, "E1390", {"start": v(-31.5, -379.1) * mm, "end": v(-31.41, -379.28) * mm});
            skLineSegment(sketch, "E1391", {"start": v(-31.41, -379.28) * mm, "end": v(-31.32, -379.45) * mm});
            skLineSegment(sketch, "E1392", {"start": v(-31.32, -379.45) * mm, "end": v(-31.22, -379.62) * mm});
            skLineSegment(sketch, "E1393", {"start": v(-31.22, -379.62) * mm, "end": v(-31.1, -379.78) * mm});
            skLineSegment(sketch, "E1394", {"start": v(-31.1, -379.78) * mm, "end": v(-30.97, -379.93) * mm});
            skLineSegment(sketch, "E1395", {"start": v(-30.97, -379.93) * mm, "end": v(-30.84, -380.08) * mm});
            skLineSegment(sketch, "E1396", {"start": v(-30.84, -380.08) * mm, "end": v(-30.7, -380.22) * mm});
            skLineSegment(sketch, "E1397", {"start": v(-30.7, -380.22) * mm, "end": v(-30.54, -380.34) * mm});
            skLineSegment(sketch, "E1398", {"start": v(-30.54, -380.34) * mm, "end": v(-30.38, -380.46) * mm});
            skLineSegment(sketch, "E1399", {"start": v(-30.38, -380.46) * mm, "end": v(-30.2, -380.56) * mm});
            skLineSegment(sketch, "E1400", {"start": v(-30.2, -380.56) * mm, "end": v(-30.03, -380.66) * mm});
            skLineSegment(sketch, "E1401", {"start": v(-30.03, -380.66) * mm, "end": v(-29.85, -380.74) * mm});
            skLineSegment(sketch, "E1402", {"start": v(-29.85, -380.74) * mm, "end": v(-29.67, -380.8) * mm});
            skLineSegment(sketch, "E1403", {"start": v(-29.67, -380.8) * mm, "end": v(-29.48, -380.87) * mm});
            skLineSegment(sketch, "E1404", {"start": v(-29.48, -380.87) * mm, "end": v(-29.28, -380.91) * mm});
            skLineSegment(sketch, "E1405", {"start": v(-29.28, -380.91) * mm, "end": v(-29.09, -380.94) * mm});
            skLineSegment(sketch, "E1406", {"start": v(-29.09, -380.94) * mm, "end": v(-28.9, -380.96) * mm});
            skLineSegment(sketch, "E1407", {"start": v(-28.9, -380.96) * mm, "end": v(-28.7, -380.97) * mm});
            skLineSegment(sketch, "E1408", {"start": v(-28.7, -380.97) * mm, "end": v(-28.5, -380.96) * mm});
            skLineSegment(sketch, "E1409", {"start": v(-28.5, -380.96) * mm, "end": v(-28.3, -380.94) * mm});
            skLineSegment(sketch, "E1410", {"start": v(-28.3, -380.94) * mm, "end": v(-28.1, -380.91) * mm});
            skLineSegment(sketch, "E1411", {"start": v(-28.1, -380.91) * mm, "end": v(-27.9, -380.87) * mm});
            skLineSegment(sketch, "E1412", {"start": v(-27.9, -380.87) * mm, "end": v(-27.72, -380.8) * mm});
            skLineSegment(sketch, "E1413", {"start": v(-27.72, -380.8) * mm, "end": v(-27.53, -380.74) * mm});
            skLineSegment(sketch, "E1414", {"start": v(-27.53, -380.74) * mm, "end": v(-27.35, -380.66) * mm});
            skLineSegment(sketch, "E1415", {"start": v(-27.35, -380.66) * mm, "end": v(-27.17, -380.56) * mm});
            skLineSegment(sketch, "E1416", {"start": v(-27.17, -380.56) * mm, "end": v(-27, -380.46) * mm});
            skLineSegment(sketch, "E1417", {"start": v(-27, -380.46) * mm, "end": v(-26.84, -380.34) * mm});
            skLineSegment(sketch, "E1418", {"start": v(-26.84, -380.34) * mm, "end": v(-26.7, -380.22) * mm});
            skLineSegment(sketch, "E1419", {"start": v(-26.7, -380.22) * mm, "end": v(-26.55, -380.08) * mm});
            skLineSegment(sketch, "E1420", {"start": v(-26.55, -380.08) * mm, "end": v(-26.41, -379.93) * mm});
            skLineSegment(sketch, "E1421", {"start": v(-26.41, -379.93) * mm, "end": v(-26.28, -379.78) * mm});
            skLineSegment(sketch, "E1422", {"start": v(-26.28, -379.78) * mm, "end": v(-26.17, -379.62) * mm});
            skLineSegment(sketch, "E1423", {"start": v(-26.17, -379.62) * mm, "end": v(-26.06, -379.45) * mm});
            skLineSegment(sketch, "E1424", {"start": v(-26.06, -379.45) * mm, "end": v(-25.97, -379.28) * mm});
            skLineSegment(sketch, "E1425", {"start": v(-25.97, -379.28) * mm, "end": v(-25.89, -379.1) * mm});
            skLineSegment(sketch, "E1426", {"start": v(-25.89, -379.1) * mm, "end": v(-25.82, -378.9) * mm});
            skLineSegment(sketch, "E1427", {"start": v(-25.82, -378.9) * mm, "end": v(-25.76, -378.72) * mm});
            skLineSegment(sketch, "E1428", {"start": v(-25.76, -378.72) * mm, "end": v(-25.72, -378.53) * mm});
            skLineSegment(sketch, "E1429", {"start": v(-25.72, -378.53) * mm, "end": v(-25.68, -378.33) * mm});
            skLineSegment(sketch, "E1430", {"start": v(-25.68, -378.33) * mm, "end": v(-25.66, -378.13) * mm});
            skLineSegment(sketch, "E1431", {"start": v(-25.66, -378.13) * mm, "end": v(-25.66, -377.93) * mm});
            skLineSegment(sketch, "E1432", {"start": v(-27.04, -377.93) * mm, "end": v(-27.04, -377.83) * mm});
            skLineSegment(sketch, "E1433", {"start": v(-27.04, -377.83) * mm, "end": v(-27.05, -377.72) * mm});
            skLineSegment(sketch, "E1434", {"start": v(-27.05, -377.72) * mm, "end": v(-27.07, -377.61) * mm});
            skLineSegment(sketch, "E1435", {"start": v(-27.07, -377.61) * mm, "end": v(-27.1, -377.5) * mm});
            skLineSegment(sketch, "E1436", {"start": v(-27.1, -377.5) * mm, "end": v(-27.12, -377.4) * mm});
            skLineSegment(sketch, "E1437", {"start": v(-27.12, -377.4) * mm, "end": v(-27.16, -377.3) * mm});
            skLineSegment(sketch, "E1438", {"start": v(-27.16, -377.3) * mm, "end": v(-27.2, -377.2) * mm});
            skLineSegment(sketch, "E1439", {"start": v(-27.2, -377.2) * mm, "end": v(-27.26, -377.1) * mm});
            skLineSegment(sketch, "E1440", {"start": v(-27.26, -377.1) * mm, "end": v(-27.32, -377.01) * mm});
            skLineSegment(sketch, "E1441", {"start": v(-27.32, -377.01) * mm, "end": v(-27.38, -376.93) * mm});
            skLineSegment(sketch, "E1442", {"start": v(-27.38, -376.93) * mm, "end": v(-27.45, -376.84) * mm});
            skLineSegment(sketch, "E1443", {"start": v(-27.45, -376.84) * mm, "end": v(-27.52, -376.76) * mm});
            skLineSegment(sketch, "E1444", {"start": v(-27.52, -376.76) * mm, "end": v(-27.6, -376.69) * mm});
            skLineSegment(sketch, "E1445", {"start": v(-27.6, -376.69) * mm, "end": v(-27.68, -376.62) * mm});
            skLineSegment(sketch, "E1446", {"start": v(-27.68, -376.62) * mm, "end": v(-27.77, -376.56) * mm});
            skLineSegment(sketch, "E1447", {"start": v(-27.77, -376.56) * mm, "end": v(-27.86, -376.5) * mm});
            skLineSegment(sketch, "E1448", {"start": v(-27.86, -376.5) * mm, "end": v(-27.96, -376.45) * mm});
            skLineSegment(sketch, "E1449", {"start": v(-27.96, -376.45) * mm, "end": v(-28.06, -376.4) * mm});
            skLineSegment(sketch, "E1450", {"start": v(-28.06, -376.4) * mm, "end": v(-28.16, -376.37) * mm});
            skLineSegment(sketch, "E1451", {"start": v(-28.16, -376.37) * mm, "end": v(-28.26, -376.33) * mm});
            skLineSegment(sketch, "E1452", {"start": v(-28.26, -376.33) * mm, "end": v(-28.37, -376.31) * mm});
            skLineSegment(sketch, "E1453", {"start": v(-28.37, -376.31) * mm, "end": v(-28.48, -376.3) * mm});
            skLineSegment(sketch, "E1454", {"start": v(-28.48, -376.3) * mm, "end": v(-28.58, -376.28) * mm});
            skLineSegment(sketch, "E1455", {"start": v(-28.58, -376.28) * mm, "end": v(-28.7, -376.28) * mm});
            skLineSegment(sketch, "E1456", {"start": v(-28.7, -376.28) * mm, "end": v(-28.8, -376.28) * mm});
            skLineSegment(sketch, "E1457", {"start": v(-28.8, -376.28) * mm, "end": v(-28.9, -376.3) * mm});
            skLineSegment(sketch, "E1458", {"start": v(-28.9, -376.3) * mm, "end": v(-29.01, -376.31) * mm});
            skLineSegment(sketch, "E1459", {"start": v(-29.01, -376.31) * mm, "end": v(-29.12, -376.33) * mm});
            skLineSegment(sketch, "E1460", {"start": v(-29.12, -376.33) * mm, "end": v(-29.22, -376.37) * mm});
            skLineSegment(sketch, "E1461", {"start": v(-29.22, -376.37) * mm, "end": v(-29.33, -376.4) * mm});
            skLineSegment(sketch, "E1462", {"start": v(-29.33, -376.4) * mm, "end": v(-29.42, -376.45) * mm});
            skLineSegment(sketch, "E1463", {"start": v(-29.42, -376.45) * mm, "end": v(-29.52, -376.5) * mm});
            skLineSegment(sketch, "E1464", {"start": v(-29.52, -376.5) * mm, "end": v(-29.61, -376.56) * mm});
            skLineSegment(sketch, "E1465", {"start": v(-29.61, -376.56) * mm, "end": v(-29.7, -376.62) * mm});
            skLineSegment(sketch, "E1466", {"start": v(-29.7, -376.62) * mm, "end": v(-29.78, -376.69) * mm});
            skLineSegment(sketch, "E1467", {"start": v(-29.78, -376.69) * mm, "end": v(-29.86, -376.76) * mm});
            skLineSegment(sketch, "E1468", {"start": v(-29.86, -376.76) * mm, "end": v(-29.94, -376.84) * mm});
            skLineSegment(sketch, "E1469", {"start": v(-29.94, -376.84) * mm, "end": v(-30, -376.93) * mm});
            skLineSegment(sketch, "E1470", {"start": v(-30, -376.93) * mm, "end": v(-30.07, -377.01) * mm});
            skLineSegment(sketch, "E1471", {"start": v(-30.07, -377.01) * mm, "end": v(-30.13, -377.1) * mm});
            skLineSegment(sketch, "E1472", {"start": v(-30.13, -377.1) * mm, "end": v(-30.18, -377.2) * mm});
            skLineSegment(sketch, "E1473", {"start": v(-30.18, -377.2) * mm, "end": v(-30.22, -377.3) * mm});
            skLineSegment(sketch, "E1474", {"start": v(-30.22, -377.3) * mm, "end": v(-30.26, -377.4) * mm});
            skLineSegment(sketch, "E1475", {"start": v(-30.26, -377.4) * mm, "end": v(-30.3, -377.5) * mm});
            skLineSegment(sketch, "E1476", {"start": v(-30.3, -377.5) * mm, "end": v(-30.32, -377.61) * mm});
            skLineSegment(sketch, "E1477", {"start": v(-30.32, -377.61) * mm, "end": v(-30.33, -377.72) * mm});
            skLineSegment(sketch, "E1478", {"start": v(-30.33, -377.72) * mm, "end": v(-30.34, -377.83) * mm});
            skLineSegment(sketch, "E1479", {"start": v(-30.34, -377.83) * mm, "end": v(-30.35, -377.93) * mm});
            skLineSegment(sketch, "E1480", {"start": v(-30.35, -377.93) * mm, "end": v(-30.34, -378.04) * mm});
            skLineSegment(sketch, "E1481", {"start": v(-30.34, -378.04) * mm, "end": v(-30.33, -378.15) * mm});
            skLineSegment(sketch, "E1482", {"start": v(-30.33, -378.15) * mm, "end": v(-30.32, -378.26) * mm});
            skLineSegment(sketch, "E1483", {"start": v(-30.32, -378.26) * mm, "end": v(-30.3, -378.36) * mm});
            skLineSegment(sketch, "E1484", {"start": v(-30.3, -378.36) * mm, "end": v(-30.26, -378.47) * mm});
            skLineSegment(sketch, "E1485", {"start": v(-30.26, -378.47) * mm, "end": v(-30.22, -378.57) * mm});
            skLineSegment(sketch, "E1486", {"start": v(-30.22, -378.57) * mm, "end": v(-30.18, -378.67) * mm});
            skLineSegment(sketch, "E1487", {"start": v(-30.18, -378.67) * mm, "end": v(-30.13, -378.76) * mm});
            skLineSegment(sketch, "E1488", {"start": v(-30.13, -378.76) * mm, "end": v(-30.07, -378.85) * mm});
            skLineSegment(sketch, "E1489", {"start": v(-30.07, -378.85) * mm, "end": v(-30, -378.94) * mm});
            skLineSegment(sketch, "E1490", {"start": v(-30, -378.94) * mm, "end": v(-29.94, -379.03) * mm});
            skLineSegment(sketch, "E1491", {"start": v(-29.94, -379.03) * mm, "end": v(-29.86, -379.1) * mm});
            skLineSegment(sketch, "E1492", {"start": v(-29.86, -379.1) * mm, "end": v(-29.78, -379.18) * mm});
            skLineSegment(sketch, "E1493", {"start": v(-29.78, -379.18) * mm, "end": v(-29.7, -379.25) * mm});
            skLineSegment(sketch, "E1494", {"start": v(-29.7, -379.25) * mm, "end": v(-29.61, -379.31) * mm});
            skLineSegment(sketch, "E1495", {"start": v(-29.61, -379.31) * mm, "end": v(-29.52, -379.37) * mm});
            skLineSegment(sketch, "E1496", {"start": v(-29.52, -379.37) * mm, "end": v(-29.42, -379.42) * mm});
            skLineSegment(sketch, "E1497", {"start": v(-29.42, -379.42) * mm, "end": v(-29.33, -379.46) * mm});
            skLineSegment(sketch, "E1498", {"start": v(-29.33, -379.46) * mm, "end": v(-29.22, -379.5) * mm});
            skLineSegment(sketch, "E1499", {"start": v(-29.22, -379.5) * mm, "end": v(-29.12, -379.53) * mm});
            skLineSegment(sketch, "E1500", {"start": v(-29.12, -379.53) * mm, "end": v(-29.01, -379.56) * mm});
            skLineSegment(sketch, "E1501", {"start": v(-29.01, -379.56) * mm, "end": v(-28.9, -379.58) * mm});
            skLineSegment(sketch, "E1502", {"start": v(-28.9, -379.58) * mm, "end": v(-28.8, -379.59) * mm});
            skLineSegment(sketch, "E1503", {"start": v(-28.8, -379.59) * mm, "end": v(-28.7, -379.59) * mm});
            skLineSegment(sketch, "E1504", {"start": v(-28.7, -379.59) * mm, "end": v(-28.58, -379.59) * mm});
            skLineSegment(sketch, "E1505", {"start": v(-28.58, -379.59) * mm, "end": v(-28.48, -379.58) * mm});
            skLineSegment(sketch, "E1506", {"start": v(-28.48, -379.58) * mm, "end": v(-28.37, -379.56) * mm});
            skLineSegment(sketch, "E1507", {"start": v(-28.37, -379.56) * mm, "end": v(-28.26, -379.53) * mm});
            skLineSegment(sketch, "E1508", {"start": v(-28.26, -379.53) * mm, "end": v(-28.16, -379.5) * mm});
            skLineSegment(sketch, "E1509", {"start": v(-28.16, -379.5) * mm, "end": v(-28.06, -379.46) * mm});
            skLineSegment(sketch, "E1510", {"start": v(-28.06, -379.46) * mm, "end": v(-27.96, -379.42) * mm});
            skLineSegment(sketch, "E1511", {"start": v(-27.96, -379.42) * mm, "end": v(-27.86, -379.37) * mm});
            skLineSegment(sketch, "E1512", {"start": v(-27.86, -379.37) * mm, "end": v(-27.77, -379.31) * mm});
            skLineSegment(sketch, "E1513", {"start": v(-27.77, -379.31) * mm, "end": v(-27.68, -379.25) * mm});
            skLineSegment(sketch, "E1514", {"start": v(-27.68, -379.25) * mm, "end": v(-27.6, -379.18) * mm});
            skLineSegment(sketch, "E1515", {"start": v(-27.6, -379.18) * mm, "end": v(-27.52, -379.1) * mm});
            skLineSegment(sketch, "E1516", {"start": v(-27.52, -379.1) * mm, "end": v(-27.45, -379.03) * mm});
            skLineSegment(sketch, "E1517", {"start": v(-27.45, -379.03) * mm, "end": v(-27.38, -378.94) * mm});
            skLineSegment(sketch, "E1518", {"start": v(-27.38, -378.94) * mm, "end": v(-27.32, -378.85) * mm});
            skLineSegment(sketch, "E1519", {"start": v(-27.32, -378.85) * mm, "end": v(-27.26, -378.76) * mm});
            skLineSegment(sketch, "E1520", {"start": v(-27.26, -378.76) * mm, "end": v(-27.2, -378.67) * mm});
            skLineSegment(sketch, "E1521", {"start": v(-27.2, -378.67) * mm, "end": v(-27.16, -378.57) * mm});
            skLineSegment(sketch, "E1522", {"start": v(-27.16, -378.57) * mm, "end": v(-27.12, -378.47) * mm});
            skLineSegment(sketch, "E1523", {"start": v(-27.12, -378.47) * mm, "end": v(-27.1, -378.36) * mm});
            skLineSegment(sketch, "E1524", {"start": v(-27.1, -378.36) * mm, "end": v(-27.07, -378.26) * mm});
            skLineSegment(sketch, "E1525", {"start": v(-27.07, -378.26) * mm, "end": v(-27.05, -378.15) * mm});
            skLineSegment(sketch, "E1526", {"start": v(-27.05, -378.15) * mm, "end": v(-27.04, -378.04) * mm});
            skLineSegment(sketch, "E1527", {"start": v(-27.04, -378.04) * mm, "end": v(-27.04, -377.93) * mm});
            skLineSegment(sketch, "E1528", {"start": v(20.25, -377.93) * mm, "end": v(20.24, -377.74) * mm});
            skLineSegment(sketch, "E1529", {"start": v(20.24, -377.74) * mm, "end": v(20.22, -377.54) * mm});
            skLineSegment(sketch, "E1530", {"start": v(20.22, -377.54) * mm, "end": v(20.2, -377.34) * mm});
            skLineSegment(sketch, "E1531", {"start": v(20.2, -377.34) * mm, "end": v(20.15, -377.15) * mm});
            skLineSegment(sketch, "E1532", {"start": v(20.15, -377.15) * mm, "end": v(20.09, -376.96) * mm});
            skLineSegment(sketch, "E1533", {"start": v(20.09, -376.96) * mm, "end": v(20.02, -376.77) * mm});
            skLineSegment(sketch, "E1534", {"start": v(20.02, -376.77) * mm, "end": v(19.94, -376.6) * mm});
            skLineSegment(sketch, "E1535", {"start": v(19.94, -376.6) * mm, "end": v(19.84, -376.42) * mm});
            skLineSegment(sketch, "E1536", {"start": v(19.84, -376.42) * mm, "end": v(19.74, -376.25) * mm});
            skLineSegment(sketch, "E1537", {"start": v(19.74, -376.25) * mm, "end": v(19.62, -376.09) * mm});
            skLineSegment(sketch, "E1538", {"start": v(19.62, -376.09) * mm, "end": v(19.5, -375.93) * mm});
            skLineSegment(sketch, "E1539", {"start": v(19.5, -375.93) * mm, "end": v(19.36, -375.79) * mm});
            skLineSegment(sketch, "E1540", {"start": v(19.36, -375.79) * mm, "end": v(19.22, -375.65) * mm});
            skLineSegment(sketch, "E1541", {"start": v(19.22, -375.65) * mm, "end": v(19.06, -375.53) * mm});
            skLineSegment(sketch, "E1542", {"start": v(19.06, -375.53) * mm, "end": v(18.9, -375.41) * mm});
            skLineSegment(sketch, "E1543", {"start": v(18.9, -375.41) * mm, "end": v(18.73, -375.3) * mm});
            skLineSegment(sketch, "E1544", {"start": v(18.73, -375.3) * mm, "end": v(18.56, -375.21) * mm});
            skLineSegment(sketch, "E1545", {"start": v(18.56, -375.21) * mm, "end": v(18.38, -375.13) * mm});
            skLineSegment(sketch, "E1546", {"start": v(18.38, -375.13) * mm, "end": v(18.2, -375.06) * mm});
            skLineSegment(sketch, "E1547", {"start": v(18.2, -375.06) * mm, "end": v(18, -375) * mm});
            skLineSegment(sketch, "E1548", {"start": v(18, -375) * mm, "end": v(17.8, -374.96) * mm});
            skLineSegment(sketch, "E1549", {"start": v(17.8, -374.96) * mm, "end": v(17.61, -374.93) * mm});
            skLineSegment(sketch, "E1550", {"start": v(17.61, -374.93) * mm, "end": v(17.41, -374.9) * mm});
            skLineSegment(sketch, "E1551", {"start": v(17.41, -374.9) * mm, "end": v(17.22, -374.9) * mm});
            skLineSegment(sketch, "E1552", {"start": v(17.22, -374.9) * mm, "end": v(17.02, -374.9) * mm});
            skLineSegment(sketch, "E1553", {"start": v(17.02, -374.9) * mm, "end": v(16.82, -374.93) * mm});
            skLineSegment(sketch, "E1554", {"start": v(16.82, -374.93) * mm, "end": v(16.62, -374.96) * mm});
            skLineSegment(sketch, "E1555", {"start": v(16.62, -374.96) * mm, "end": v(16.43, -375) * mm});
            skLineSegment(sketch, "E1556", {"start": v(16.43, -375) * mm, "end": v(16.24, -375.06) * mm});
            skLineSegment(sketch, "E1557", {"start": v(16.24, -375.06) * mm, "end": v(16.05, -375.13) * mm});
            skLineSegment(sketch, "E1558", {"start": v(16.05, -375.13) * mm, "end": v(15.87, -375.21) * mm});
            skLineSegment(sketch, "E1559", {"start": v(15.87, -375.21) * mm, "end": v(15.7, -375.3) * mm});
            skLineSegment(sketch, "E1560", {"start": v(15.7, -375.3) * mm, "end": v(15.53, -375.41) * mm});
            skLineSegment(sketch, "E1561", {"start": v(15.53, -375.41) * mm, "end": v(15.37, -375.53) * mm});
            skLineSegment(sketch, "E1562", {"start": v(15.37, -375.53) * mm, "end": v(15.21, -375.65) * mm});
            skLineSegment(sketch, "E1563", {"start": v(15.21, -375.65) * mm, "end": v(15.07, -375.79) * mm});
            skLineSegment(sketch, "E1564", {"start": v(15.07, -375.79) * mm, "end": v(14.93, -375.93) * mm});
            skLineSegment(sketch, "E1565", {"start": v(14.93, -375.93) * mm, "end": v(14.8, -376.09) * mm});
            skLineSegment(sketch, "E1566", {"start": v(14.8, -376.09) * mm, "end": v(14.7, -376.25) * mm});
            skLineSegment(sketch, "E1567", {"start": v(14.7, -376.25) * mm, "end": v(14.59, -376.42) * mm});
            skLineSegment(sketch, "E1568", {"start": v(14.59, -376.42) * mm, "end": v(14.5, -376.6) * mm});
            skLineSegment(sketch, "E1569", {"start": v(14.5, -376.6) * mm, "end": v(14.41, -376.77) * mm});
            skLineSegment(sketch, "E1570", {"start": v(14.41, -376.77) * mm, "end": v(14.34, -376.96) * mm});
            skLineSegment(sketch, "E1571", {"start": v(14.34, -376.96) * mm, "end": v(14.28, -377.15) * mm});
            skLineSegment(sketch, "E1572", {"start": v(14.28, -377.15) * mm, "end": v(14.24, -377.34) * mm});
            skLineSegment(sketch, "E1573", {"start": v(14.24, -377.34) * mm, "end": v(14.2, -377.54) * mm});
            skLineSegment(sketch, "E1574", {"start": v(14.2, -377.54) * mm, "end": v(14.19, -377.74) * mm});
            skLineSegment(sketch, "E1575", {"start": v(14.19, -377.74) * mm, "end": v(14.18, -377.93) * mm});
            skLineSegment(sketch, "E1576", {"start": v(14.18, -377.93) * mm, "end": v(14.19, -378.13) * mm});
            skLineSegment(sketch, "E1577", {"start": v(14.19, -378.13) * mm, "end": v(14.2, -378.33) * mm});
            skLineSegment(sketch, "E1578", {"start": v(14.2, -378.33) * mm, "end": v(14.24, -378.53) * mm});
            skLineSegment(sketch, "E1579", {"start": v(14.24, -378.53) * mm, "end": v(14.28, -378.72) * mm});
            skLineSegment(sketch, "E1580", {"start": v(14.28, -378.72) * mm, "end": v(14.34, -378.9) * mm});
            skLineSegment(sketch, "E1581", {"start": v(14.34, -378.9) * mm, "end": v(14.41, -379.1) * mm});
            skLineSegment(sketch, "E1582", {"start": v(14.41, -379.1) * mm, "end": v(14.5, -379.28) * mm});
            skLineSegment(sketch, "E1583", {"start": v(14.5, -379.28) * mm, "end": v(14.59, -379.45) * mm});
            skLineSegment(sketch, "E1584", {"start": v(14.59, -379.45) * mm, "end": v(14.7, -379.62) * mm});
            skLineSegment(sketch, "E1585", {"start": v(14.7, -379.62) * mm, "end": v(14.8, -379.78) * mm});
            skLineSegment(sketch, "E1586", {"start": v(14.8, -379.78) * mm, "end": v(14.93, -379.93) * mm});
            skLineSegment(sketch, "E1587", {"start": v(14.93, -379.93) * mm, "end": v(15.07, -380.08) * mm});
            skLineSegment(sketch, "E1588", {"start": v(15.07, -380.08) * mm, "end": v(15.21, -380.22) * mm});
            skLineSegment(sketch, "E1589", {"start": v(15.21, -380.22) * mm, "end": v(15.37, -380.34) * mm});
            skLineSegment(sketch, "E1590", {"start": v(15.37, -380.34) * mm, "end": v(15.53, -380.46) * mm});
            skLineSegment(sketch, "E1591", {"start": v(15.53, -380.46) * mm, "end": v(15.7, -380.56) * mm});
            skLineSegment(sketch, "E1592", {"start": v(15.7, -380.56) * mm, "end": v(15.87, -380.66) * mm});
            skLineSegment(sketch, "E1593", {"start": v(15.87, -380.66) * mm, "end": v(16.05, -380.74) * mm});
            skLineSegment(sketch, "E1594", {"start": v(16.05, -380.74) * mm, "end": v(16.24, -380.8) * mm});
            skLineSegment(sketch, "E1595", {"start": v(16.24, -380.8) * mm, "end": v(16.43, -380.87) * mm});
            skLineSegment(sketch, "E1596", {"start": v(16.43, -380.87) * mm, "end": v(16.62, -380.91) * mm});
            skLineSegment(sketch, "E1597", {"start": v(16.62, -380.91) * mm, "end": v(16.82, -380.94) * mm});
            skLineSegment(sketch, "E1598", {"start": v(16.82, -380.94) * mm, "end": v(17.02, -380.96) * mm});
            skLineSegment(sketch, "E1599", {"start": v(17.02, -380.96) * mm, "end": v(17.22, -380.97) * mm});
            skLineSegment(sketch, "E1600", {"start": v(17.22, -380.97) * mm, "end": v(17.41, -380.96) * mm});
            skLineSegment(sketch, "E1601", {"start": v(17.41, -380.96) * mm, "end": v(17.61, -380.94) * mm});
            skLineSegment(sketch, "E1602", {"start": v(17.61, -380.94) * mm, "end": v(17.8, -380.91) * mm});
            skLineSegment(sketch, "E1603", {"start": v(17.8, -380.91) * mm, "end": v(18, -380.87) * mm});
            skLineSegment(sketch, "E1604", {"start": v(18, -380.87) * mm, "end": v(18.2, -380.8) * mm});
            skLineSegment(sketch, "E1605", {"start": v(18.2, -380.8) * mm, "end": v(18.38, -380.74) * mm});
            skLineSegment(sketch, "E1606", {"start": v(18.38, -380.74) * mm, "end": v(18.56, -380.66) * mm});
            skLineSegment(sketch, "E1607", {"start": v(18.56, -380.66) * mm, "end": v(18.73, -380.56) * mm});
            skLineSegment(sketch, "E1608", {"start": v(18.73, -380.56) * mm, "end": v(18.9, -380.46) * mm});
            skLineSegment(sketch, "E1609", {"start": v(18.9, -380.46) * mm, "end": v(19.06, -380.34) * mm});
            skLineSegment(sketch, "E1610", {"start": v(19.06, -380.34) * mm, "end": v(19.22, -380.22) * mm});
            skLineSegment(sketch, "E1611", {"start": v(19.22, -380.22) * mm, "end": v(19.36, -380.08) * mm});
            skLineSegment(sketch, "E1612", {"start": v(19.36, -380.08) * mm, "end": v(19.5, -379.93) * mm});
            skLineSegment(sketch, "E1613", {"start": v(19.5, -379.93) * mm, "end": v(19.62, -379.78) * mm});
            skLineSegment(sketch, "E1614", {"start": v(19.62, -379.78) * mm, "end": v(19.74, -379.62) * mm});
            skLineSegment(sketch, "E1615", {"start": v(19.74, -379.62) * mm, "end": v(19.84, -379.45) * mm});
            skLineSegment(sketch, "E1616", {"start": v(19.84, -379.45) * mm, "end": v(19.94, -379.28) * mm});
            skLineSegment(sketch, "E1617", {"start": v(19.94, -379.28) * mm, "end": v(20.02, -379.1) * mm});
            skLineSegment(sketch, "E1618", {"start": v(20.02, -379.1) * mm, "end": v(20.09, -378.9) * mm});
            skLineSegment(sketch, "E1619", {"start": v(20.09, -378.9) * mm, "end": v(20.15, -378.72) * mm});
            skLineSegment(sketch, "E1620", {"start": v(20.15, -378.72) * mm, "end": v(20.2, -378.53) * mm});
            skLineSegment(sketch, "E1621", {"start": v(20.2, -378.53) * mm, "end": v(20.22, -378.33) * mm});
            skLineSegment(sketch, "E1622", {"start": v(20.22, -378.33) * mm, "end": v(20.24, -378.13) * mm});
            skLineSegment(sketch, "E1623", {"start": v(20.24, -378.13) * mm, "end": v(20.25, -377.93) * mm});
            skLineSegment(sketch, "E1624", {"start": v(18.87, -377.93) * mm, "end": v(18.87, -377.83) * mm});
            skLineSegment(sketch, "E1625", {"start": v(18.87, -377.83) * mm, "end": v(18.86, -377.72) * mm});
            skLineSegment(sketch, "E1626", {"start": v(18.86, -377.72) * mm, "end": v(18.84, -377.61) * mm});
            skLineSegment(sketch, "E1627", {"start": v(18.84, -377.61) * mm, "end": v(18.81, -377.5) * mm});
            skLineSegment(sketch, "E1628", {"start": v(18.81, -377.5) * mm, "end": v(18.78, -377.4) * mm});
            skLineSegment(sketch, "E1629", {"start": v(18.78, -377.4) * mm, "end": v(18.74, -377.3) * mm});
            skLineSegment(sketch, "E1630", {"start": v(18.74, -377.3) * mm, "end": v(18.7, -377.2) * mm});
            skLineSegment(sketch, "E1631", {"start": v(18.7, -377.2) * mm, "end": v(18.65, -377.1) * mm});
            skLineSegment(sketch, "E1632", {"start": v(18.65, -377.1) * mm, "end": v(18.6, -377.01) * mm});
            skLineSegment(sketch, "E1633", {"start": v(18.6, -377.01) * mm, "end": v(18.53, -376.93) * mm});
            skLineSegment(sketch, "E1634", {"start": v(18.53, -376.93) * mm, "end": v(18.46, -376.84) * mm});
            skLineSegment(sketch, "E1635", {"start": v(18.46, -376.84) * mm, "end": v(18.39, -376.76) * mm});
            skLineSegment(sketch, "E1636", {"start": v(18.39, -376.76) * mm, "end": v(18.3, -376.69) * mm});
            skLineSegment(sketch, "E1637", {"start": v(18.3, -376.69) * mm, "end": v(18.22, -376.62) * mm});
            skLineSegment(sketch, "E1638", {"start": v(18.22, -376.62) * mm, "end": v(18.13, -376.56) * mm});
            skLineSegment(sketch, "E1639", {"start": v(18.13, -376.56) * mm, "end": v(18.04, -376.5) * mm});
            skLineSegment(sketch, "E1640", {"start": v(18.04, -376.5) * mm, "end": v(17.95, -376.45) * mm});
            skLineSegment(sketch, "E1641", {"start": v(17.95, -376.45) * mm, "end": v(17.85, -376.4) * mm});
            skLineSegment(sketch, "E1642", {"start": v(17.85, -376.4) * mm, "end": v(17.75, -376.37) * mm});
            skLineSegment(sketch, "E1643", {"start": v(17.75, -376.37) * mm, "end": v(17.64, -376.33) * mm});
            skLineSegment(sketch, "E1644", {"start": v(17.64, -376.33) * mm, "end": v(17.54, -376.31) * mm});
            skLineSegment(sketch, "E1645", {"start": v(17.54, -376.31) * mm, "end": v(17.43, -376.3) * mm});
            skLineSegment(sketch, "E1646", {"start": v(17.43, -376.3) * mm, "end": v(17.32, -376.28) * mm});
            skLineSegment(sketch, "E1647", {"start": v(17.32, -376.28) * mm, "end": v(17.22, -376.28) * mm});
            skLineSegment(sketch, "E1648", {"start": v(17.22, -376.28) * mm, "end": v(17.1, -376.28) * mm});
            skLineSegment(sketch, "E1649", {"start": v(17.1, -376.28) * mm, "end": v(17, -376.3) * mm});
            skLineSegment(sketch, "E1650", {"start": v(17, -376.3) * mm, "end": v(16.9, -376.31) * mm});
            skLineSegment(sketch, "E1651", {"start": v(16.9, -376.31) * mm, "end": v(16.79, -376.33) * mm});
            skLineSegment(sketch, "E1652", {"start": v(16.79, -376.33) * mm, "end": v(16.68, -376.37) * mm});
            skLineSegment(sketch, "E1653", {"start": v(16.68, -376.37) * mm, "end": v(16.58, -376.4) * mm});
            skLineSegment(sketch, "E1654", {"start": v(16.58, -376.4) * mm, "end": v(16.48, -376.45) * mm});
            skLineSegment(sketch, "E1655", {"start": v(16.48, -376.45) * mm, "end": v(16.39, -376.5) * mm});
            skLineSegment(sketch, "E1656", {"start": v(16.39, -376.5) * mm, "end": v(16.3, -376.56) * mm});
            skLineSegment(sketch, "E1657", {"start": v(16.3, -376.56) * mm, "end": v(16.2, -376.62) * mm});
            skLineSegment(sketch, "E1658", {"start": v(16.2, -376.62) * mm, "end": v(16.12, -376.69) * mm});
            skLineSegment(sketch, "E1659", {"start": v(16.12, -376.69) * mm, "end": v(16.04, -376.76) * mm});
            skLineSegment(sketch, "E1660", {"start": v(16.04, -376.76) * mm, "end": v(15.97, -376.84) * mm});
            skLineSegment(sketch, "E1661", {"start": v(15.97, -376.84) * mm, "end": v(15.9, -376.93) * mm});
            skLineSegment(sketch, "E1662", {"start": v(15.9, -376.93) * mm, "end": v(15.84, -377.01) * mm});
            skLineSegment(sketch, "E1663", {"start": v(15.84, -377.01) * mm, "end": v(15.78, -377.1) * mm});
            skLineSegment(sketch, "E1664", {"start": v(15.78, -377.1) * mm, "end": v(15.73, -377.2) * mm});
            skLineSegment(sketch, "E1665", {"start": v(15.73, -377.2) * mm, "end": v(15.69, -377.3) * mm});
            skLineSegment(sketch, "E1666", {"start": v(15.69, -377.3) * mm, "end": v(15.65, -377.4) * mm});
            skLineSegment(sketch, "E1667", {"start": v(15.65, -377.4) * mm, "end": v(15.62, -377.5) * mm});
            skLineSegment(sketch, "E1668", {"start": v(15.62, -377.5) * mm, "end": v(15.6, -377.61) * mm});
            skLineSegment(sketch, "E1669", {"start": v(15.6, -377.61) * mm, "end": v(15.57, -377.72) * mm});
            skLineSegment(sketch, "E1670", {"start": v(15.57, -377.72) * mm, "end": v(15.56, -377.83) * mm});
            skLineSegment(sketch, "E1671", {"start": v(15.56, -377.83) * mm, "end": v(15.56, -377.93) * mm});
            skLineSegment(sketch, "E1672", {"start": v(15.56, -377.93) * mm, "end": v(15.56, -378.04) * mm});
            skLineSegment(sketch, "E1673", {"start": v(15.56, -378.04) * mm, "end": v(15.57, -378.15) * mm});
            skLineSegment(sketch, "E1674", {"start": v(15.57, -378.15) * mm, "end": v(15.6, -378.26) * mm});
            skLineSegment(sketch, "E1675", {"start": v(15.6, -378.26) * mm, "end": v(15.62, -378.36) * mm});
            skLineSegment(sketch, "E1676", {"start": v(15.62, -378.36) * mm, "end": v(15.65, -378.47) * mm});
            skLineSegment(sketch, "E1677", {"start": v(15.65, -378.47) * mm, "end": v(15.69, -378.57) * mm});
            skLineSegment(sketch, "E1678", {"start": v(15.69, -378.57) * mm, "end": v(15.73, -378.67) * mm});
            skLineSegment(sketch, "E1679", {"start": v(15.73, -378.67) * mm, "end": v(15.78, -378.76) * mm});
            skLineSegment(sketch, "E1680", {"start": v(15.78, -378.76) * mm, "end": v(15.84, -378.85) * mm});
            skLineSegment(sketch, "E1681", {"start": v(15.84, -378.85) * mm, "end": v(15.9, -378.94) * mm});
            skLineSegment(sketch, "E1682", {"start": v(15.9, -378.94) * mm, "end": v(15.97, -379.03) * mm});
            skLineSegment(sketch, "E1683", {"start": v(15.97, -379.03) * mm, "end": v(16.04, -379.1) * mm});
            skLineSegment(sketch, "E1684", {"start": v(16.04, -379.1) * mm, "end": v(16.12, -379.18) * mm});
            skLineSegment(sketch, "E1685", {"start": v(16.12, -379.18) * mm, "end": v(16.2, -379.25) * mm});
            skLineSegment(sketch, "E1686", {"start": v(16.2, -379.25) * mm, "end": v(16.3, -379.31) * mm});
            skLineSegment(sketch, "E1687", {"start": v(16.3, -379.31) * mm, "end": v(16.39, -379.37) * mm});
            skLineSegment(sketch, "E1688", {"start": v(16.39, -379.37) * mm, "end": v(16.48, -379.42) * mm});
            skLineSegment(sketch, "E1689", {"start": v(16.48, -379.42) * mm, "end": v(16.58, -379.46) * mm});
            skLineSegment(sketch, "E1690", {"start": v(16.58, -379.46) * mm, "end": v(16.68, -379.5) * mm});
            skLineSegment(sketch, "E1691", {"start": v(16.68, -379.5) * mm, "end": v(16.79, -379.53) * mm});
            skLineSegment(sketch, "E1692", {"start": v(16.79, -379.53) * mm, "end": v(16.9, -379.56) * mm});
            skLineSegment(sketch, "E1693", {"start": v(16.9, -379.56) * mm, "end": v(17, -379.58) * mm});
            skLineSegment(sketch, "E1694", {"start": v(17, -379.58) * mm, "end": v(17.1, -379.59) * mm});
            skLineSegment(sketch, "E1695", {"start": v(17.1, -379.59) * mm, "end": v(17.22, -379.59) * mm});
            skLineSegment(sketch, "E1696", {"start": v(17.22, -379.59) * mm, "end": v(17.32, -379.59) * mm});
            skLineSegment(sketch, "E1697", {"start": v(17.32, -379.59) * mm, "end": v(17.43, -379.58) * mm});
            skLineSegment(sketch, "E1698", {"start": v(17.43, -379.58) * mm, "end": v(17.54, -379.56) * mm});
            skLineSegment(sketch, "E1699", {"start": v(17.54, -379.56) * mm, "end": v(17.64, -379.53) * mm});
            skLineSegment(sketch, "E1700", {"start": v(17.64, -379.53) * mm, "end": v(17.75, -379.5) * mm});
            skLineSegment(sketch, "E1701", {"start": v(17.75, -379.5) * mm, "end": v(17.85, -379.46) * mm});
            skLineSegment(sketch, "E1702", {"start": v(17.85, -379.46) * mm, "end": v(17.95, -379.42) * mm});
            skLineSegment(sketch, "E1703", {"start": v(17.95, -379.42) * mm, "end": v(18.04, -379.37) * mm});
            skLineSegment(sketch, "E1704", {"start": v(18.04, -379.37) * mm, "end": v(18.13, -379.31) * mm});
            skLineSegment(sketch, "E1705", {"start": v(18.13, -379.31) * mm, "end": v(18.22, -379.25) * mm});
            skLineSegment(sketch, "E1706", {"start": v(18.22, -379.25) * mm, "end": v(18.3, -379.18) * mm});
            skLineSegment(sketch, "E1707", {"start": v(18.3, -379.18) * mm, "end": v(18.39, -379.1) * mm});
            skLineSegment(sketch, "E1708", {"start": v(18.39, -379.1) * mm, "end": v(18.46, -379.03) * mm});
            skLineSegment(sketch, "E1709", {"start": v(18.46, -379.03) * mm, "end": v(18.53, -378.94) * mm});
            skLineSegment(sketch, "E1710", {"start": v(18.53, -378.94) * mm, "end": v(18.6, -378.85) * mm});
            skLineSegment(sketch, "E1711", {"start": v(18.6, -378.85) * mm, "end": v(18.65, -378.76) * mm});
            skLineSegment(sketch, "E1712", {"start": v(18.65, -378.76) * mm, "end": v(18.7, -378.67) * mm});
            skLineSegment(sketch, "E1713", {"start": v(18.7, -378.67) * mm, "end": v(18.74, -378.57) * mm});
            skLineSegment(sketch, "E1714", {"start": v(18.74, -378.57) * mm, "end": v(18.78, -378.47) * mm});
            skLineSegment(sketch, "E1715", {"start": v(18.78, -378.47) * mm, "end": v(18.81, -378.36) * mm});
            skLineSegment(sketch, "E1716", {"start": v(18.81, -378.36) * mm, "end": v(18.84, -378.26) * mm});
            skLineSegment(sketch, "E1717", {"start": v(18.84, -378.26) * mm, "end": v(18.86, -378.15) * mm});
            skLineSegment(sketch, "E1718", {"start": v(18.86, -378.15) * mm, "end": v(18.87, -378.04) * mm});
            skLineSegment(sketch, "E1719", {"start": v(18.87, -378.04) * mm, "end": v(18.87, -377.93) * mm});
            skLineSegment(sketch, "E1720", {"start": v(8.77, -377.93) * mm, "end": v(8.77, -377.74) * mm});
            skLineSegment(sketch, "E1721", {"start": v(8.77, -377.74) * mm, "end": v(8.75, -377.54) * mm});
            skLineSegment(sketch, "E1722", {"start": v(8.75, -377.54) * mm, "end": v(8.71, -377.34) * mm});
            skLineSegment(sketch, "E1723", {"start": v(8.71, -377.34) * mm, "end": v(8.67, -377.15) * mm});
            skLineSegment(sketch, "E1724", {"start": v(8.67, -377.15) * mm, "end": v(8.61, -376.96) * mm});
            skLineSegment(sketch, "E1725", {"start": v(8.61, -376.96) * mm, "end": v(8.54, -376.77) * mm});
            skLineSegment(sketch, "E1726", {"start": v(8.54, -376.77) * mm, "end": v(8.46, -376.6) * mm});
            skLineSegment(sketch, "E1727", {"start": v(8.46, -376.6) * mm, "end": v(8.37, -376.42) * mm});
            skLineSegment(sketch, "E1728", {"start": v(8.37, -376.42) * mm, "end": v(8.26, -376.25) * mm});
            skLineSegment(sketch, "E1729", {"start": v(8.26, -376.25) * mm, "end": v(8.15, -376.09) * mm});
            skLineSegment(sketch, "E1730", {"start": v(8.15, -376.09) * mm, "end": v(8.02, -375.93) * mm});
            skLineSegment(sketch, "E1731", {"start": v(8.02, -375.93) * mm, "end": v(7.88, -375.79) * mm});
            skLineSegment(sketch, "E1732", {"start": v(7.88, -375.79) * mm, "end": v(7.74, -375.65) * mm});
            skLineSegment(sketch, "E1733", {"start": v(7.74, -375.65) * mm, "end": v(7.59, -375.53) * mm});
            skLineSegment(sketch, "E1734", {"start": v(7.59, -375.53) * mm, "end": v(7.42, -375.41) * mm});
            skLineSegment(sketch, "E1735", {"start": v(7.42, -375.41) * mm, "end": v(7.26, -375.3) * mm});
            skLineSegment(sketch, "E1736", {"start": v(7.26, -375.3) * mm, "end": v(7.08, -375.21) * mm});
            skLineSegment(sketch, "E1737", {"start": v(7.08, -375.21) * mm, "end": v(6.9, -375.13) * mm});
            skLineSegment(sketch, "E1738", {"start": v(6.9, -375.13) * mm, "end": v(6.71, -375.06) * mm});
            skLineSegment(sketch, "E1739", {"start": v(6.71, -375.06) * mm, "end": v(6.52, -375) * mm});
            skLineSegment(sketch, "E1740", {"start": v(6.52, -375) * mm, "end": v(6.33, -374.96) * mm});
            skLineSegment(sketch, "E1741", {"start": v(6.33, -374.96) * mm, "end": v(6.13, -374.93) * mm});
            skLineSegment(sketch, "E1742", {"start": v(6.13, -374.93) * mm, "end": v(5.94, -374.9) * mm});
            skLineSegment(sketch, "E1743", {"start": v(5.94, -374.9) * mm, "end": v(5.74, -374.9) * mm});
            skLineSegment(sketch, "E1744", {"start": v(5.74, -374.9) * mm, "end": v(5.54, -374.9) * mm});
            skLineSegment(sketch, "E1745", {"start": v(5.54, -374.9) * mm, "end": v(5.34, -374.93) * mm});
            skLineSegment(sketch, "E1746", {"start": v(5.34, -374.93) * mm, "end": v(5.15, -374.96) * mm});
            skLineSegment(sketch, "E1747", {"start": v(5.15, -374.96) * mm, "end": v(4.95, -375) * mm});
            skLineSegment(sketch, "E1748", {"start": v(4.95, -375) * mm, "end": v(4.76, -375.06) * mm});
            skLineSegment(sketch, "E1749", {"start": v(4.76, -375.06) * mm, "end": v(4.58, -375.13) * mm});
            skLineSegment(sketch, "E1750", {"start": v(4.58, -375.13) * mm, "end": v(4.4, -375.21) * mm});
            skLineSegment(sketch, "E1751", {"start": v(4.4, -375.21) * mm, "end": v(4.22, -375.3) * mm});
            skLineSegment(sketch, "E1752", {"start": v(4.22, -375.3) * mm, "end": v(4.05, -375.41) * mm});
            skLineSegment(sketch, "E1753", {"start": v(4.05, -375.41) * mm, "end": v(3.9, -375.53) * mm});
            skLineSegment(sketch, "E1754", {"start": v(3.9, -375.53) * mm, "end": v(3.74, -375.65) * mm});
            skLineSegment(sketch, "E1755", {"start": v(3.74, -375.65) * mm, "end": v(3.6, -375.79) * mm});
            skLineSegment(sketch, "E1756", {"start": v(3.6, -375.79) * mm, "end": v(3.46, -375.93) * mm});
            skLineSegment(sketch, "E1757", {"start": v(3.46, -375.93) * mm, "end": v(3.33, -376.09) * mm});
            skLineSegment(sketch, "E1758", {"start": v(3.33, -376.09) * mm, "end": v(3.22, -376.25) * mm});
            skLineSegment(sketch, "E1759", {"start": v(3.22, -376.25) * mm, "end": v(3.11, -376.42) * mm});
            skLineSegment(sketch, "E1760", {"start": v(3.11, -376.42) * mm, "end": v(3.02, -376.6) * mm});
            skLineSegment(sketch, "E1761", {"start": v(3.02, -376.6) * mm, "end": v(2.93, -376.77) * mm});
            skLineSegment(sketch, "E1762", {"start": v(2.93, -376.77) * mm, "end": v(2.86, -376.96) * mm});
            skLineSegment(sketch, "E1763", {"start": v(2.86, -376.96) * mm, "end": v(2.8, -377.15) * mm});
            skLineSegment(sketch, "E1764", {"start": v(2.8, -377.15) * mm, "end": v(2.76, -377.34) * mm});
            skLineSegment(sketch, "E1765", {"start": v(2.76, -377.34) * mm, "end": v(2.73, -377.54) * mm});
            skLineSegment(sketch, "E1766", {"start": v(2.73, -377.54) * mm, "end": v(2.71, -377.74) * mm});
            skLineSegment(sketch, "E1767", {"start": v(2.71, -377.74) * mm, "end": v(2.7, -377.93) * mm});
            skLineSegment(sketch, "E1768", {"start": v(2.7, -377.93) * mm, "end": v(2.71, -378.13) * mm});
            skLineSegment(sketch, "E1769", {"start": v(2.71, -378.13) * mm, "end": v(2.73, -378.33) * mm});
            skLineSegment(sketch, "E1770", {"start": v(2.73, -378.33) * mm, "end": v(2.76, -378.53) * mm});
            skLineSegment(sketch, "E1771", {"start": v(2.76, -378.53) * mm, "end": v(2.8, -378.72) * mm});
            skLineSegment(sketch, "E1772", {"start": v(2.8, -378.72) * mm, "end": v(2.86, -378.9) * mm});
            skLineSegment(sketch, "E1773", {"start": v(2.86, -378.9) * mm, "end": v(2.93, -379.1) * mm});
            skLineSegment(sketch, "E1774", {"start": v(2.93, -379.1) * mm, "end": v(3.02, -379.28) * mm});
            skLineSegment(sketch, "E1775", {"start": v(3.02, -379.28) * mm, "end": v(3.11, -379.45) * mm});
            skLineSegment(sketch, "E1776", {"start": v(3.11, -379.45) * mm, "end": v(3.22, -379.62) * mm});
            skLineSegment(sketch, "E1777", {"start": v(3.22, -379.62) * mm, "end": v(3.33, -379.78) * mm});
            skLineSegment(sketch, "E1778", {"start": v(3.33, -379.78) * mm, "end": v(3.46, -379.93) * mm});
            skLineSegment(sketch, "E1779", {"start": v(3.46, -379.93) * mm, "end": v(3.6, -380.08) * mm});
            skLineSegment(sketch, "E1780", {"start": v(3.6, -380.08) * mm, "end": v(3.74, -380.22) * mm});
            skLineSegment(sketch, "E1781", {"start": v(3.74, -380.22) * mm, "end": v(3.9, -380.34) * mm});
            skLineSegment(sketch, "E1782", {"start": v(3.9, -380.34) * mm, "end": v(4.05, -380.46) * mm});
            skLineSegment(sketch, "E1783", {"start": v(4.05, -380.46) * mm, "end": v(4.22, -380.56) * mm});
            skLineSegment(sketch, "E1784", {"start": v(4.22, -380.56) * mm, "end": v(4.4, -380.66) * mm});
            skLineSegment(sketch, "E1785", {"start": v(4.4, -380.66) * mm, "end": v(4.58, -380.74) * mm});
            skLineSegment(sketch, "E1786", {"start": v(4.58, -380.74) * mm, "end": v(4.76, -380.8) * mm});
            skLineSegment(sketch, "E1787", {"start": v(4.76, -380.8) * mm, "end": v(4.95, -380.87) * mm});
            skLineSegment(sketch, "E1788", {"start": v(4.95, -380.87) * mm, "end": v(5.15, -380.91) * mm});
            skLineSegment(sketch, "E1789", {"start": v(5.15, -380.91) * mm, "end": v(5.34, -380.94) * mm});
            skLineSegment(sketch, "E1790", {"start": v(5.34, -380.94) * mm, "end": v(5.54, -380.96) * mm});
            skLineSegment(sketch, "E1791", {"start": v(5.54, -380.96) * mm, "end": v(5.74, -380.97) * mm});
            skLineSegment(sketch, "E1792", {"start": v(5.74, -380.97) * mm, "end": v(5.94, -380.96) * mm});
            skLineSegment(sketch, "E1793", {"start": v(5.94, -380.96) * mm, "end": v(6.13, -380.94) * mm});
            skLineSegment(sketch, "E1794", {"start": v(6.13, -380.94) * mm, "end": v(6.33, -380.91) * mm});
            skLineSegment(sketch, "E1795", {"start": v(6.33, -380.91) * mm, "end": v(6.52, -380.87) * mm});
            skLineSegment(sketch, "E1796", {"start": v(6.52, -380.87) * mm, "end": v(6.71, -380.8) * mm});
            skLineSegment(sketch, "E1797", {"start": v(6.71, -380.8) * mm, "end": v(6.9, -380.74) * mm});
            skLineSegment(sketch, "E1798", {"start": v(6.9, -380.74) * mm, "end": v(7.08, -380.66) * mm});
            skLineSegment(sketch, "E1799", {"start": v(7.08, -380.66) * mm, "end": v(7.26, -380.56) * mm});
            skLineSegment(sketch, "E1800", {"start": v(7.26, -380.56) * mm, "end": v(7.42, -380.46) * mm});
            skLineSegment(sketch, "E1801", {"start": v(7.42, -380.46) * mm, "end": v(7.59, -380.34) * mm});
            skLineSegment(sketch, "E1802", {"start": v(7.59, -380.34) * mm, "end": v(7.74, -380.22) * mm});
            skLineSegment(sketch, "E1803", {"start": v(7.74, -380.22) * mm, "end": v(7.88, -380.08) * mm});
            skLineSegment(sketch, "E1804", {"start": v(7.88, -380.08) * mm, "end": v(8.02, -379.93) * mm});
            skLineSegment(sketch, "E1805", {"start": v(8.02, -379.93) * mm, "end": v(8.15, -379.78) * mm});
            skLineSegment(sketch, "E1806", {"start": v(8.15, -379.78) * mm, "end": v(8.26, -379.62) * mm});
            skLineSegment(sketch, "E1807", {"start": v(8.26, -379.62) * mm, "end": v(8.37, -379.45) * mm});
            skLineSegment(sketch, "E1808", {"start": v(8.37, -379.45) * mm, "end": v(8.46, -379.28) * mm});
            skLineSegment(sketch, "E1809", {"start": v(8.46, -379.28) * mm, "end": v(8.54, -379.1) * mm});
            skLineSegment(sketch, "E1810", {"start": v(8.54, -379.1) * mm, "end": v(8.61, -378.9) * mm});
            skLineSegment(sketch, "E1811", {"start": v(8.61, -378.9) * mm, "end": v(8.67, -378.72) * mm});
            skLineSegment(sketch, "E1812", {"start": v(8.67, -378.72) * mm, "end": v(8.71, -378.53) * mm});
            skLineSegment(sketch, "E1813", {"start": v(8.71, -378.53) * mm, "end": v(8.75, -378.33) * mm});
            skLineSegment(sketch, "E1814", {"start": v(8.75, -378.33) * mm, "end": v(8.77, -378.13) * mm});
            skLineSegment(sketch, "E1815", {"start": v(8.77, -378.13) * mm, "end": v(8.77, -377.93) * mm});
            skLineSegment(sketch, "E1816", {"start": v(7.4, -377.93) * mm, "end": v(7.4, -377.83) * mm});
            skLineSegment(sketch, "E1817", {"start": v(7.4, -377.83) * mm, "end": v(7.38, -377.72) * mm});
            skLineSegment(sketch, "E1818", {"start": v(7.38, -377.72) * mm, "end": v(7.36, -377.61) * mm});
            skLineSegment(sketch, "E1819", {"start": v(7.36, -377.61) * mm, "end": v(7.34, -377.5) * mm});
            skLineSegment(sketch, "E1820", {"start": v(7.34, -377.5) * mm, "end": v(7.3, -377.4) * mm});
            skLineSegment(sketch, "E1821", {"start": v(7.3, -377.4) * mm, "end": v(7.27, -377.3) * mm});
            skLineSegment(sketch, "E1822", {"start": v(7.27, -377.3) * mm, "end": v(7.22, -377.2) * mm});
            skLineSegment(sketch, "E1823", {"start": v(7.22, -377.2) * mm, "end": v(7.17, -377.1) * mm});
            skLineSegment(sketch, "E1824", {"start": v(7.17, -377.1) * mm, "end": v(7.11, -377.01) * mm});
            skLineSegment(sketch, "E1825", {"start": v(7.11, -377.01) * mm, "end": v(7.05, -376.93) * mm});
            skLineSegment(sketch, "E1826", {"start": v(7.05, -376.93) * mm, "end": v(6.98, -376.84) * mm});
            skLineSegment(sketch, "E1827", {"start": v(6.98, -376.84) * mm, "end": v(6.9, -376.76) * mm});
            skLineSegment(sketch, "E1828", {"start": v(6.9, -376.76) * mm, "end": v(6.83, -376.69) * mm});
            skLineSegment(sketch, "E1829", {"start": v(6.83, -376.69) * mm, "end": v(6.75, -376.62) * mm});
            skLineSegment(sketch, "E1830", {"start": v(6.75, -376.62) * mm, "end": v(6.66, -376.56) * mm});
            skLineSegment(sketch, "E1831", {"start": v(6.66, -376.56) * mm, "end": v(6.57, -376.5) * mm});
            skLineSegment(sketch, "E1832", {"start": v(6.57, -376.5) * mm, "end": v(6.47, -376.45) * mm});
            skLineSegment(sketch, "E1833", {"start": v(6.47, -376.45) * mm, "end": v(6.37, -376.4) * mm});
            skLineSegment(sketch, "E1834", {"start": v(6.37, -376.4) * mm, "end": v(6.27, -376.37) * mm});
            skLineSegment(sketch, "E1835", {"start": v(6.27, -376.37) * mm, "end": v(6.17, -376.33) * mm});
            skLineSegment(sketch, "E1836", {"start": v(6.17, -376.33) * mm, "end": v(6.06, -376.31) * mm});
            skLineSegment(sketch, "E1837", {"start": v(6.06, -376.31) * mm, "end": v(5.95, -376.3) * mm});
            skLineSegment(sketch, "E1838", {"start": v(5.95, -376.3) * mm, "end": v(5.85, -376.28) * mm});
            skLineSegment(sketch, "E1839", {"start": v(5.85, -376.28) * mm, "end": v(5.74, -376.28) * mm});
            skLineSegment(sketch, "E1840", {"start": v(5.74, -376.28) * mm, "end": v(5.63, -376.28) * mm});
            skLineSegment(sketch, "E1841", {"start": v(5.63, -376.28) * mm, "end": v(5.52, -376.3) * mm});
            skLineSegment(sketch, "E1842", {"start": v(5.52, -376.3) * mm, "end": v(5.42, -376.31) * mm});
            skLineSegment(sketch, "E1843", {"start": v(5.42, -376.31) * mm, "end": v(5.3, -376.33) * mm});
            skLineSegment(sketch, "E1844", {"start": v(5.3, -376.33) * mm, "end": v(5.2, -376.37) * mm});
            skLineSegment(sketch, "E1845", {"start": v(5.2, -376.37) * mm, "end": v(5.1, -376.4) * mm});
            skLineSegment(sketch, "E1846", {"start": v(5.1, -376.4) * mm, "end": v(5, -376.45) * mm});
            skLineSegment(sketch, "E1847", {"start": v(5, -376.45) * mm, "end": v(4.91, -376.5) * mm});
            skLineSegment(sketch, "E1848", {"start": v(4.91, -376.5) * mm, "end": v(4.82, -376.56) * mm});
            skLineSegment(sketch, "E1849", {"start": v(4.82, -376.56) * mm, "end": v(4.73, -376.62) * mm});
            skLineSegment(sketch, "E1850", {"start": v(4.73, -376.62) * mm, "end": v(4.65, -376.69) * mm});
            skLineSegment(sketch, "E1851", {"start": v(4.65, -376.69) * mm, "end": v(4.57, -376.76) * mm});
            skLineSegment(sketch, "E1852", {"start": v(4.57, -376.76) * mm, "end": v(4.5, -376.84) * mm});
            skLineSegment(sketch, "E1853", {"start": v(4.5, -376.84) * mm, "end": v(4.43, -376.93) * mm});
            skLineSegment(sketch, "E1854", {"start": v(4.43, -376.93) * mm, "end": v(4.36, -377.01) * mm});
            skLineSegment(sketch, "E1855", {"start": v(4.36, -377.01) * mm, "end": v(4.3, -377.1) * mm});
            skLineSegment(sketch, "E1856", {"start": v(4.3, -377.1) * mm, "end": v(4.25, -377.2) * mm});
            skLineSegment(sketch, "E1857", {"start": v(4.25, -377.2) * mm, "end": v(4.2, -377.3) * mm});
            skLineSegment(sketch, "E1858", {"start": v(4.2, -377.3) * mm, "end": v(4.17, -377.4) * mm});
            skLineSegment(sketch, "E1859", {"start": v(4.17, -377.4) * mm, "end": v(4.14, -377.5) * mm});
            skLineSegment(sketch, "E1860", {"start": v(4.14, -377.5) * mm, "end": v(4.11, -377.61) * mm});
            skLineSegment(sketch, "E1861", {"start": v(4.11, -377.61) * mm, "end": v(4.1, -377.72) * mm});
            skLineSegment(sketch, "E1862", {"start": v(4.1, -377.72) * mm, "end": v(4.09, -377.83) * mm});
            skLineSegment(sketch, "E1863", {"start": v(4.09, -377.83) * mm, "end": v(4.08, -377.93) * mm});
            skLineSegment(sketch, "E1864", {"start": v(4.08, -377.93) * mm, "end": v(4.09, -378.04) * mm});
            skLineSegment(sketch, "E1865", {"start": v(4.09, -378.04) * mm, "end": v(4.1, -378.15) * mm});
            skLineSegment(sketch, "E1866", {"start": v(4.1, -378.15) * mm, "end": v(4.11, -378.26) * mm});
            skLineSegment(sketch, "E1867", {"start": v(4.11, -378.26) * mm, "end": v(4.14, -378.36) * mm});
            skLineSegment(sketch, "E1868", {"start": v(4.14, -378.36) * mm, "end": v(4.17, -378.47) * mm});
            skLineSegment(sketch, "E1869", {"start": v(4.17, -378.47) * mm, "end": v(4.2, -378.57) * mm});
            skLineSegment(sketch, "E1870", {"start": v(4.2, -378.57) * mm, "end": v(4.25, -378.67) * mm});
            skLineSegment(sketch, "E1871", {"start": v(4.25, -378.67) * mm, "end": v(4.3, -378.76) * mm});
            skLineSegment(sketch, "E1872", {"start": v(4.3, -378.76) * mm, "end": v(4.36, -378.85) * mm});
            skLineSegment(sketch, "E1873", {"start": v(4.36, -378.85) * mm, "end": v(4.43, -378.94) * mm});
            skLineSegment(sketch, "E1874", {"start": v(4.43, -378.94) * mm, "end": v(4.5, -379.03) * mm});
            skLineSegment(sketch, "E1875", {"start": v(4.5, -379.03) * mm, "end": v(4.57, -379.1) * mm});
            skLineSegment(sketch, "E1876", {"start": v(4.57, -379.1) * mm, "end": v(4.65, -379.18) * mm});
            skLineSegment(sketch, "E1877", {"start": v(4.65, -379.18) * mm, "end": v(4.73, -379.25) * mm});
            skLineSegment(sketch, "E1878", {"start": v(4.73, -379.25) * mm, "end": v(4.82, -379.31) * mm});
            skLineSegment(sketch, "E1879", {"start": v(4.82, -379.31) * mm, "end": v(4.91, -379.37) * mm});
            skLineSegment(sketch, "E1880", {"start": v(4.91, -379.37) * mm, "end": v(5, -379.42) * mm});
            skLineSegment(sketch, "E1881", {"start": v(5, -379.42) * mm, "end": v(5.1, -379.46) * mm});
            skLineSegment(sketch, "E1882", {"start": v(5.1, -379.46) * mm, "end": v(5.2, -379.5) * mm});
            skLineSegment(sketch, "E1883", {"start": v(5.2, -379.5) * mm, "end": v(5.3, -379.53) * mm});
            skLineSegment(sketch, "E1884", {"start": v(5.3, -379.53) * mm, "end": v(5.42, -379.56) * mm});
            skLineSegment(sketch, "E1885", {"start": v(5.42, -379.56) * mm, "end": v(5.52, -379.58) * mm});
            skLineSegment(sketch, "E1886", {"start": v(5.52, -379.58) * mm, "end": v(5.63, -379.59) * mm});
            skLineSegment(sketch, "E1887", {"start": v(5.63, -379.59) * mm, "end": v(5.74, -379.59) * mm});
            skLineSegment(sketch, "E1888", {"start": v(5.74, -379.59) * mm, "end": v(5.85, -379.59) * mm});
            skLineSegment(sketch, "E1889", {"start": v(5.85, -379.59) * mm, "end": v(5.95, -379.58) * mm});
            skLineSegment(sketch, "E1890", {"start": v(5.95, -379.58) * mm, "end": v(6.06, -379.56) * mm});
            skLineSegment(sketch, "E1891", {"start": v(6.06, -379.56) * mm, "end": v(6.17, -379.53) * mm});
            skLineSegment(sketch, "E1892", {"start": v(6.17, -379.53) * mm, "end": v(6.27, -379.5) * mm});
            skLineSegment(sketch, "E1893", {"start": v(6.27, -379.5) * mm, "end": v(6.37, -379.46) * mm});
            skLineSegment(sketch, "E1894", {"start": v(6.37, -379.46) * mm, "end": v(6.47, -379.42) * mm});
            skLineSegment(sketch, "E1895", {"start": v(6.47, -379.42) * mm, "end": v(6.57, -379.37) * mm});
            skLineSegment(sketch, "E1896", {"start": v(6.57, -379.37) * mm, "end": v(6.66, -379.31) * mm});
            skLineSegment(sketch, "E1897", {"start": v(6.66, -379.31) * mm, "end": v(6.75, -379.25) * mm});
            skLineSegment(sketch, "E1898", {"start": v(6.75, -379.25) * mm, "end": v(6.83, -379.18) * mm});
            skLineSegment(sketch, "E1899", {"start": v(6.83, -379.18) * mm, "end": v(6.9, -379.1) * mm});
            skLineSegment(sketch, "E1900", {"start": v(6.9, -379.1) * mm, "end": v(6.98, -379.03) * mm});
            skLineSegment(sketch, "E1901", {"start": v(6.98, -379.03) * mm, "end": v(7.05, -378.94) * mm});
            skLineSegment(sketch, "E1902", {"start": v(7.05, -378.94) * mm, "end": v(7.11, -378.85) * mm});
            skLineSegment(sketch, "E1903", {"start": v(7.11, -378.85) * mm, "end": v(7.17, -378.76) * mm});
            skLineSegment(sketch, "E1904", {"start": v(7.17, -378.76) * mm, "end": v(7.22, -378.67) * mm});
            skLineSegment(sketch, "E1905", {"start": v(7.22, -378.67) * mm, "end": v(7.27, -378.57) * mm});
            skLineSegment(sketch, "E1906", {"start": v(7.27, -378.57) * mm, "end": v(7.3, -378.47) * mm});
            skLineSegment(sketch, "E1907", {"start": v(7.3, -378.47) * mm, "end": v(7.34, -378.36) * mm});
            skLineSegment(sketch, "E1908", {"start": v(7.34, -378.36) * mm, "end": v(7.36, -378.26) * mm});
            skLineSegment(sketch, "E1909", {"start": v(7.36, -378.26) * mm, "end": v(7.38, -378.15) * mm});
            skLineSegment(sketch, "E1910", {"start": v(7.38, -378.15) * mm, "end": v(7.4, -378.04) * mm});
            skLineSegment(sketch, "E1911", {"start": v(7.4, -378.04) * mm, "end": v(7.4, -377.93) * mm});
            skLineSegment(sketch, "E1912", {"start": v(-2.7, -377.93) * mm, "end": v(-2.71, -377.74) * mm});
            skLineSegment(sketch, "E1913", {"start": v(-2.71, -377.74) * mm, "end": v(-2.73, -377.54) * mm});
            skLineSegment(sketch, "E1914", {"start": v(-2.73, -377.54) * mm, "end": v(-2.76, -377.34) * mm});
            skLineSegment(sketch, "E1915", {"start": v(-2.76, -377.34) * mm, "end": v(-2.8, -377.15) * mm});
            skLineSegment(sketch, "E1916", {"start": v(-2.8, -377.15) * mm, "end": v(-2.86, -376.96) * mm});
            skLineSegment(sketch, "E1917", {"start": v(-2.86, -376.96) * mm, "end": v(-2.93, -376.77) * mm});
            skLineSegment(sketch, "E1918", {"start": v(-2.93, -376.77) * mm, "end": v(-3.02, -376.6) * mm});
            skLineSegment(sketch, "E1919", {"start": v(-3.02, -376.6) * mm, "end": v(-3.11, -376.42) * mm});
            skLineSegment(sketch, "E1920", {"start": v(-3.11, -376.42) * mm, "end": v(-3.22, -376.25) * mm});
            skLineSegment(sketch, "E1921", {"start": v(-3.22, -376.25) * mm, "end": v(-3.33, -376.09) * mm});
            skLineSegment(sketch, "E1922", {"start": v(-3.33, -376.09) * mm, "end": v(-3.46, -375.93) * mm});
            skLineSegment(sketch, "E1923", {"start": v(-3.46, -375.93) * mm, "end": v(-3.6, -375.79) * mm});
            skLineSegment(sketch, "E1924", {"start": v(-3.6, -375.79) * mm, "end": v(-3.74, -375.65) * mm});
            skLineSegment(sketch, "E1925", {"start": v(-3.74, -375.65) * mm, "end": v(-3.9, -375.53) * mm});
            skLineSegment(sketch, "E1926", {"start": v(-3.9, -375.53) * mm, "end": v(-4.05, -375.41) * mm});
            skLineSegment(sketch, "E1927", {"start": v(-4.05, -375.41) * mm, "end": v(-4.22, -375.3) * mm});
            skLineSegment(sketch, "E1928", {"start": v(-4.22, -375.3) * mm, "end": v(-4.4, -375.21) * mm});
            skLineSegment(sketch, "E1929", {"start": v(-4.4, -375.21) * mm, "end": v(-4.58, -375.13) * mm});
            skLineSegment(sketch, "E1930", {"start": v(-4.58, -375.13) * mm, "end": v(-4.76, -375.06) * mm});
            skLineSegment(sketch, "E1931", {"start": v(-4.76, -375.06) * mm, "end": v(-4.95, -375) * mm});
            skLineSegment(sketch, "E1932", {"start": v(-4.95, -375) * mm, "end": v(-5.15, -374.96) * mm});
            skLineSegment(sketch, "E1933", {"start": v(-5.15, -374.96) * mm, "end": v(-5.34, -374.93) * mm});
            skLineSegment(sketch, "E1934", {"start": v(-5.34, -374.93) * mm, "end": v(-5.54, -374.9) * mm});
            skLineSegment(sketch, "E1935", {"start": v(-5.54, -374.9) * mm, "end": v(-5.74, -374.9) * mm});
            skLineSegment(sketch, "E1936", {"start": v(-5.74, -374.9) * mm, "end": v(-5.94, -374.9) * mm});
            skLineSegment(sketch, "E1937", {"start": v(-5.94, -374.9) * mm, "end": v(-6.13, -374.93) * mm});
            skLineSegment(sketch, "E1938", {"start": v(-6.13, -374.93) * mm, "end": v(-6.33, -374.96) * mm});
            skLineSegment(sketch, "E1939", {"start": v(-6.33, -374.96) * mm, "end": v(-6.52, -375) * mm});
            skLineSegment(sketch, "E1940", {"start": v(-6.52, -375) * mm, "end": v(-6.71, -375.06) * mm});
            skLineSegment(sketch, "E1941", {"start": v(-6.71, -375.06) * mm, "end": v(-6.9, -375.13) * mm});
            skLineSegment(sketch, "E1942", {"start": v(-6.9, -375.13) * mm, "end": v(-7.08, -375.21) * mm});
            skLineSegment(sketch, "E1943", {"start": v(-7.08, -375.21) * mm, "end": v(-7.26, -375.3) * mm});
            skLineSegment(sketch, "E1944", {"start": v(-7.26, -375.3) * mm, "end": v(-7.42, -375.41) * mm});
            skLineSegment(sketch, "E1945", {"start": v(-7.42, -375.41) * mm, "end": v(-7.59, -375.53) * mm});
            skLineSegment(sketch, "E1946", {"start": v(-7.59, -375.53) * mm, "end": v(-7.74, -375.65) * mm});
            skLineSegment(sketch, "E1947", {"start": v(-7.74, -375.65) * mm, "end": v(-7.88, -375.79) * mm});
            skLineSegment(sketch, "E1948", {"start": v(-7.88, -375.79) * mm, "end": v(-8.02, -375.93) * mm});
            skLineSegment(sketch, "E1949", {"start": v(-8.02, -375.93) * mm, "end": v(-8.15, -376.09) * mm});
            skLineSegment(sketch, "E1950", {"start": v(-8.15, -376.09) * mm, "end": v(-8.26, -376.25) * mm});
            skLineSegment(sketch, "E1951", {"start": v(-8.26, -376.25) * mm, "end": v(-8.37, -376.42) * mm});
            skLineSegment(sketch, "E1952", {"start": v(-8.37, -376.42) * mm, "end": v(-8.46, -376.6) * mm});
            skLineSegment(sketch, "E1953", {"start": v(-8.46, -376.6) * mm, "end": v(-8.54, -376.77) * mm});
            skLineSegment(sketch, "E1954", {"start": v(-8.54, -376.77) * mm, "end": v(-8.61, -376.96) * mm});
            skLineSegment(sketch, "E1955", {"start": v(-8.61, -376.96) * mm, "end": v(-8.67, -377.15) * mm});
            skLineSegment(sketch, "E1956", {"start": v(-8.67, -377.15) * mm, "end": v(-8.71, -377.34) * mm});
            skLineSegment(sketch, "E1957", {"start": v(-8.71, -377.34) * mm, "end": v(-8.75, -377.54) * mm});
            skLineSegment(sketch, "E1958", {"start": v(-8.75, -377.54) * mm, "end": v(-8.77, -377.74) * mm});
            skLineSegment(sketch, "E1959", {"start": v(-8.77, -377.74) * mm, "end": v(-8.77, -377.93) * mm});
            skLineSegment(sketch, "E1960", {"start": v(-8.77, -377.93) * mm, "end": v(-8.77, -378.13) * mm});
            skLineSegment(sketch, "E1961", {"start": v(-8.77, -378.13) * mm, "end": v(-8.75, -378.33) * mm});
            skLineSegment(sketch, "E1962", {"start": v(-8.75, -378.33) * mm, "end": v(-8.71, -378.53) * mm});
            skLineSegment(sketch, "E1963", {"start": v(-8.71, -378.53) * mm, "end": v(-8.67, -378.72) * mm});
            skLineSegment(sketch, "E1964", {"start": v(-8.67, -378.72) * mm, "end": v(-8.61, -378.9) * mm});
            skLineSegment(sketch, "E1965", {"start": v(-8.61, -378.9) * mm, "end": v(-8.54, -379.1) * mm});
            skLineSegment(sketch, "E1966", {"start": v(-8.54, -379.1) * mm, "end": v(-8.46, -379.28) * mm});
            skLineSegment(sketch, "E1967", {"start": v(-8.46, -379.28) * mm, "end": v(-8.37, -379.45) * mm});
            skLineSegment(sketch, "E1968", {"start": v(-8.37, -379.45) * mm, "end": v(-8.26, -379.62) * mm});
            skLineSegment(sketch, "E1969", {"start": v(-8.26, -379.62) * mm, "end": v(-8.15, -379.78) * mm});
            skLineSegment(sketch, "E1970", {"start": v(-8.15, -379.78) * mm, "end": v(-8.02, -379.93) * mm});
            skLineSegment(sketch, "E1971", {"start": v(-8.02, -379.93) * mm, "end": v(-7.88, -380.08) * mm});
            skLineSegment(sketch, "E1972", {"start": v(-7.88, -380.08) * mm, "end": v(-7.74, -380.22) * mm});
            skLineSegment(sketch, "E1973", {"start": v(-7.74, -380.22) * mm, "end": v(-7.59, -380.34) * mm});
            skLineSegment(sketch, "E1974", {"start": v(-7.59, -380.34) * mm, "end": v(-7.42, -380.46) * mm});
            skLineSegment(sketch, "E1975", {"start": v(-7.42, -380.46) * mm, "end": v(-7.26, -380.56) * mm});
            skLineSegment(sketch, "E1976", {"start": v(-7.26, -380.56) * mm, "end": v(-7.08, -380.66) * mm});
            skLineSegment(sketch, "E1977", {"start": v(-7.08, -380.66) * mm, "end": v(-6.9, -380.74) * mm});
            skLineSegment(sketch, "E1978", {"start": v(-6.9, -380.74) * mm, "end": v(-6.71, -380.8) * mm});
            skLineSegment(sketch, "E1979", {"start": v(-6.71, -380.8) * mm, "end": v(-6.52, -380.87) * mm});
            skLineSegment(sketch, "E1980", {"start": v(-6.52, -380.87) * mm, "end": v(-6.33, -380.91) * mm});
            skLineSegment(sketch, "E1981", {"start": v(-6.33, -380.91) * mm, "end": v(-6.13, -380.94) * mm});
            skLineSegment(sketch, "E1982", {"start": v(-6.13, -380.94) * mm, "end": v(-5.94, -380.96) * mm});
            skLineSegment(sketch, "E1983", {"start": v(-5.94, -380.96) * mm, "end": v(-5.74, -380.97) * mm});
            skLineSegment(sketch, "E1984", {"start": v(-5.74, -380.97) * mm, "end": v(-5.54, -380.96) * mm});
            skLineSegment(sketch, "E1985", {"start": v(-5.54, -380.96) * mm, "end": v(-5.34, -380.94) * mm});
            skLineSegment(sketch, "E1986", {"start": v(-5.34, -380.94) * mm, "end": v(-5.15, -380.91) * mm});
            skLineSegment(sketch, "E1987", {"start": v(-5.15, -380.91) * mm, "end": v(-4.95, -380.87) * mm});
            skLineSegment(sketch, "E1988", {"start": v(-4.95, -380.87) * mm, "end": v(-4.76, -380.8) * mm});
            skLineSegment(sketch, "E1989", {"start": v(-4.76, -380.8) * mm, "end": v(-4.58, -380.74) * mm});
            skLineSegment(sketch, "E1990", {"start": v(-4.58, -380.74) * mm, "end": v(-4.4, -380.66) * mm});
            skLineSegment(sketch, "E1991", {"start": v(-4.4, -380.66) * mm, "end": v(-4.22, -380.56) * mm});
            skLineSegment(sketch, "E1992", {"start": v(-4.22, -380.56) * mm, "end": v(-4.05, -380.46) * mm});
            skLineSegment(sketch, "E1993", {"start": v(-4.05, -380.46) * mm, "end": v(-3.9, -380.34) * mm});
            skLineSegment(sketch, "E1994", {"start": v(-3.9, -380.34) * mm, "end": v(-3.74, -380.22) * mm});
            skLineSegment(sketch, "E1995", {"start": v(-3.74, -380.22) * mm, "end": v(-3.6, -380.08) * mm});
            skLineSegment(sketch, "E1996", {"start": v(-3.6, -380.08) * mm, "end": v(-3.46, -379.93) * mm});
            skLineSegment(sketch, "E1997", {"start": v(-3.46, -379.93) * mm, "end": v(-3.33, -379.78) * mm});
            skLineSegment(sketch, "E1998", {"start": v(-3.33, -379.78) * mm, "end": v(-3.22, -379.62) * mm});
            skLineSegment(sketch, "E1999", {"start": v(-3.22, -379.62) * mm, "end": v(-3.11, -379.45) * mm});
            skLineSegment(sketch, "E2000", {"start": v(-3.11, -379.45) * mm, "end": v(-3.02, -379.28) * mm});
            skLineSegment(sketch, "E2001", {"start": v(-3.02, -379.28) * mm, "end": v(-2.93, -379.1) * mm});
            skLineSegment(sketch, "E2002", {"start": v(-2.93, -379.1) * mm, "end": v(-2.86, -378.9) * mm});
            skLineSegment(sketch, "E2003", {"start": v(-2.86, -378.9) * mm, "end": v(-2.8, -378.72) * mm});
            skLineSegment(sketch, "E2004", {"start": v(-2.8, -378.72) * mm, "end": v(-2.76, -378.53) * mm});
            skLineSegment(sketch, "E2005", {"start": v(-2.76, -378.53) * mm, "end": v(-2.73, -378.33) * mm});
            skLineSegment(sketch, "E2006", {"start": v(-2.73, -378.33) * mm, "end": v(-2.71, -378.13) * mm});
            skLineSegment(sketch, "E2007", {"start": v(-2.71, -378.13) * mm, "end": v(-2.7, -377.93) * mm});
            skLineSegment(sketch, "E2008", {"start": v(-4.08, -377.93) * mm, "end": v(-4.09, -377.83) * mm});
            skLineSegment(sketch, "E2009", {"start": v(-4.09, -377.83) * mm, "end": v(-4.1, -377.72) * mm});
            skLineSegment(sketch, "E2010", {"start": v(-4.1, -377.72) * mm, "end": v(-4.11, -377.61) * mm});
            skLineSegment(sketch, "E2011", {"start": v(-4.11, -377.61) * mm, "end": v(-4.14, -377.5) * mm});
            skLineSegment(sketch, "E2012", {"start": v(-4.14, -377.5) * mm, "end": v(-4.17, -377.4) * mm});
            skLineSegment(sketch, "E2013", {"start": v(-4.17, -377.4) * mm, "end": v(-4.2, -377.3) * mm});
            skLineSegment(sketch, "E2014", {"start": v(-4.2, -377.3) * mm, "end": v(-4.25, -377.2) * mm});
            skLineSegment(sketch, "E2015", {"start": v(-4.25, -377.2) * mm, "end": v(-4.3, -377.1) * mm});
            skLineSegment(sketch, "E2016", {"start": v(-4.3, -377.1) * mm, "end": v(-4.36, -377.01) * mm});
            skLineSegment(sketch, "E2017", {"start": v(-4.36, -377.01) * mm, "end": v(-4.43, -376.93) * mm});
            skLineSegment(sketch, "E2018", {"start": v(-4.43, -376.93) * mm, "end": v(-4.5, -376.84) * mm});
            skLineSegment(sketch, "E2019", {"start": v(-4.5, -376.84) * mm, "end": v(-4.57, -376.76) * mm});
            skLineSegment(sketch, "E2020", {"start": v(-4.57, -376.76) * mm, "end": v(-4.65, -376.69) * mm});
            skLineSegment(sketch, "E2021", {"start": v(-4.65, -376.69) * mm, "end": v(-4.73, -376.62) * mm});
            skLineSegment(sketch, "E2022", {"start": v(-4.73, -376.62) * mm, "end": v(-4.82, -376.56) * mm});
            skLineSegment(sketch, "E2023", {"start": v(-4.82, -376.56) * mm, "end": v(-4.91, -376.5) * mm});
            skLineSegment(sketch, "E2024", {"start": v(-4.91, -376.5) * mm, "end": v(-5, -376.45) * mm});
            skLineSegment(sketch, "E2025", {"start": v(-5, -376.45) * mm, "end": v(-5.1, -376.4) * mm});
            skLineSegment(sketch, "E2026", {"start": v(-5.1, -376.4) * mm, "end": v(-5.2, -376.37) * mm});
            skLineSegment(sketch, "E2027", {"start": v(-5.2, -376.37) * mm, "end": v(-5.3, -376.33) * mm});
            skLineSegment(sketch, "E2028", {"start": v(-5.3, -376.33) * mm, "end": v(-5.42, -376.31) * mm});
            skLineSegment(sketch, "E2029", {"start": v(-5.42, -376.31) * mm, "end": v(-5.52, -376.3) * mm});
            skLineSegment(sketch, "E2030", {"start": v(-5.52, -376.3) * mm, "end": v(-5.63, -376.28) * mm});
            skLineSegment(sketch, "E2031", {"start": v(-5.63, -376.28) * mm, "end": v(-5.74, -376.28) * mm});
            skLineSegment(sketch, "E2032", {"start": v(-5.74, -376.28) * mm, "end": v(-5.85, -376.28) * mm});
            skLineSegment(sketch, "E2033", {"start": v(-5.85, -376.28) * mm, "end": v(-5.95, -376.3) * mm});
            skLineSegment(sketch, "E2034", {"start": v(-5.95, -376.3) * mm, "end": v(-6.06, -376.31) * mm});
            skLineSegment(sketch, "E2035", {"start": v(-6.06, -376.31) * mm, "end": v(-6.17, -376.33) * mm});
            skLineSegment(sketch, "E2036", {"start": v(-6.17, -376.33) * mm, "end": v(-6.27, -376.37) * mm});
            skLineSegment(sketch, "E2037", {"start": v(-6.27, -376.37) * mm, "end": v(-6.37, -376.4) * mm});
            skLineSegment(sketch, "E2038", {"start": v(-6.37, -376.4) * mm, "end": v(-6.47, -376.45) * mm});
            skLineSegment(sketch, "E2039", {"start": v(-6.47, -376.45) * mm, "end": v(-6.57, -376.5) * mm});
            skLineSegment(sketch, "E2040", {"start": v(-6.57, -376.5) * mm, "end": v(-6.66, -376.56) * mm});
            skLineSegment(sketch, "E2041", {"start": v(-6.66, -376.56) * mm, "end": v(-6.75, -376.62) * mm});
            skLineSegment(sketch, "E2042", {"start": v(-6.75, -376.62) * mm, "end": v(-6.83, -376.69) * mm});
            skLineSegment(sketch, "E2043", {"start": v(-6.83, -376.69) * mm, "end": v(-6.9, -376.76) * mm});
            skLineSegment(sketch, "E2044", {"start": v(-6.9, -376.76) * mm, "end": v(-6.98, -376.84) * mm});
            skLineSegment(sketch, "E2045", {"start": v(-6.98, -376.84) * mm, "end": v(-7.05, -376.93) * mm});
            skLineSegment(sketch, "E2046", {"start": v(-7.05, -376.93) * mm, "end": v(-7.11, -377.01) * mm});
            skLineSegment(sketch, "E2047", {"start": v(-7.11, -377.01) * mm, "end": v(-7.17, -377.1) * mm});
            skLineSegment(sketch, "E2048", {"start": v(-7.17, -377.1) * mm, "end": v(-7.22, -377.2) * mm});
            skLineSegment(sketch, "E2049", {"start": v(-7.22, -377.2) * mm, "end": v(-7.27, -377.3) * mm});
            skLineSegment(sketch, "E2050", {"start": v(-7.27, -377.3) * mm, "end": v(-7.3, -377.4) * mm});
            skLineSegment(sketch, "E2051", {"start": v(-7.3, -377.4) * mm, "end": v(-7.34, -377.5) * mm});
            skLineSegment(sketch, "E2052", {"start": v(-7.34, -377.5) * mm, "end": v(-7.36, -377.61) * mm});
            skLineSegment(sketch, "E2053", {"start": v(-7.36, -377.61) * mm, "end": v(-7.38, -377.72) * mm});
            skLineSegment(sketch, "E2054", {"start": v(-7.38, -377.72) * mm, "end": v(-7.4, -377.83) * mm});
            skLineSegment(sketch, "E2055", {"start": v(-7.4, -377.83) * mm, "end": v(-7.4, -377.93) * mm});
            skLineSegment(sketch, "E2056", {"start": v(-7.4, -377.93) * mm, "end": v(-7.4, -378.04) * mm});
            skLineSegment(sketch, "E2057", {"start": v(-7.4, -378.04) * mm, "end": v(-7.38, -378.15) * mm});
            skLineSegment(sketch, "E2058", {"start": v(-7.38, -378.15) * mm, "end": v(-7.36, -378.26) * mm});
            skLineSegment(sketch, "E2059", {"start": v(-7.36, -378.26) * mm, "end": v(-7.34, -378.36) * mm});
            skLineSegment(sketch, "E2060", {"start": v(-7.34, -378.36) * mm, "end": v(-7.3, -378.47) * mm});
            skLineSegment(sketch, "E2061", {"start": v(-7.3, -378.47) * mm, "end": v(-7.27, -378.57) * mm});
            skLineSegment(sketch, "E2062", {"start": v(-7.27, -378.57) * mm, "end": v(-7.22, -378.67) * mm});
            skLineSegment(sketch, "E2063", {"start": v(-7.22, -378.67) * mm, "end": v(-7.17, -378.76) * mm});
            skLineSegment(sketch, "E2064", {"start": v(-7.17, -378.76) * mm, "end": v(-7.11, -378.85) * mm});
            skLineSegment(sketch, "E2065", {"start": v(-7.11, -378.85) * mm, "end": v(-7.05, -378.94) * mm});
            skLineSegment(sketch, "E2066", {"start": v(-7.05, -378.94) * mm, "end": v(-6.98, -379.03) * mm});
            skLineSegment(sketch, "E2067", {"start": v(-6.98, -379.03) * mm, "end": v(-6.9, -379.1) * mm});
            skLineSegment(sketch, "E2068", {"start": v(-6.9, -379.1) * mm, "end": v(-6.83, -379.18) * mm});
            skLineSegment(sketch, "E2069", {"start": v(-6.83, -379.18) * mm, "end": v(-6.75, -379.25) * mm});
            skLineSegment(sketch, "E2070", {"start": v(-6.75, -379.25) * mm, "end": v(-6.66, -379.31) * mm});
            skLineSegment(sketch, "E2071", {"start": v(-6.66, -379.31) * mm, "end": v(-6.57, -379.37) * mm});
            skLineSegment(sketch, "E2072", {"start": v(-6.57, -379.37) * mm, "end": v(-6.47, -379.42) * mm});
            skLineSegment(sketch, "E2073", {"start": v(-6.47, -379.42) * mm, "end": v(-6.37, -379.46) * mm});
            skLineSegment(sketch, "E2074", {"start": v(-6.37, -379.46) * mm, "end": v(-6.27, -379.5) * mm});
            skLineSegment(sketch, "E2075", {"start": v(-6.27, -379.5) * mm, "end": v(-6.17, -379.53) * mm});
            skLineSegment(sketch, "E2076", {"start": v(-6.17, -379.53) * mm, "end": v(-6.06, -379.56) * mm});
            skLineSegment(sketch, "E2077", {"start": v(-6.06, -379.56) * mm, "end": v(-5.95, -379.58) * mm});
            skLineSegment(sketch, "E2078", {"start": v(-5.95, -379.58) * mm, "end": v(-5.85, -379.59) * mm});
            skLineSegment(sketch, "E2079", {"start": v(-5.85, -379.59) * mm, "end": v(-5.74, -379.59) * mm});
            skLineSegment(sketch, "E2080", {"start": v(-5.74, -379.59) * mm, "end": v(-5.63, -379.59) * mm});
            skLineSegment(sketch, "E2081", {"start": v(-5.63, -379.59) * mm, "end": v(-5.52, -379.58) * mm});
            skLineSegment(sketch, "E2082", {"start": v(-5.52, -379.58) * mm, "end": v(-5.42, -379.56) * mm});
            skLineSegment(sketch, "E2083", {"start": v(-5.42, -379.56) * mm, "end": v(-5.3, -379.53) * mm});
            skLineSegment(sketch, "E2084", {"start": v(-5.3, -379.53) * mm, "end": v(-5.2, -379.5) * mm});
            skLineSegment(sketch, "E2085", {"start": v(-5.2, -379.5) * mm, "end": v(-5.1, -379.46) * mm});
            skLineSegment(sketch, "E2086", {"start": v(-5.1, -379.46) * mm, "end": v(-5, -379.42) * mm});
            skLineSegment(sketch, "E2087", {"start": v(-5, -379.42) * mm, "end": v(-4.91, -379.37) * mm});
            skLineSegment(sketch, "E2088", {"start": v(-4.91, -379.37) * mm, "end": v(-4.82, -379.31) * mm});
            skLineSegment(sketch, "E2089", {"start": v(-4.82, -379.31) * mm, "end": v(-4.73, -379.25) * mm});
            skLineSegment(sketch, "E2090", {"start": v(-4.73, -379.25) * mm, "end": v(-4.65, -379.18) * mm});
            skLineSegment(sketch, "E2091", {"start": v(-4.65, -379.18) * mm, "end": v(-4.57, -379.1) * mm});
            skLineSegment(sketch, "E2092", {"start": v(-4.57, -379.1) * mm, "end": v(-4.5, -379.03) * mm});
            skLineSegment(sketch, "E2093", {"start": v(-4.5, -379.03) * mm, "end": v(-4.43, -378.94) * mm});
            skLineSegment(sketch, "E2094", {"start": v(-4.43, -378.94) * mm, "end": v(-4.36, -378.85) * mm});
            skLineSegment(sketch, "E2095", {"start": v(-4.36, -378.85) * mm, "end": v(-4.3, -378.76) * mm});
            skLineSegment(sketch, "E2096", {"start": v(-4.3, -378.76) * mm, "end": v(-4.25, -378.67) * mm});
            skLineSegment(sketch, "E2097", {"start": v(-4.25, -378.67) * mm, "end": v(-4.2, -378.57) * mm});
            skLineSegment(sketch, "E2098", {"start": v(-4.2, -378.57) * mm, "end": v(-4.17, -378.47) * mm});
            skLineSegment(sketch, "E2099", {"start": v(-4.17, -378.47) * mm, "end": v(-4.14, -378.36) * mm});
            skLineSegment(sketch, "E2100", {"start": v(-4.14, -378.36) * mm, "end": v(-4.11, -378.26) * mm});
            skLineSegment(sketch, "E2101", {"start": v(-4.11, -378.26) * mm, "end": v(-4.1, -378.15) * mm});
            skLineSegment(sketch, "E2102", {"start": v(-4.1, -378.15) * mm, "end": v(-4.09, -378.04) * mm});
            skLineSegment(sketch, "E2103", {"start": v(-4.09, -378.04) * mm, "end": v(-4.08, -377.93) * mm});
            skLineSegment(sketch, "E2104", {"start": v(31.73, -377.93) * mm, "end": v(31.72, -377.74) * mm});
            skLineSegment(sketch, "E2105", {"start": v(31.72, -377.74) * mm, "end": v(31.7, -377.54) * mm});
            skLineSegment(sketch, "E2106", {"start": v(31.7, -377.54) * mm, "end": v(31.67, -377.34) * mm});
            skLineSegment(sketch, "E2107", {"start": v(31.67, -377.34) * mm, "end": v(31.62, -377.15) * mm});
            skLineSegment(sketch, "E2108", {"start": v(31.62, -377.15) * mm, "end": v(31.57, -376.96) * mm});
            skLineSegment(sketch, "E2109", {"start": v(31.57, -376.96) * mm, "end": v(31.5, -376.77) * mm});
            skLineSegment(sketch, "E2110", {"start": v(31.5, -376.77) * mm, "end": v(31.41, -376.6) * mm});
            skLineSegment(sketch, "E2111", {"start": v(31.41, -376.6) * mm, "end": v(31.32, -376.42) * mm});
            skLineSegment(sketch, "E2112", {"start": v(31.32, -376.42) * mm, "end": v(31.22, -376.25) * mm});
            skLineSegment(sketch, "E2113", {"start": v(31.22, -376.25) * mm, "end": v(31.1, -376.09) * mm});
            skLineSegment(sketch, "E2114", {"start": v(31.1, -376.09) * mm, "end": v(30.97, -375.93) * mm});
            skLineSegment(sketch, "E2115", {"start": v(30.97, -375.93) * mm, "end": v(30.84, -375.79) * mm});
            skLineSegment(sketch, "E2116", {"start": v(30.84, -375.79) * mm, "end": v(30.7, -375.65) * mm});
            skLineSegment(sketch, "E2117", {"start": v(30.7, -375.65) * mm, "end": v(30.54, -375.53) * mm});
            skLineSegment(sketch, "E2118", {"start": v(30.54, -375.53) * mm, "end": v(30.38, -375.41) * mm});
            skLineSegment(sketch, "E2119", {"start": v(30.38, -375.41) * mm, "end": v(30.2, -375.3) * mm});
            skLineSegment(sketch, "E2120", {"start": v(30.2, -375.3) * mm, "end": v(30.03, -375.21) * mm});
            skLineSegment(sketch, "E2121", {"start": v(30.03, -375.21) * mm, "end": v(29.85, -375.13) * mm});
            skLineSegment(sketch, "E2122", {"start": v(29.85, -375.13) * mm, "end": v(29.67, -375.06) * mm});
            skLineSegment(sketch, "E2123", {"start": v(29.67, -375.06) * mm, "end": v(29.48, -375) * mm});
            skLineSegment(sketch, "E2124", {"start": v(29.48, -375) * mm, "end": v(29.28, -374.96) * mm});
            skLineSegment(sketch, "E2125", {"start": v(29.28, -374.96) * mm, "end": v(29.09, -374.93) * mm});
            skLineSegment(sketch, "E2126", {"start": v(29.09, -374.93) * mm, "end": v(28.9, -374.9) * mm});
            skLineSegment(sketch, "E2127", {"start": v(28.9, -374.9) * mm, "end": v(28.7, -374.9) * mm});
            skLineSegment(sketch, "E2128", {"start": v(28.7, -374.9) * mm, "end": v(28.5, -374.9) * mm});
            skLineSegment(sketch, "E2129", {"start": v(28.5, -374.9) * mm, "end": v(28.3, -374.93) * mm});
            skLineSegment(sketch, "E2130", {"start": v(28.3, -374.93) * mm, "end": v(28.1, -374.96) * mm});
            skLineSegment(sketch, "E2131", {"start": v(28.1, -374.96) * mm, "end": v(27.9, -375) * mm});
            skLineSegment(sketch, "E2132", {"start": v(27.9, -375) * mm, "end": v(27.72, -375.06) * mm});
            skLineSegment(sketch, "E2133", {"start": v(27.72, -375.06) * mm, "end": v(27.53, -375.13) * mm});
            skLineSegment(sketch, "E2134", {"start": v(27.53, -375.13) * mm, "end": v(27.35, -375.21) * mm});
            skLineSegment(sketch, "E2135", {"start": v(27.35, -375.21) * mm, "end": v(27.17, -375.3) * mm});
            skLineSegment(sketch, "E2136", {"start": v(27.17, -375.3) * mm, "end": v(27, -375.41) * mm});
            skLineSegment(sketch, "E2137", {"start": v(27, -375.41) * mm, "end": v(26.84, -375.53) * mm});
            skLineSegment(sketch, "E2138", {"start": v(26.84, -375.53) * mm, "end": v(26.7, -375.65) * mm});
            skLineSegment(sketch, "E2139", {"start": v(26.7, -375.65) * mm, "end": v(26.55, -375.79) * mm});
            skLineSegment(sketch, "E2140", {"start": v(26.55, -375.79) * mm, "end": v(26.41, -375.93) * mm});
            skLineSegment(sketch, "E2141", {"start": v(26.41, -375.93) * mm, "end": v(26.28, -376.09) * mm});
            skLineSegment(sketch, "E2142", {"start": v(26.28, -376.09) * mm, "end": v(26.17, -376.25) * mm});
            skLineSegment(sketch, "E2143", {"start": v(26.17, -376.25) * mm, "end": v(26.06, -376.42) * mm});
            skLineSegment(sketch, "E2144", {"start": v(26.06, -376.42) * mm, "end": v(25.97, -376.6) * mm});
            skLineSegment(sketch, "E2145", {"start": v(25.97, -376.6) * mm, "end": v(25.89, -376.77) * mm});
            skLineSegment(sketch, "E2146", {"start": v(25.89, -376.77) * mm, "end": v(25.82, -376.96) * mm});
            skLineSegment(sketch, "E2147", {"start": v(25.82, -376.96) * mm, "end": v(25.76, -377.15) * mm});
            skLineSegment(sketch, "E2148", {"start": v(25.76, -377.15) * mm, "end": v(25.72, -377.34) * mm});
            skLineSegment(sketch, "E2149", {"start": v(25.72, -377.34) * mm, "end": v(25.68, -377.54) * mm});
            skLineSegment(sketch, "E2150", {"start": v(25.68, -377.54) * mm, "end": v(25.66, -377.74) * mm});
            skLineSegment(sketch, "E2151", {"start": v(25.66, -377.74) * mm, "end": v(25.66, -377.93) * mm});
            skLineSegment(sketch, "E2152", {"start": v(25.66, -377.93) * mm, "end": v(25.66, -378.13) * mm});
            skLineSegment(sketch, "E2153", {"start": v(25.66, -378.13) * mm, "end": v(25.68, -378.33) * mm});
            skLineSegment(sketch, "E2154", {"start": v(25.68, -378.33) * mm, "end": v(25.72, -378.53) * mm});
            skLineSegment(sketch, "E2155", {"start": v(25.72, -378.53) * mm, "end": v(25.76, -378.72) * mm});
            skLineSegment(sketch, "E2156", {"start": v(25.76, -378.72) * mm, "end": v(25.82, -378.9) * mm});
            skLineSegment(sketch, "E2157", {"start": v(25.82, -378.9) * mm, "end": v(25.89, -379.1) * mm});
            skLineSegment(sketch, "E2158", {"start": v(25.89, -379.1) * mm, "end": v(25.97, -379.28) * mm});
            skLineSegment(sketch, "E2159", {"start": v(25.97, -379.28) * mm, "end": v(26.06, -379.45) * mm});
            skLineSegment(sketch, "E2160", {"start": v(26.06, -379.45) * mm, "end": v(26.17, -379.62) * mm});
            skLineSegment(sketch, "E2161", {"start": v(26.17, -379.62) * mm, "end": v(26.28, -379.78) * mm});
            skLineSegment(sketch, "E2162", {"start": v(26.28, -379.78) * mm, "end": v(26.41, -379.93) * mm});
            skLineSegment(sketch, "E2163", {"start": v(26.41, -379.93) * mm, "end": v(26.55, -380.08) * mm});
            skLineSegment(sketch, "E2164", {"start": v(26.55, -380.08) * mm, "end": v(26.7, -380.22) * mm});
            skLineSegment(sketch, "E2165", {"start": v(26.7, -380.22) * mm, "end": v(26.84, -380.34) * mm});
            skLineSegment(sketch, "E2166", {"start": v(26.84, -380.34) * mm, "end": v(27, -380.46) * mm});
            skLineSegment(sketch, "E2167", {"start": v(27, -380.46) * mm, "end": v(27.17, -380.56) * mm});
            skLineSegment(sketch, "E2168", {"start": v(27.17, -380.56) * mm, "end": v(27.35, -380.66) * mm});
            skLineSegment(sketch, "E2169", {"start": v(27.35, -380.66) * mm, "end": v(27.53, -380.74) * mm});
            skLineSegment(sketch, "E2170", {"start": v(27.53, -380.74) * mm, "end": v(27.72, -380.8) * mm});
            skLineSegment(sketch, "E2171", {"start": v(27.72, -380.8) * mm, "end": v(27.9, -380.87) * mm});
            skLineSegment(sketch, "E2172", {"start": v(27.9, -380.87) * mm, "end": v(28.1, -380.91) * mm});
            skLineSegment(sketch, "E2173", {"start": v(28.1, -380.91) * mm, "end": v(28.3, -380.94) * mm});
            skLineSegment(sketch, "E2174", {"start": v(28.3, -380.94) * mm, "end": v(28.5, -380.96) * mm});
            skLineSegment(sketch, "E2175", {"start": v(28.5, -380.96) * mm, "end": v(28.7, -380.97) * mm});
            skLineSegment(sketch, "E2176", {"start": v(28.7, -380.97) * mm, "end": v(28.9, -380.96) * mm});
            skLineSegment(sketch, "E2177", {"start": v(28.9, -380.96) * mm, "end": v(29.09, -380.94) * mm});
            skLineSegment(sketch, "E2178", {"start": v(29.09, -380.94) * mm, "end": v(29.28, -380.91) * mm});
            skLineSegment(sketch, "E2179", {"start": v(29.28, -380.91) * mm, "end": v(29.48, -380.87) * mm});
            skLineSegment(sketch, "E2180", {"start": v(29.48, -380.87) * mm, "end": v(29.67, -380.8) * mm});
            skLineSegment(sketch, "E2181", {"start": v(29.67, -380.8) * mm, "end": v(29.85, -380.74) * mm});
            skLineSegment(sketch, "E2182", {"start": v(29.85, -380.74) * mm, "end": v(30.03, -380.66) * mm});
            skLineSegment(sketch, "E2183", {"start": v(30.03, -380.66) * mm, "end": v(30.2, -380.56) * mm});
            skLineSegment(sketch, "E2184", {"start": v(30.2, -380.56) * mm, "end": v(30.38, -380.46) * mm});
            skLineSegment(sketch, "E2185", {"start": v(30.38, -380.46) * mm, "end": v(30.54, -380.34) * mm});
            skLineSegment(sketch, "E2186", {"start": v(30.54, -380.34) * mm, "end": v(30.7, -380.22) * mm});
            skLineSegment(sketch, "E2187", {"start": v(30.7, -380.22) * mm, "end": v(30.84, -380.08) * mm});
            skLineSegment(sketch, "E2188", {"start": v(30.84, -380.08) * mm, "end": v(30.97, -379.93) * mm});
            skLineSegment(sketch, "E2189", {"start": v(30.97, -379.93) * mm, "end": v(31.1, -379.78) * mm});
            skLineSegment(sketch, "E2190", {"start": v(31.1, -379.78) * mm, "end": v(31.22, -379.62) * mm});
            skLineSegment(sketch, "E2191", {"start": v(31.22, -379.62) * mm, "end": v(31.32, -379.45) * mm});
            skLineSegment(sketch, "E2192", {"start": v(31.32, -379.45) * mm, "end": v(31.41, -379.28) * mm});
            skLineSegment(sketch, "E2193", {"start": v(31.41, -379.28) * mm, "end": v(31.5, -379.1) * mm});
            skLineSegment(sketch, "E2194", {"start": v(31.5, -379.1) * mm, "end": v(31.57, -378.9) * mm});
            skLineSegment(sketch, "E2195", {"start": v(31.57, -378.9) * mm, "end": v(31.62, -378.72) * mm});
            skLineSegment(sketch, "E2196", {"start": v(31.62, -378.72) * mm, "end": v(31.67, -378.53) * mm});
            skLineSegment(sketch, "E2197", {"start": v(31.67, -378.53) * mm, "end": v(31.7, -378.33) * mm});
            skLineSegment(sketch, "E2198", {"start": v(31.7, -378.33) * mm, "end": v(31.72, -378.13) * mm});
            skLineSegment(sketch, "E2199", {"start": v(31.72, -378.13) * mm, "end": v(31.73, -377.93) * mm});
            skLineSegment(sketch, "E2200", {"start": v(30.35, -377.93) * mm, "end": v(30.34, -377.83) * mm});
            skLineSegment(sketch, "E2201", {"start": v(30.34, -377.83) * mm, "end": v(30.33, -377.72) * mm});
            skLineSegment(sketch, "E2202", {"start": v(30.33, -377.72) * mm, "end": v(30.32, -377.61) * mm});
            skLineSegment(sketch, "E2203", {"start": v(30.32, -377.61) * mm, "end": v(30.3, -377.5) * mm});
            skLineSegment(sketch, "E2204", {"start": v(30.3, -377.5) * mm, "end": v(30.26, -377.4) * mm});
            skLineSegment(sketch, "E2205", {"start": v(30.26, -377.4) * mm, "end": v(30.22, -377.3) * mm});
            skLineSegment(sketch, "E2206", {"start": v(30.22, -377.3) * mm, "end": v(30.18, -377.2) * mm});
            skLineSegment(sketch, "E2207", {"start": v(30.18, -377.2) * mm, "end": v(30.13, -377.1) * mm});
            skLineSegment(sketch, "E2208", {"start": v(30.13, -377.1) * mm, "end": v(30.07, -377.01) * mm});
            skLineSegment(sketch, "E2209", {"start": v(30.07, -377.01) * mm, "end": v(30, -376.93) * mm});
            skLineSegment(sketch, "E2210", {"start": v(30, -376.93) * mm, "end": v(29.94, -376.84) * mm});
            skLineSegment(sketch, "E2211", {"start": v(29.94, -376.84) * mm, "end": v(29.86, -376.76) * mm});
            skLineSegment(sketch, "E2212", {"start": v(29.86, -376.76) * mm, "end": v(29.78, -376.69) * mm});
            skLineSegment(sketch, "E2213", {"start": v(29.78, -376.69) * mm, "end": v(29.7, -376.62) * mm});
            skLineSegment(sketch, "E2214", {"start": v(29.7, -376.62) * mm, "end": v(29.61, -376.56) * mm});
            skLineSegment(sketch, "E2215", {"start": v(29.61, -376.56) * mm, "end": v(29.52, -376.5) * mm});
            skLineSegment(sketch, "E2216", {"start": v(29.52, -376.5) * mm, "end": v(29.42, -376.45) * mm});
            skLineSegment(sketch, "E2217", {"start": v(29.42, -376.45) * mm, "end": v(29.33, -376.4) * mm});
            skLineSegment(sketch, "E2218", {"start": v(29.33, -376.4) * mm, "end": v(29.22, -376.37) * mm});
            skLineSegment(sketch, "E2219", {"start": v(29.22, -376.37) * mm, "end": v(29.12, -376.33) * mm});
            skLineSegment(sketch, "E2220", {"start": v(29.12, -376.33) * mm, "end": v(29.01, -376.31) * mm});
            skLineSegment(sketch, "E2221", {"start": v(29.01, -376.31) * mm, "end": v(28.9, -376.3) * mm});
            skLineSegment(sketch, "E2222", {"start": v(28.9, -376.3) * mm, "end": v(28.8, -376.28) * mm});
            skLineSegment(sketch, "E2223", {"start": v(28.8, -376.28) * mm, "end": v(28.7, -376.28) * mm});
            skLineSegment(sketch, "E2224", {"start": v(28.7, -376.28) * mm, "end": v(28.58, -376.28) * mm});
            skLineSegment(sketch, "E2225", {"start": v(28.58, -376.28) * mm, "end": v(28.48, -376.3) * mm});
            skLineSegment(sketch, "E2226", {"start": v(28.48, -376.3) * mm, "end": v(28.37, -376.31) * mm});
            skLineSegment(sketch, "E2227", {"start": v(28.37, -376.31) * mm, "end": v(28.26, -376.33) * mm});
            skLineSegment(sketch, "E2228", {"start": v(28.26, -376.33) * mm, "end": v(28.16, -376.37) * mm});
            skLineSegment(sketch, "E2229", {"start": v(28.16, -376.37) * mm, "end": v(28.06, -376.4) * mm});
            skLineSegment(sketch, "E2230", {"start": v(28.06, -376.4) * mm, "end": v(27.96, -376.45) * mm});
            skLineSegment(sketch, "E2231", {"start": v(27.96, -376.45) * mm, "end": v(27.86, -376.5) * mm});
            skLineSegment(sketch, "E2232", {"start": v(27.86, -376.5) * mm, "end": v(27.77, -376.56) * mm});
            skLineSegment(sketch, "E2233", {"start": v(27.77, -376.56) * mm, "end": v(27.68, -376.62) * mm});
            skLineSegment(sketch, "E2234", {"start": v(27.68, -376.62) * mm, "end": v(27.6, -376.69) * mm});
            skLineSegment(sketch, "E2235", {"start": v(27.6, -376.69) * mm, "end": v(27.52, -376.76) * mm});
            skLineSegment(sketch, "E2236", {"start": v(27.52, -376.76) * mm, "end": v(27.45, -376.84) * mm});
            skLineSegment(sketch, "E2237", {"start": v(27.45, -376.84) * mm, "end": v(27.38, -376.93) * mm});
            skLineSegment(sketch, "E2238", {"start": v(27.38, -376.93) * mm, "end": v(27.32, -377.01) * mm});
            skLineSegment(sketch, "E2239", {"start": v(27.32, -377.01) * mm, "end": v(27.26, -377.1) * mm});
            skLineSegment(sketch, "E2240", {"start": v(27.26, -377.1) * mm, "end": v(27.2, -377.2) * mm});
            skLineSegment(sketch, "E2241", {"start": v(27.2, -377.2) * mm, "end": v(27.16, -377.3) * mm});
            skLineSegment(sketch, "E2242", {"start": v(27.16, -377.3) * mm, "end": v(27.12, -377.4) * mm});
            skLineSegment(sketch, "E2243", {"start": v(27.12, -377.4) * mm, "end": v(27.1, -377.5) * mm});
            skLineSegment(sketch, "E2244", {"start": v(27.1, -377.5) * mm, "end": v(27.07, -377.61) * mm});
            skLineSegment(sketch, "E2245", {"start": v(27.07, -377.61) * mm, "end": v(27.05, -377.72) * mm});
            skLineSegment(sketch, "E2246", {"start": v(27.05, -377.72) * mm, "end": v(27.04, -377.83) * mm});
            skLineSegment(sketch, "E2247", {"start": v(27.04, -377.83) * mm, "end": v(27.04, -377.93) * mm});
            skLineSegment(sketch, "E2248", {"start": v(27.04, -377.93) * mm, "end": v(27.04, -378.04) * mm});
            skLineSegment(sketch, "E2249", {"start": v(27.04, -378.04) * mm, "end": v(27.05, -378.15) * mm});
            skLineSegment(sketch, "E2250", {"start": v(27.05, -378.15) * mm, "end": v(27.07, -378.26) * mm});
            skLineSegment(sketch, "E2251", {"start": v(27.07, -378.26) * mm, "end": v(27.1, -378.36) * mm});
            skLineSegment(sketch, "E2252", {"start": v(27.1, -378.36) * mm, "end": v(27.12, -378.47) * mm});
            skLineSegment(sketch, "E2253", {"start": v(27.12, -378.47) * mm, "end": v(27.16, -378.57) * mm});
            skLineSegment(sketch, "E2254", {"start": v(27.16, -378.57) * mm, "end": v(27.2, -378.67) * mm});
            skLineSegment(sketch, "E2255", {"start": v(27.2, -378.67) * mm, "end": v(27.26, -378.76) * mm});
            skLineSegment(sketch, "E2256", {"start": v(27.26, -378.76) * mm, "end": v(27.32, -378.85) * mm});
            skLineSegment(sketch, "E2257", {"start": v(27.32, -378.85) * mm, "end": v(27.38, -378.94) * mm});
            skLineSegment(sketch, "E2258", {"start": v(27.38, -378.94) * mm, "end": v(27.45, -379.03) * mm});
            skLineSegment(sketch, "E2259", {"start": v(27.45, -379.03) * mm, "end": v(27.52, -379.1) * mm});
            skLineSegment(sketch, "E2260", {"start": v(27.52, -379.1) * mm, "end": v(27.6, -379.18) * mm});
            skLineSegment(sketch, "E2261", {"start": v(27.6, -379.18) * mm, "end": v(27.68, -379.25) * mm});
            skLineSegment(sketch, "E2262", {"start": v(27.68, -379.25) * mm, "end": v(27.77, -379.31) * mm});
            skLineSegment(sketch, "E2263", {"start": v(27.77, -379.31) * mm, "end": v(27.86, -379.37) * mm});
            skLineSegment(sketch, "E2264", {"start": v(27.86, -379.37) * mm, "end": v(27.96, -379.42) * mm});
            skLineSegment(sketch, "E2265", {"start": v(27.96, -379.42) * mm, "end": v(28.06, -379.46) * mm});
            skLineSegment(sketch, "E2266", {"start": v(28.06, -379.46) * mm, "end": v(28.16, -379.5) * mm});
            skLineSegment(sketch, "E2267", {"start": v(28.16, -379.5) * mm, "end": v(28.26, -379.53) * mm});
            skLineSegment(sketch, "E2268", {"start": v(28.26, -379.53) * mm, "end": v(28.37, -379.56) * mm});
            skLineSegment(sketch, "E2269", {"start": v(28.37, -379.56) * mm, "end": v(28.48, -379.58) * mm});
            skLineSegment(sketch, "E2270", {"start": v(28.48, -379.58) * mm, "end": v(28.58, -379.59) * mm});
            skLineSegment(sketch, "E2271", {"start": v(28.58, -379.59) * mm, "end": v(28.7, -379.59) * mm});
            skLineSegment(sketch, "E2272", {"start": v(28.7, -379.59) * mm, "end": v(28.8, -379.59) * mm});
            skLineSegment(sketch, "E2273", {"start": v(28.8, -379.59) * mm, "end": v(28.9, -379.58) * mm});
            skLineSegment(sketch, "E2274", {"start": v(28.9, -379.58) * mm, "end": v(29.01, -379.56) * mm});
            skLineSegment(sketch, "E2275", {"start": v(29.01, -379.56) * mm, "end": v(29.12, -379.53) * mm});
            skLineSegment(sketch, "E2276", {"start": v(29.12, -379.53) * mm, "end": v(29.22, -379.5) * mm});
            skLineSegment(sketch, "E2277", {"start": v(29.22, -379.5) * mm, "end": v(29.33, -379.46) * mm});
            skLineSegment(sketch, "E2278", {"start": v(29.33, -379.46) * mm, "end": v(29.42, -379.42) * mm});
            skLineSegment(sketch, "E2279", {"start": v(29.42, -379.42) * mm, "end": v(29.52, -379.37) * mm});
            skLineSegment(sketch, "E2280", {"start": v(29.52, -379.37) * mm, "end": v(29.61, -379.31) * mm});
            skLineSegment(sketch, "E2281", {"start": v(29.61, -379.31) * mm, "end": v(29.7, -379.25) * mm});
            skLineSegment(sketch, "E2282", {"start": v(29.7, -379.25) * mm, "end": v(29.78, -379.18) * mm});
            skLineSegment(sketch, "E2283", {"start": v(29.78, -379.18) * mm, "end": v(29.86, -379.1) * mm});
            skLineSegment(sketch, "E2284", {"start": v(29.86, -379.1) * mm, "end": v(29.94, -379.03) * mm});
            skLineSegment(sketch, "E2285", {"start": v(29.94, -379.03) * mm, "end": v(30, -378.94) * mm});
            skLineSegment(sketch, "E2286", {"start": v(30, -378.94) * mm, "end": v(30.07, -378.85) * mm});
            skLineSegment(sketch, "E2287", {"start": v(30.07, -378.85) * mm, "end": v(30.13, -378.76) * mm});
            skLineSegment(sketch, "E2288", {"start": v(30.13, -378.76) * mm, "end": v(30.18, -378.67) * mm});
            skLineSegment(sketch, "E2289", {"start": v(30.18, -378.67) * mm, "end": v(30.22, -378.57) * mm});
            skLineSegment(sketch, "E2290", {"start": v(30.22, -378.57) * mm, "end": v(30.26, -378.47) * mm});
            skLineSegment(sketch, "E2291", {"start": v(30.26, -378.47) * mm, "end": v(30.3, -378.36) * mm});
            skLineSegment(sketch, "E2292", {"start": v(30.3, -378.36) * mm, "end": v(30.32, -378.26) * mm});
            skLineSegment(sketch, "E2293", {"start": v(30.32, -378.26) * mm, "end": v(30.33, -378.15) * mm});
            skLineSegment(sketch, "E2294", {"start": v(30.33, -378.15) * mm, "end": v(30.34, -378.04) * mm});
            skLineSegment(sketch, "E2295", {"start": v(30.34, -378.04) * mm, "end": v(30.35, -377.93) * mm});
            skLineSegment(sketch, "E2296", {"start": v(-20.2, 375.73) * mm, "end": v(-27.41, -135.98) * mm});
            skLineSegment(sketch, "E2297", {"start": v(27.44, -135.98) * mm, "end": v(20.2, 375.73) * mm});
            skLineSegment(sketch, "E2298", {"start": v(-31, -139.51) * mm, "end": v(31.02, -139.51) * mm});
            skLineSegment(sketch, "E2299", {"start": v(-27.41, -135.98) * mm, "end": v(27.44, -135.98) * mm});
            skLineSegment(sketch, "E2300", {"start": v(-18.76, 380.97) * mm, "end": v(-11.26, 380.97) * mm});
            skLineSegment(sketch, "E2301", {"start": v(-18.76, 375.78) * mm, "end": v(-11.26, 375.78) * mm});
            skLineSegment(sketch, "E2302", {"start": v(-30.84, -128.33) * mm, "end": v(-31, -139.51) * mm});
            skLineSegment(sketch, "E2303", {"start": v(-30.67, -116.63) * mm, "end": v(-30.84, -128.33) * mm});
            skLineSegment(sketch, "E2304", {"start": v(-30.5, -104.25) * mm, "end": v(-30.67, -116.63) * mm});
            skLineSegment(sketch, "E2305", {"start": v(-30.31, -91.12) * mm, "end": v(-30.5, -104.25) * mm});
            skLineSegment(sketch, "E2306", {"start": v(-30.12, -77.22) * mm, "end": v(-30.31, -91.12) * mm});
            skLineSegment(sketch, "E2307", {"start": v(-29.9, -62.48) * mm, "end": v(-30.12, -77.22) * mm});
            skLineSegment(sketch, "E2308", {"start": v(-29.69, -46.87) * mm, "end": v(-29.9, -62.48) * mm});
            skLineSegment(sketch, "E2309", {"start": v(-29.46, -30.34) * mm, "end": v(-29.69, -46.87) * mm});
            skLineSegment(sketch, "E2310", {"start": v(-29.2, -12.82) * mm, "end": v(-29.46, -30.34) * mm});
            skLineSegment(sketch, "E2311", {"start": v(-28.95, 5.74) * mm, "end": v(-29.2, -12.82) * mm});
            skLineSegment(sketch, "E2312", {"start": v(-28.67, 25.4) * mm, "end": v(-28.95, 5.74) * mm});
            skLineSegment(sketch, "E2313", {"start": v(-28.37, 46.24) * mm, "end": v(-28.67, 25.4) * mm});
            skLineSegment(sketch, "E2314", {"start": v(-28.06, 68.31) * mm, "end": v(-28.37, 46.24) * mm});
            skLineSegment(sketch, "E2315", {"start": v(-27.73, 91.7) * mm, "end": v(-28.06, 68.31) * mm});
            skLineSegment(sketch, "E2316", {"start": v(-27.38, 116.48) * mm, "end": v(-27.73, 91.7) * mm});
            skLineSegment(sketch, "E2317", {"start": v(-27.01, 142.73) * mm, "end": v(-27.38, 116.48) * mm});
            skLineSegment(sketch, "E2318", {"start": v(-26.62, 170.54) * mm, "end": v(-27.01, 142.73) * mm});
            skLineSegment(sketch, "E2319", {"start": v(-26.2, 200) * mm, "end": v(-26.62, 170.54) * mm});
            skLineSegment(sketch, "E2320", {"start": v(-25.77, 231.22) * mm, "end": v(-26.2, 200) * mm});
            skLineSegment(sketch, "E2321", {"start": v(-25.3, 264.29) * mm, "end": v(-25.77, 231.22) * mm});
            skLineSegment(sketch, "E2322", {"start": v(-24.8, 299.33) * mm, "end": v(-25.3, 264.29) * mm});
            skLineSegment(sketch, "E2323", {"start": v(-24.28, 336.45) * mm, "end": v(-24.8, 299.33) * mm});
            skLineSegment(sketch, "E2324", {"start": v(30.86, -128.33) * mm, "end": v(30.7, -116.63) * mm});
            skLineSegment(sketch, "E2325", {"start": v(-11.26, 380.97) * mm, "end": v(-3.75, 380.97) * mm});
            skLineSegment(sketch, "E2326", {"start": v(-11.26, 375.78) * mm, "end": v(-3.75, 375.78) * mm});
            skLineSegment(sketch, "E2327", {"start": v(30.7, -116.63) * mm, "end": v(30.52, -104.25) * mm});
            skLineSegment(sketch, "E2328", {"start": v(-3.75, 380.97) * mm, "end": v(3.75, 380.97) * mm});
            skLineSegment(sketch, "E2329", {"start": v(-3.75, 375.78) * mm, "end": v(3.75, 375.78) * mm});
            skLineSegment(sketch, "E2330", {"start": v(30.52, -104.25) * mm, "end": v(30.33, -91.12) * mm});
            skLineSegment(sketch, "E2331", {"start": v(3.75, 380.97) * mm, "end": v(11.26, 380.97) * mm});
            skLineSegment(sketch, "E2332", {"start": v(3.75, 375.78) * mm, "end": v(11.26, 375.78) * mm});
            skLineSegment(sketch, "E2333", {"start": v(30.33, -91.12) * mm, "end": v(30.14, -77.22) * mm});
            skLineSegment(sketch, "E2334", {"start": v(11.26, 380.97) * mm, "end": v(18.76, 380.97) * mm});
            skLineSegment(sketch, "E2335", {"start": v(11.26, 375.78) * mm, "end": v(18.76, 375.78) * mm});
            skLineSegment(sketch, "E2336", {"start": v(30.14, -77.22) * mm, "end": v(29.93, -62.48) * mm});
            skLineSegment(sketch, "E2337", {"start": v(18.76, 380.97) * mm, "end": v(23.73, 380.97) * mm});
            skLineSegment(sketch, "E2338", {"start": v(18.76, 375.78) * mm, "end": v(23.73, 375.78) * mm});
            skLineSegment(sketch, "E2339", {"start": v(29.93, -62.48) * mm, "end": v(29.7, -46.87) * mm});
            skLineSegment(sketch, "E2340", {"start": v(29.7, -46.87) * mm, "end": v(29.47, -30.34) * mm});
            skLineSegment(sketch, "E2341", {"start": v(29.47, -30.34) * mm, "end": v(29.23, -12.82) * mm});
            skLineSegment(sketch, "E2342", {"start": v(29.23, -12.82) * mm, "end": v(28.96, 5.74) * mm});
            skLineSegment(sketch, "E2343", {"start": v(28.96, 5.74) * mm, "end": v(28.68, 25.4) * mm});
            skLineSegment(sketch, "E2344", {"start": v(28.68, 25.4) * mm, "end": v(28.39, 46.24) * mm});
            skLineSegment(sketch, "E2345", {"start": v(28.39, 46.24) * mm, "end": v(28.08, 68.31) * mm});
            skLineSegment(sketch, "E2346", {"start": v(28.08, 68.31) * mm, "end": v(27.75, 91.7) * mm});
            skLineSegment(sketch, "E2347", {"start": v(27.75, 91.7) * mm, "end": v(27.4, 116.48) * mm});
            skLineSegment(sketch, "E2348", {"start": v(27.4, 116.48) * mm, "end": v(27.02, 142.73) * mm});
            skLineSegment(sketch, "E2349", {"start": v(27.02, 142.73) * mm, "end": v(26.63, 170.54) * mm});
            skLineSegment(sketch, "E2350", {"start": v(26.63, 170.54) * mm, "end": v(26.21, 200) * mm});
            skLineSegment(sketch, "E2351", {"start": v(26.21, 200) * mm, "end": v(25.77, 231.22) * mm});
            skLineSegment(sketch, "E2352", {"start": v(25.77, 231.22) * mm, "end": v(25.3, 264.29) * mm});
            skLineSegment(sketch, "E2353", {"start": v(25.3, 264.29) * mm, "end": v(24.8, 299.33) * mm});
            skLineSegment(sketch, "E2354", {"start": v(24.8, 299.33) * mm, "end": v(24.28, 336.45) * mm});
            skLineSegment(sketch, "E2355", {"start": v(24.28, 336.45) * mm, "end": v(23.73, 375.78) * mm});
            skSolve(sketch);
        }
        {
            var Q0;
            {var subQ5=sQuery(id+"F0.wireOp",EDGE,"E2326");Q0=makeQuery(id+"F0.imprint","IMPRINT",FACE,{"disambiguationData":[TD([[makeQuery(id+"F0.imprint","IMPRINT",EDGE,{"derivedFrom":subQ5}),-1.0]])]});}
            var sketch = newSketch(context, id + "F1", { "sketchPlane" : qUnion([Q0])});
            skLineSegment(sketch, "E2356.bottom", {"start": v(-23.73, 380.97) * mm, "end": v(23.73, 380.97) * mm});
            skLineSegment(sketch, "E2356.top", {"start": v(-31, -139.51) * mm, "end": v(31.02, -139.51) * mm});
            skLineSegment(sketch, "E2356.left", {"start": v(-23.73, 380.97) * mm, "end": v(-31, -139.51) * mm});
            skLineSegment(sketch, "E2356.right", {"start": v(23.73, 380.97) * mm, "end": v(31.02, -139.51) * mm});
            skSolve(sketch);
        }
        {
            var Q0;
            Q0 = qSketchRegion(id + "F1", true);
            extrude(context, id + "F2", {"entities" : qUnion([Q0]), "depth" : 25 * mm, "offsetDistance" : 25 * mm});
        }
        {
            var Q0;
            Q0=makeQuery(id+"F2.opExtrude","SWEPT_FACE",FACE,{"disambiguationData":[OSD([sQuery(id+"F1.wireOp",EDGE,"E2356.left")])]});
            var sketch = newSketch(context, id + "F3", { "sketchPlane" : qUnion([Q0])});
            skLineSegment(sketch, "E2357", {"start": v(-380.6, 2) * mm, "end": v(139.93, 2) * mm, "construction": true});
            skLineSegment(sketch, "E2358.bottom", {"start": v(-199.32, 0) * mm, "end": v(-199.92, 0) * mm});
            skLineSegment(sketch, "E2358.top", {"start": v(-199.32, 2) * mm, "end": v(-199.92, 2) * mm});
            skLineSegment(sketch, "E2358.left", {"start": v(-199.32, 0) * mm, "end": v(-199.32, 2) * mm});
            skLineSegment(sketch, "E2358.right", {"start": v(-199.92, 0) * mm, "end": v(-199.92, 2) * mm});
            skLineSegment(sketch, "E2359.bottom", {"start": v(-335.78, 0) * mm, "end": v(-336.38, 0) * mm});
            skLineSegment(sketch, "E2359.top", {"start": v(-335.78, 2) * mm, "end": v(-336.38, 2) * mm});
            skLineSegment(sketch, "E2359.left", {"start": v(-335.78, 0) * mm, "end": v(-335.78, 2) * mm});
            skLineSegment(sketch, "E2359.right", {"start": v(-336.38, 0) * mm, "end": v(-336.38, 2) * mm});
            skLineSegment(sketch, "E2360.bottom", {"start": v(-298.65, 0) * mm, "end": v(-299.25, 0) * mm});
            skLineSegment(sketch, "E2360.top", {"start": v(-298.65, 2) * mm, "end": v(-299.25, 2) * mm});
            skLineSegment(sketch, "E2360.left", {"start": v(-298.65, 0) * mm, "end": v(-298.65, 2) * mm});
            skLineSegment(sketch, "E2360.right", {"start": v(-299.25, 0) * mm, "end": v(-299.25, 2) * mm});
            skLineSegment(sketch, "E2361.bottom", {"start": v(-263.61, 0) * mm, "end": v(-264.21, 0) * mm});
            skLineSegment(sketch, "E2361.top", {"start": v(-263.61, 2) * mm, "end": v(-264.21, 2) * mm});
            skLineSegment(sketch, "E2361.left", {"start": v(-263.61, 0) * mm, "end": v(-263.61, 2) * mm});
            skLineSegment(sketch, "E2361.right", {"start": v(-264.21, 0) * mm, "end": v(-264.21, 2) * mm});
            skLineSegment(sketch, "E2362.bottom", {"start": v(-230.54, 0) * mm, "end": v(-231.14, 0) * mm});
            skLineSegment(sketch, "E2362.top", {"start": v(-230.54, 2) * mm, "end": v(-231.14, 2) * mm});
            skLineSegment(sketch, "E2362.left", {"start": v(-230.54, 0) * mm, "end": v(-230.54, 2) * mm});
            skLineSegment(sketch, "E2362.right", {"start": v(-231.14, 0) * mm, "end": v(-231.14, 2) * mm});
            skLineSegment(sketch, "E2363.bottom", {"start": v(-169.85, 0) * mm, "end": v(-170.45, 0) * mm});
            skLineSegment(sketch, "E2363.top", {"start": v(-169.85, 2) * mm, "end": v(-170.45, 2) * mm});
            skLineSegment(sketch, "E2363.left", {"start": v(-169.85, 0) * mm, "end": v(-169.85, 2) * mm});
            skLineSegment(sketch, "E2363.right", {"start": v(-170.45, 0) * mm, "end": v(-170.45, 2) * mm});
            skLineSegment(sketch, "E2364.bottom", {"start": v(-142.03, 0) * mm, "end": v(-142.63, 0) * mm});
            skLineSegment(sketch, "E2364.top", {"start": v(-142.03, 2) * mm, "end": v(-142.63, 2) * mm});
            skLineSegment(sketch, "E2364.left", {"start": v(-142.03, 0) * mm, "end": v(-142.03, 2) * mm});
            skLineSegment(sketch, "E2364.right", {"start": v(-142.63, 0) * mm, "end": v(-142.63, 2) * mm});
            skLineSegment(sketch, "E2365.bottom", {"start": v(-115.78, 0) * mm, "end": v(-116.38, 0) * mm});
            skLineSegment(sketch, "E2365.top", {"start": v(-115.78, 2) * mm, "end": v(-116.38, 2) * mm});
            skLineSegment(sketch, "E2365.left", {"start": v(-115.78, 0) * mm, "end": v(-115.78, 2) * mm});
            skLineSegment(sketch, "E2365.right", {"start": v(-116.38, 0) * mm, "end": v(-116.38, 2) * mm});
            skLineSegment(sketch, "E2366.bottom", {"start": v(-91, 0) * mm, "end": v(-91.6, 0) * mm});
            skLineSegment(sketch, "E2366.top", {"start": v(-91, 2) * mm, "end": v(-91.6, 2) * mm});
            skLineSegment(sketch, "E2366.left", {"start": v(-91, 0) * mm, "end": v(-91, 2) * mm});
            skLineSegment(sketch, "E2366.right", {"start": v(-91.6, 0) * mm, "end": v(-91.6, 2) * mm});
            skLineSegment(sketch, "E2367.bottom", {"start": v(-67.62, 0) * mm, "end": v(-68.22, 0) * mm});
            skLineSegment(sketch, "E2367.top", {"start": v(-67.62, 2) * mm, "end": v(-68.22, 2) * mm});
            skLineSegment(sketch, "E2367.left", {"start": v(-67.62, 0) * mm, "end": v(-67.62, 2) * mm});
            skLineSegment(sketch, "E2367.right", {"start": v(-68.22, 0) * mm, "end": v(-68.22, 2) * mm});
            skLineSegment(sketch, "E2368.bottom", {"start": v(-45.54, 0) * mm, "end": v(-46.14, 0) * mm});
            skLineSegment(sketch, "E2368.top", {"start": v(-45.54, 2) * mm, "end": v(-46.14, 2) * mm});
            skLineSegment(sketch, "E2368.left", {"start": v(-45.54, 0) * mm, "end": v(-45.54, 2) * mm});
            skLineSegment(sketch, "E2368.right", {"start": v(-46.14, 0) * mm, "end": v(-46.14, 2) * mm});
            skLineSegment(sketch, "E2369.bottom", {"start": v(-24.7, 0) * mm, "end": v(-25.3, 0) * mm});
            skLineSegment(sketch, "E2369.top", {"start": v(-24.7, 2) * mm, "end": v(-25.3, 2) * mm});
            skLineSegment(sketch, "E2369.left", {"start": v(-24.7, 0) * mm, "end": v(-24.7, 2) * mm});
            skLineSegment(sketch, "E2369.right", {"start": v(-25.3, 0) * mm, "end": v(-25.3, 2) * mm});
            skLineSegment(sketch, "E2370.bottom", {"start": v(-5.04, 0) * mm, "end": v(-5.64, 0) * mm});
            skLineSegment(sketch, "E2370.top", {"start": v(-5.04, 2) * mm, "end": v(-5.64, 2) * mm});
            skLineSegment(sketch, "E2370.left", {"start": v(-5.04, 0) * mm, "end": v(-5.04, 2) * mm});
            skLineSegment(sketch, "E2370.right", {"start": v(-5.64, 0) * mm, "end": v(-5.64, 2) * mm});
            skLineSegment(sketch, "E2371.bottom", {"start": v(13.53, 0) * mm, "end": v(12.93, 0) * mm});
            skLineSegment(sketch, "E2371.top", {"start": v(13.53, 2) * mm, "end": v(12.93, 2) * mm});
            skLineSegment(sketch, "E2371.left", {"start": v(13.53, 0) * mm, "end": v(13.53, 2) * mm});
            skLineSegment(sketch, "E2371.right", {"start": v(12.93, 0) * mm, "end": v(12.93, 2) * mm});
            skLineSegment(sketch, "E2372.bottom", {"start": v(31.05, 0) * mm, "end": v(30.45, 0) * mm});
            skLineSegment(sketch, "E2372.top", {"start": v(31.05, 2) * mm, "end": v(30.45, 2) * mm});
            skLineSegment(sketch, "E2372.left", {"start": v(31.05, 0) * mm, "end": v(31.05, 2) * mm});
            skLineSegment(sketch, "E2372.right", {"start": v(30.45, 0) * mm, "end": v(30.45, 2) * mm});
            skLineSegment(sketch, "E2373.bottom", {"start": v(47.58, 0) * mm, "end": v(46.98, 0) * mm});
            skLineSegment(sketch, "E2373.top", {"start": v(47.58, 2) * mm, "end": v(46.98, 2) * mm});
            skLineSegment(sketch, "E2373.left", {"start": v(47.58, 0) * mm, "end": v(47.58, 2) * mm});
            skLineSegment(sketch, "E2373.right", {"start": v(46.98, 0) * mm, "end": v(46.98, 2) * mm});
            skLineSegment(sketch, "E2374.bottom", {"start": v(63.2, 0) * mm, "end": v(62.6, 0) * mm});
            skLineSegment(sketch, "E2374.top", {"start": v(63.2, 2) * mm, "end": v(62.6, 2) * mm});
            skLineSegment(sketch, "E2374.left", {"start": v(63.2, 0) * mm, "end": v(63.2, 2) * mm});
            skLineSegment(sketch, "E2374.right", {"start": v(62.6, 0) * mm, "end": v(62.6, 2) * mm});
            skLineSegment(sketch, "E2375.bottom", {"start": v(136.65, 0) * mm, "end": v(136.05, 0) * mm});
            skLineSegment(sketch, "E2375.top", {"start": v(136.65, 2) * mm, "end": v(136.05, 2) * mm});
            skLineSegment(sketch, "E2375.left", {"start": v(136.65, 0) * mm, "end": v(136.65, 2) * mm});
            skLineSegment(sketch, "E2375.right", {"start": v(136.05, 0) * mm, "end": v(136.05, 2) * mm});
            skLineSegment(sketch, "E2376.bottom", {"start": v(77.93, 0) * mm, "end": v(77.33, 0) * mm});
            skLineSegment(sketch, "E2376.top", {"start": v(77.93, 2) * mm, "end": v(77.33, 2) * mm});
            skLineSegment(sketch, "E2376.left", {"start": v(77.93, 0) * mm, "end": v(77.93, 2) * mm});
            skLineSegment(sketch, "E2376.right", {"start": v(77.33, 0) * mm, "end": v(77.33, 2) * mm});
            skLineSegment(sketch, "E2377.bottom", {"start": v(91.83, 0) * mm, "end": v(91.23, 0) * mm});
            skLineSegment(sketch, "E2377.top", {"start": v(91.83, 2) * mm, "end": v(91.23, 2) * mm});
            skLineSegment(sketch, "E2377.left", {"start": v(91.83, 0) * mm, "end": v(91.83, 2) * mm});
            skLineSegment(sketch, "E2377.right", {"start": v(91.23, 0) * mm, "end": v(91.23, 2) * mm});
            skLineSegment(sketch, "E2378.bottom", {"start": v(104.96, 0) * mm, "end": v(104.36, 0) * mm});
            skLineSegment(sketch, "E2378.top", {"start": v(104.96, 2) * mm, "end": v(104.36, 2) * mm});
            skLineSegment(sketch, "E2378.left", {"start": v(104.96, 0) * mm, "end": v(104.96, 2) * mm});
            skLineSegment(sketch, "E2378.right", {"start": v(104.36, 0) * mm, "end": v(104.36, 2) * mm});
            skLineSegment(sketch, "E2379.bottom", {"start": v(117.35, 0) * mm, "end": v(116.75, 0) * mm});
            skLineSegment(sketch, "E2379.top", {"start": v(117.35, 2) * mm, "end": v(116.75, 2) * mm});
            skLineSegment(sketch, "E2379.left", {"start": v(117.35, 0) * mm, "end": v(117.35, 2) * mm});
            skLineSegment(sketch, "E2379.right", {"start": v(116.75, 0) * mm, "end": v(116.75, 2) * mm});
            skLineSegment(sketch, "E2380.bottom", {"start": v(129.04, 0) * mm, "end": v(128.44, 0) * mm});
            skLineSegment(sketch, "E2380.top", {"start": v(129.04, 2) * mm, "end": v(128.44, 2) * mm});
            skLineSegment(sketch, "E2380.left", {"start": v(129.04, 0) * mm, "end": v(129.04, 2) * mm});
            skLineSegment(sketch, "E2380.right", {"start": v(128.44, 0) * mm, "end": v(128.44, 2) * mm});
            skSolve(sketch);
        }
        {
            var Q0;
            Q0 = qSketchRegion(id + "F3", true);
            var Q1;
            Q1=sQuery(id+"F3.wireOp",EDGE,"E2359.right");
            var Q2;
            Q2=sQuery(id+"F3.wireOp",EDGE,"E2359.left");
            var Q3;
            Q3=sQuery(id+"F3.wireOp",EDGE,"E2358.right");
            var Q4;
            Q4=sQuery(id+"F3.wireOp",EDGE,"E2363.left");
            var Q5;
            Q5=sQuery(id+"F3.wireOp",EDGE,"E2360.right");
            var Q6;
            Q6=sQuery(id+"F3.wireOp",EDGE,"E2359.bottom");
            var Q7;
            Q7=sQuery(id+"F3.wireOp",EDGE,"E2364.right");
            var Q8;
            Q8=sQuery(id+"F3.wireOp",EDGE,"E2363.bottom");
            var Q9;
            Q9=sQuery(id+"F3.wireOp",EDGE,"E2359.top");
            var Q10;
            Q10=sQuery(id+"F3.wireOp",EDGE,"E2365.top");
            var Q11;
            Q11=sQuery(id+"F3.wireOp",EDGE,"E2361.right");
            var Q12;
            Q12=sQuery(id+"F3.wireOp",EDGE,"E2362.left");
            var Q13;
            Q13=sQuery(id+"F3.wireOp",EDGE,"E2365.right");
            var Q14;
            Q14=sQuery(id+"F3.wireOp",EDGE,"E2361.top");
            var Q15;
            Q15=sQuery(id+"F3.wireOp",EDGE,"E2366.left");
            var Q16;
            Q16=sQuery(id+"F3.wireOp",EDGE,"E2361.bottom");
            var Q17;
            Q17=sQuery(id+"F3.wireOp",EDGE,"E2366.top");
            var Q18;
            Q18=sQuery(id+"F3.wireOp",EDGE,"E2358.left");
            var Q19;
            Q19=sQuery(id+"F3.wireOp",EDGE,"E2364.bottom");
            var Q20;
            Q20=sQuery(id+"F3.wireOp",EDGE,"E2362.top");
            var Q21;
            Q21=sQuery(id+"F3.wireOp",EDGE,"E2363.top");
            var Q22;
            Q22=sQuery(id+"F3.wireOp",EDGE,"E2360.bottom");
            var Q23;
            Q23=sQuery(id+"F3.wireOp",EDGE,"E2366.bottom");
            var Q24;
            Q24=sQuery(id+"F3.wireOp",EDGE,"E2363.right");
            var Q25;
            Q25=sQuery(id+"F3.wireOp",EDGE,"E2360.top");
            var Q26;
            Q26=sQuery(id+"F3.wireOp",EDGE,"E2365.bottom");
            var Q27;
            Q27=sQuery(id+"F3.wireOp",EDGE,"E2361.left");
            var Q28;
            Q28=sQuery(id+"F3.wireOp",EDGE,"E2364.left");
            var Q29;
            Q29=sQuery(id+"F3.wireOp",EDGE,"E2365.left");
            var Q30;
            Q30=sQuery(id+"F3.wireOp",EDGE,"E2362.bottom");
            var Q31;
            Q31=sQuery(id+"F3.wireOp",EDGE,"E2358.bottom");
            var Q32;
            Q32=sQuery(id+"F3.wireOp",EDGE,"E2369.top");
            var Q33;
            Q33=sQuery(id+"F3.wireOp",EDGE,"E2360.left");
            var Q34;
            Q34=sQuery(id+"F3.wireOp",EDGE,"E2362.right");
            var Q35;
            Q35=sQuery(id+"F3.wireOp",EDGE,"E2358.top");
            var Q36;
            Q36=sQuery(id+"F3.wireOp",EDGE,"E2368.bottom");
            var Q37;
            Q37=sQuery(id+"F3.wireOp",EDGE,"E2364.top");
            var Q38;
            Q38=sQuery(id+"F3.wireOp",EDGE,"E2369.right");
            var Q39;
            Q39=sQuery(id+"F3.wireOp",EDGE,"E2366.right");
            var Q40;
            Q40=sQuery(id+"F3.wireOp",EDGE,"E2368.right");
            var Q41;
            Q41=sQuery(id+"F3.wireOp",EDGE,"E2370.left");
            var Q42;
            Q42=sQuery(id+"F3.wireOp",EDGE,"E2370.top");
            var Q43;
            Q43=sQuery(id+"F3.wireOp",EDGE,"E2369.left");
            var Q44;
            Q44=sQuery(id+"F3.wireOp",EDGE,"E2370.bottom");
            var Q45;
            Q45=sQuery(id+"F3.wireOp",EDGE,"E2368.left");
            var Q46;
            Q46=sQuery(id+"F3.wireOp",EDGE,"E2375.left");
            var Q47;
            Q47=sQuery(id+"F3.wireOp",EDGE,"E2375.bottom");
            var Q48;
            Q48=sQuery(id+"F3.wireOp",EDGE,"E2369.bottom");
            var Q49;
            Q49=sQuery(id+"F3.wireOp",EDGE,"E2375.top");
            var Q50;
            Q50=sQuery(id+"F3.wireOp",EDGE,"E2373.top");
            var Q51;
            Q51=sQuery(id+"F3.wireOp",EDGE,"E2380.right");
            var Q52;
            Q52=sQuery(id+"F3.wireOp",EDGE,"E2367.left");
            var Q53;
            Q53=sQuery(id+"F3.wireOp",EDGE,"E2367.bottom");
            var Q54;
            Q54=sQuery(id+"F3.wireOp",EDGE,"E2372.right");
            var Q55;
            Q55=sQuery(id+"F3.wireOp",EDGE,"E2372.bottom");
            var Q56;
            Q56=sQuery(id+"F3.wireOp",EDGE,"E2370.right");
            var Q57;
            Q57=sQuery(id+"F3.wireOp",EDGE,"E2375.right");
            var Q58;
            Q58=sQuery(id+"F3.wireOp",EDGE,"E2368.top");
            var Q59;
            Q59=sQuery(id+"F3.wireOp",EDGE,"E2373.right");
            var Q60;
            Q60=sQuery(id+"F3.wireOp",EDGE,"E2380.bottom");
            var Q61;
            Q61=sQuery(id+"F3.wireOp",EDGE,"E2372.left");
            var Q62;
            Q62=sQuery(id+"F3.wireOp",EDGE,"E2380.left");
            var Q63;
            Q63=sQuery(id+"F3.wireOp",EDGE,"E2373.bottom");
            var Q64;
            Q64=sQuery(id+"F3.wireOp",EDGE,"E2367.top");
            var Q65;
            Q65=sQuery(id+"F3.wireOp",EDGE,"E2373.left");
            var Q66;
            Q66=sQuery(id+"F3.wireOp",EDGE,"E2367.right");
            var Q67;
            Q67=sQuery(id+"F3.wireOp",EDGE,"E2374.bottom");
            var Q68;
            Q68=sQuery(id+"F3.wireOp",EDGE,"E2372.top");
            var Q69;
            Q69=sQuery(id+"F3.wireOp",EDGE,"E2378.bottom");
            var Q70;
            Q70=sQuery(id+"F3.wireOp",EDGE,"E2380.top");
            var Q71;
            Q71=sQuery(id+"F3.wireOp",EDGE,"E2371.bottom");
            var Q72;
            Q72=sQuery(id+"F3.wireOp",EDGE,"E2374.top");
            var Q73;
            Q73=sQuery(id+"F3.wireOp",EDGE,"E2371.left");
            var Q74;
            Q74=sQuery(id+"F3.wireOp",EDGE,"E2379.left");
            var Q75;
            Q75=sQuery(id+"F3.wireOp",EDGE,"E2378.top");
            var Q76;
            Q76=sQuery(id+"F3.wireOp",EDGE,"E2379.bottom");
            var Q77;
            Q77=sQuery(id+"F3.wireOp",EDGE,"E2377.right");
            var Q78;
            Q78=sQuery(id+"F3.wireOp",EDGE,"E2371.top");
            var Q79;
            Q79=sQuery(id+"F3.wireOp",EDGE,"E2379.right");
            var Q80;
            Q80=sQuery(id+"F3.wireOp",EDGE,"E2374.left");
            var Q81;
            Q81=sQuery(id+"F3.wireOp",EDGE,"E2379.top");
            var Q82;
            Q82=sQuery(id+"F3.wireOp",EDGE,"E2374.right");
            var Q83;
            Q83=sQuery(id+"F3.wireOp",EDGE,"E2376.bottom");
            var Q84;
            Q84=sQuery(id+"F3.wireOp",EDGE,"E2371.right");
            var Q85;
            Q85=sQuery(id+"F3.wireOp",EDGE,"E2378.right");
            var Q86;
            Q86=sQuery(id+"F3.wireOp",EDGE,"E2377.top");
            var Q87;
            Q87=sQuery(id+"F3.wireOp",EDGE,"E2376.right");
            var Q88;
            Q88=sQuery(id+"F3.wireOp",EDGE,"E2378.left");
            var Q89;
            Q89=sQuery(id+"F3.wireOp",EDGE,"E2377.bottom");
            var Q90;
            Q90=sQuery(id+"F3.wireOp",EDGE,"E2377.left");
            var Q91;
            Q91=sQuery(id+"F3.wireOp",EDGE,"E2376.left");
            var Q92;
            Q92=sQuery(id+"F3.wireOp",EDGE,"E2376.top");
            var Q93;
            Q93=sQuery(id+"F3.wireOp",EDGE,"cW22TeOh-E7AI-4V4I-WTME-2PvORLSgnyRA.right");
            var Q94;
            Q94=sQuery(id+"F3.wireOp",EDGE,"cW22TeOh-E7AI-4V4I-WTME-2PvORLSgnyRA.left");
            var Q95;
            Q95=sQuery(id+"F3.wireOp",EDGE,"cW22TeOh-E7AI-4V4I-WTME-2PvORLSgnyRA.top");
            var Q96;
            Q96=sQuery(id+"F3.wireOp",EDGE,"cW22TeOh-E7AI-4V4I-WTME-2PvORLSgnyRA.bottom");
            var Q97;
            Q97=makeQuery(id+"F2.opExtrude","SWEPT_BODY",BODY,{"disambiguationData":[OSD([sQuery(id+"F1.wireOp",EDGE,"E2356.bottom"),sQuery(id+"F1.wireOp",EDGE,"E2356.top"),sQuery(id+"F1.wireOp",EDGE,"E2356.left"),sQuery(id+"F1.wireOp",EDGE,"E2356.right")])]});
            extrude(context, id + "F4", {"entities" : qUnion([Q0]), "operationType" : NewBodyOperationType.REMOVE, "surfaceEntities" : qUnion([Q1, Q2, Q3, Q4, Q5, Q6, Q7, Q8, Q9, Q10, Q11, Q12, Q13, Q14, Q15, Q16, Q17, Q18, Q19, Q20, Q21, Q22, Q23, Q24, Q25, Q26, Q27, Q28, Q29, Q30, Q31, Q32, Q33, Q34, Q35, Q36, Q37, Q38, Q39, Q40, Q41, Q42, Q43, Q44, Q45, Q46, Q47, Q48, Q49, Q50, Q51, Q52, Q53, Q54, Q55, Q56, Q57, Q58, Q59, Q60, Q61, Q62, Q63, Q64, Q65, Q66, Q67, Q68, Q69, Q70, Q71, Q72, Q73, Q74, Q75, Q76, Q77, Q78, Q79, Q80, Q81, Q82, Q83, Q84, Q85, Q86, Q87, Q88, Q89, Q90, Q91, Q92, Q93, Q94, Q95, Q96]), "endBound" : BoundingType.UP_TO_BODY, "oppositeDirection" : true, "depth" : 25 * mm, "endBoundEntityBody" : qUnion([Q97]), "offsetDistance" : 25 * mm});
        }
    });
